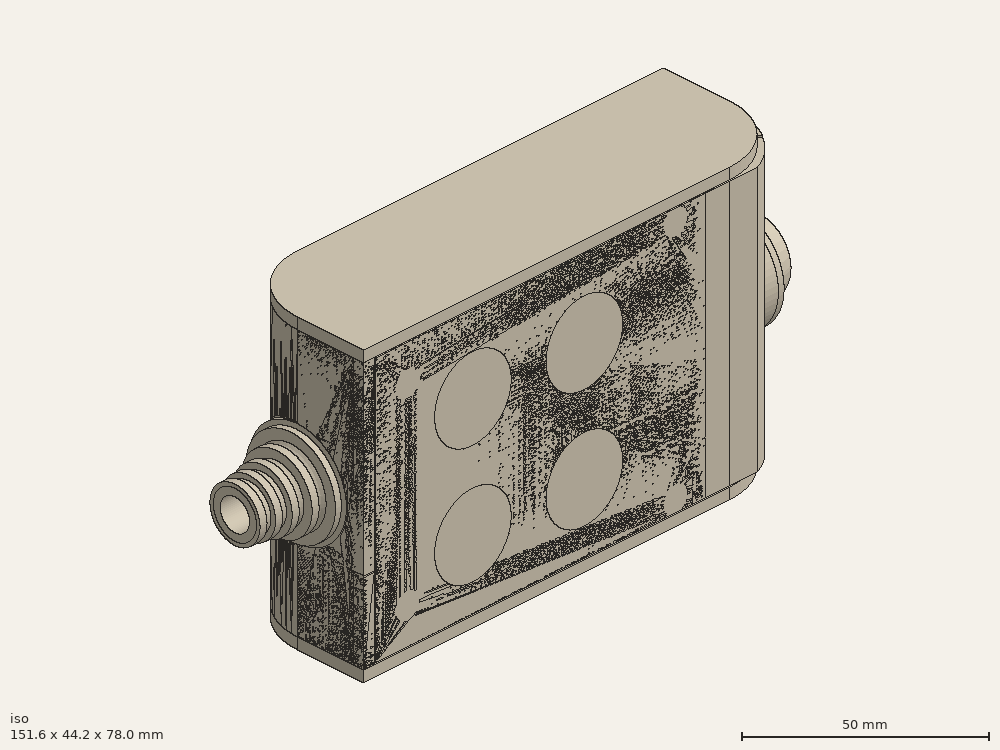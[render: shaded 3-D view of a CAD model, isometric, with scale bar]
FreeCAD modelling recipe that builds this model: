
FCSTD DOCUMENT  (FreeCAD 0.19R0.19.2)
Label: enclosure_158
License: All rights reserved
LicenseURL: http://en.wikipedia.org/wiki/All_rights_reserved
objects: Part::Feature×126, Part::Revolution×126, Part::MultiFuse×109, Sketcher::SketchObject×66, Part::Extrusion×51, Part::Cut×46, Part::Cylinder×44, Part::Fillet×43, Part::Box×28, App::MeasureDistance×4
note: 639 computed .brp shape members not serialized (recipe doc carries the construction recipe); baked Part::Feature solids carry a one-line shape summary decoded from their .brp

FEATURE [Sketcher::SketchObject] Sketch  label="topSketch"
  FullyConstrained = true
  sketch-geometry (20):
    g0: LineSegment StartX=5.21097e-06 StartY=3 StartZ=0 EndX=5.21097e-06 EndY=19 EndZ=0
    g1: ArcOfCircle CenterX=19 CenterY=19 CenterZ=0 NormalX=0 NormalY=0 NormalZ=1 AngleXU=0 Radius=19 StartAngle=1.5708 EndAngle=3.14159
    g2: ArcOfCircle CenterX=19 CenterY=19 CenterZ=0 NormalX=0 NormalY=0 NormalZ=1 AngleXU=0 Radius=16 StartAngle=1.5708 EndAngle=3.14159
    g3: LineSegment StartX=114 StartY=35 StartZ=0 EndX=19 EndY=35 EndZ=0
    g4: LineSegment StartX=5.21097e-06 StartY=3 StartZ=0 EndX=5.21097e-06 EndY=0 EndZ=0
    g5: LineSegment StartX=3 StartY=0 StartZ=0 EndX=5.21097e-06 EndY=0 EndZ=0
    g6: LineSegment StartX=3 StartY=19 StartZ=0 EndX=3 EndY=0 EndZ=0
    g7: LineSegment StartX=19 StartY=38 StartZ=0 EndX=124 EndY=38 EndZ=0
    g8: Circle CenterX=119 CenterY=35 CenterZ=0 NormalX=0 NormalY=0 NormalZ=1 AngleXU=0 Radius=1
    g9: Circle CenterX=121 CenterY=35 CenterZ=0 NormalX=0 NormalY=0 NormalZ=1 AngleXU=0 Radius=1
    g10: Circle CenterX=121 CenterY=33 CenterZ=0 NormalX=0 NormalY=0 NormalZ=1 AngleXU=0 Radius=1
    g11: BSplineCurve PolesCount=3 KnotsCount=2 Degree=2 IsPeriodic=0
    g12: GeomPoint X=119 Y=35 Z=0
    g13: GeomPoint X=121 Y=33 Z=0
    g14: LineSegment StartX=119 StartY=35 StartZ=0 EndX=114 EndY=35 EndZ=0
    g15: ArcOfCircle CenterX=105 CenterY=19 CenterZ=0 NormalX=0 NormalY=0 NormalZ=1 AngleXU=0 Radius=19 StartAngle=5.7297 EndAngle=6.28319
    g16: ArcOfCircle CenterX=105 CenterY=19 CenterZ=0 NormalX=0 NormalY=0 NormalZ=1 AngleXU=0 Radius=16 StartAngle=5.60905 EndAngle=6.28319
    g17: LineSegment StartX=121 StartY=33 StartZ=0 EndX=121 EndY=19 EndZ=0
    g18: LineSegment StartX=124 StartY=38 StartZ=0 EndX=124 EndY=19 EndZ=0
    g19: LineSegment StartX=117.5 StartY=9.01251 StartZ=0 EndX=121.163 EndY=9.0125 EndZ=0
  constraints (46):
    c: Vertical(g0)
    c: Block(g0)
    c: Coincident(g1,g0)
    c: Block(g1)
    c: Coincident(g2,g1)
    c: Block(g2)
    c: Coincident(g3,g2)
    c: Horizontal(g3)
    c: Tangent(g3,g2)
    c: Coincident(g4,g0)
    c: Distance(g4) = 3
    c: Vertical(g4)
    c: Coincident(g5,g4)
    c: Horizontal(g5)
    c: Coincident(g6,g2)
    c: Coincident(g6,g5)
    c: Vertical(g6)
    c: Horizontal(g7)
    c: Distance(g7) = 105
    c: Coincident(g7,g1)
    c: Block(g3)
    c: Weight(g8) = 1
    c: Equal(g8,g9)
    c: Equal(g8,g10)
    c: InternalAlignment(g8,g11)
    c: InternalAlignment(g9,g11)
    c: InternalAlignment(g10,g11)
    c: InternalAlignment(g12,g11)
    c: InternalAlignment(g13,g11)
    c: Block(g11)
    c: Coincident(g14,g11)
    c: Coincident(g14,g3)
    c: Horizontal(g14)
    c: Block(g15)
    c: Coincident(g16,g15)
    c: Block(g16)
    c: Coincident(g17,g11)
    c: Coincident(g17,g16)
    c: Vertical(g17)
    c: Distance(g17) = 14
    c: Coincident(g18,g7)
    c: Coincident(g18,g15)
    c: Vertical(g18)
    c: Distance(g18) = 19
    c: Coincident(g19,g16)
    c: Coincident(g19,g15)
FEATURE [Sketcher::SketchObject] Sketch001  label="bottomSketch"
  FullyConstrained = true
  sketch-geometry (32):
    g0: LineSegment StartX=3.3 StartY=-6.03275e-07 StartZ=0 EndX=98 EndY=-6.03275e-07 EndZ=0
    g1: ArcOfCircle CenterX=98 CenterY=19 CenterZ=0 NormalX=0 NormalY=0 NormalZ=1 AngleXU=0 Radius=19 StartAngle=4.71239 EndAngle=5.71103
    g2: LineSegment StartX=6.3 StartY=8 StartZ=0 EndX=3.3 EndY=8 EndZ=0
    g3: LineSegment StartX=3.3 StartY=8 StartZ=0 EndX=3.3 EndY=-6.03275e-07 EndZ=0
    g4: ArcOfCircle CenterX=8.3 CenterY=5 CenterZ=0 NormalX=0 NormalY=0 NormalZ=1 AngleXU=0 Radius=2 StartAngle=3.14159 EndAngle=4.71239
    g5: LineSegment StartX=6.3 StartY=8 StartZ=0 EndX=6.3 EndY=5 EndZ=0
    g6: ArcOfCircle CenterX=98 CenterY=19 CenterZ=0 NormalX=0 NormalY=0 NormalZ=1 AngleXU=0 Radius=12.7 StartAngle=4.71239 EndAngle=6.28319
    g7: LineSegment StartX=94.7 StartY=3 StartZ=0 EndX=8.3 EndY=3 EndZ=0
    g8-g12: Circle x5 (B-spline internal-alignment scaffolding for g13; pole/knot coordinates omitted)
    g13: BSplineCurve PolesCount=5 KnotsCount=3 Degree=3 IsPeriodic=0
    g14: GeomPoint X=98 Y=6.3 Z=0
    g15: GeomPoint X=96.3938 Y=4.71946 Z=0
    g16: GeomPoint X=94.7 Y=3 Z=0
    g17-g23: Circle x7 (B-spline internal-alignment scaffolding for g24; pole/knot coordinates omitted)
    g24: BSplineCurve PolesCount=7 KnotsCount=5 Degree=3 IsPeriodic=0
    g25-g29: GeomPoint x5 (B-spline internal-alignment scaffolding for g24; pole/knot coordinates omitted)
    g30: ArcOfCircle CenterX=98 CenterY=19 CenterZ=0 NormalX=0 NormalY=0 NormalZ=1 AngleXU=0 Radius=15.7 StartAngle=5.81226 EndAngle=6.28319
    g31: LineSegment StartX=110.7 StartY=19 StartZ=0 EndX=113.7 EndY=19 EndZ=0
  constraints (41):
    c: Horizontal(g0)
    c: Coincident(g1,g0)
    c: Block(g1)
    c: Horizontal(g2)
    c: Distance(g2) = 3
    c: Coincident(g3,g2)
    c: Vertical(g3)
    c: Coincident(g3,g0)
    c: Block(g4)
    c: Block(g2)
    c: Coincident(g5,g2)
    c: Coincident(g5,g4)
    c: Vertical(g5)
    c: Coincident(g6,g1)
    c: Block(g6)
    c: Coincident(g7,g4)
    c: Horizontal(g7)
    c: Block(g0)
    c: Block(g7)
    c: Block(g3)
    c: Coincident(g13,g6)
    c: Weight(g8) = 1
    c: Equal(g8, g9-g12) x4
    c: Coincident(g13,g7)
    c: InternalAlignment(g8-g12 -> g13) x5
    c: InternalAlignment(g14,g13)
    c: InternalAlignment(g15,g13)
    c: InternalAlignment(g16,g13)
    c: Block(g13)
    c: Weight(g17) = 1
    c: Equal(g17, g18-g23) x6
    c: Coincident(g24,g1)
    c: InternalAlignment(g17-g23 -> g24) x7
    c: InternalAlignment(g25-g29 -> g24) x5
    c: Block(g24)
    c: Coincident(g30,g24)
    c: Coincident(g31,g6)
    c: Coincident(g31,g30)
    c: Horizontal(g31)
    c: Block(g31)
    c: Block(g30)
FEATURE [Part::Extrusion] Extrude  label="top"
  Base = -> Sketch
  Dir = (0,0,1)
  DirMode = 2
  FaceMakerClass = Part::FaceMakerBullseye
  LengthFwd = 72
  LengthRev = 0
  Solid = true
  Symmetric = false
FEATURE [Part::Extrusion] Extrude001  label="bottom"
  Base = -> Sketch001
  Dir = (0,0,1)
  DirMode = 2
  FaceMakerClass = Part::FaceMakerBullseye
  LengthFwd = 71.4
  LengthRev = 0
  Placement = pos=(0,0,0.3) rot=(0,0,1;0rad)
  Solid = true
  Symmetric = false
FEATURE [Sketcher::SketchObject] Sketch002  label="topSketch001"
  FullyConstrained = true
  sketch-geometry (6):
    g0: ArcOfCircle CenterX=19 CenterY=19 CenterZ=0 NormalX=0 NormalY=0 NormalZ=1 AngleXU=0 Radius=19 StartAngle=1.5708 EndAngle=3.14159
    g1: LineSegment StartX=5.22862e-06 StartY=19 StartZ=0 EndX=5.22862e-06 EndY=1.19904e-11 EndZ=0
    g2: LineSegment StartX=19 StartY=38 StartZ=0 EndX=124 EndY=38 EndZ=0
    g3: LineSegment StartX=5.22862e-06 StartY=1.19904e-11 StartZ=0 EndX=105 EndY=1.19904e-11 EndZ=0
    g4: ArcOfCircle CenterX=105 CenterY=19 CenterZ=0 NormalX=0 NormalY=0 NormalZ=1 AngleXU=0 Radius=19 StartAngle=4.71239 EndAngle=6.28319
    g5: LineSegment StartX=124 StartY=38 StartZ=0 EndX=124 EndY=19 EndZ=0
  constraints (16):
    c: Block(g0)
    c: Coincident(g1,g0)
    c: Vertical(g1)
    c: Horizontal(g2)
    c: Distance(g2) = 105
    c: Coincident(g2,g0)
    c: Distance(g1) = 19
    c: Coincident(g3,g1)
    c: Horizontal(g3)
    c: Distance(g3) = 105
    c: Block(g4)
    c: Coincident(g4,g3)
    c: Coincident(g5,g2)
    c: Coincident(g5,g4)
    c: Vertical(g5)
    c: Distance(g5) = 19
FEATURE [Part::Extrusion] Extrude002  label="sideA"
  Base = -> Sketch002
  Dir = (0,0,1)
  DirMode = 2
  FaceMakerClass = Part::FaceMakerBullseye
  LengthFwd = 3
  LengthRev = 0
  Placement = pos=(0,0,-3) rot=(0,0,1;0rad)
  Solid = true
  Symmetric = false
FEATURE [Sketcher::SketchObject] Sketch003  label="topSketch002"
  FullyConstrained = true
  sketch-geometry (6):
    g0: LineSegment StartX=19 StartY=38 StartZ=0 EndX=117 EndY=38 EndZ=0
    g1: ArcOfCircle CenterX=19 CenterY=19 CenterZ=0 NormalX=0 NormalY=0 NormalZ=1 AngleXU=0 Radius=19 StartAngle=1.5708 EndAngle=3.14159
    g2: LineSegment StartX=117 StartY=38 StartZ=0 EndX=117 EndY=19 EndZ=0
    g3: LineSegment StartX=98 StartY=1.0161e-12 StartZ=0 EndX=5.22862e-06 EndY=1.0161e-12 EndZ=0
    g4: LineSegment StartX=5.22862e-06 StartY=19 StartZ=0 EndX=5.22862e-06 EndY=1.0161e-12 EndZ=0
    g5: ArcOfCircle CenterX=98 CenterY=19 CenterZ=0 NormalX=0 NormalY=0 NormalZ=1 AngleXU=0 Radius=19 StartAngle=4.71239 EndAngle=6.28319
  constraints (16):
    c: Horizontal(g0)
    c: Distance(g0) = 98
    c: Coincident(g1,g0)
    c: Block(g1)
    c: Coincident(g2,g0)
    c: Vertical(g2)
    c: Distance(g2) = 19
    c: Horizontal(g3)
    c: Coincident(g4,g1)
    c: Vertical(g4)
    c: Coincident(g3,g4)
    c: Block(g3)
    c: Coincident(g5,g2)
    c: Coincident(g5,g3)
    c: Block(g0)
    c: Block(g5)
FEATURE [Sketcher::SketchObject] Sketch004
  FullyConstrained = true
  MapMode = 3
  Placement = pos=(0,0,0) rot=(1,0,0;1.5708rad)
  Support = -> [Extrude]
  sketch-geometry (8):
    g0: Circle CenterX=80.351 CenterY=-67.6202 CenterZ=0 NormalX=0 NormalY=0 NormalZ=1 AngleXU=0 Radius=2
    g1: Circle CenterX=80.351 CenterY=-67.6202 CenterZ=0 NormalX=0 NormalY=0 NormalZ=1 AngleXU=0 Radius=3
    g2: Circle CenterX=80.351 CenterY=-4.92017 CenterZ=0 NormalX=0 NormalY=0 NormalZ=1 AngleXU=0 Radius=2
    g3: Circle CenterX=80.351 CenterY=-4.92017 CenterZ=0 NormalX=0 NormalY=0 NormalZ=1 AngleXU=0 Radius=3
    g4: Circle CenterX=23.851 CenterY=-4.92017 CenterZ=0 NormalX=0 NormalY=0 NormalZ=1 AngleXU=0 Radius=2
    g5: Circle CenterX=23.851 CenterY=-4.92017 CenterZ=0 NormalX=0 NormalY=0 NormalZ=1 AngleXU=0 Radius=3
    g6: Circle CenterX=23.851 CenterY=-67.6202 CenterZ=0 NormalX=0 NormalY=0 NormalZ=1 AngleXU=0 Radius=2
    g7: Circle CenterX=23.851 CenterY=-67.6202 CenterZ=0 NormalX=0 NormalY=0 NormalZ=1 AngleXU=0 Radius=3
  constraints (8):
    c: Block(g3)
    c: Block(g2)
    c: Block(g1)
    c: Block(g0)
    c: Block(g6)
    c: Block(g7)
    c: Block(g4)
    c: Block(g5)
FEATURE [Part::Extrusion] Extrude004
  Base = -> Sketch004
  Dir = (0,-1,2e-16)
  DirMode = 2
  FaceMakerClass = Part::FaceMakerBullseye
  LengthFwd = 6
  LengthRev = 0
  Placement = pos=(0,9,0) rot=(0,0,1;0rad)
  Solid = true
  Symmetric = false
FEATURE [Sketcher::SketchObject] Sketch005
  FullyConstrained = true
  MapMode = 3
  Placement = pos=(0,0,0) rot=(1,0,0;1.5708rad)
  Support = -> [Extrude]
  sketch-geometry (8):
    g0: Circle CenterX=80.351 CenterY=-67.6202 CenterZ=0 NormalX=0 NormalY=0 NormalZ=1 AngleXU=0 Radius=3
    g1: Circle CenterX=80.351 CenterY=-4.92017 CenterZ=0 NormalX=0 NormalY=0 NormalZ=1 AngleXU=0 Radius=3
    g2: Circle CenterX=23.851 CenterY=-4.92017 CenterZ=0 NormalX=0 NormalY=0 NormalZ=1 AngleXU=0 Radius=3
    g3: Circle CenterX=23.851 CenterY=-67.6202 CenterZ=0 NormalX=0 NormalY=0 NormalZ=1 AngleXU=0 Radius=3
    g4: Circle CenterX=23.851 CenterY=-67.6202 CenterZ=0 NormalX=0 NormalY=0 NormalZ=1 AngleXU=0 Radius=5
    g5: Circle CenterX=80.351 CenterY=-67.6202 CenterZ=0 NormalX=0 NormalY=0 NormalZ=1 AngleXU=0 Radius=5
    g6: Circle CenterX=23.851 CenterY=-4.92017 CenterZ=0 NormalX=0 NormalY=0 NormalZ=1 AngleXU=0 Radius=5
    g7: Circle CenterX=80.351 CenterY=-4.92017 CenterZ=0 NormalX=0 NormalY=0 NormalZ=1 AngleXU=0 Radius=5
  constraints (8):
    c: Block(g1)
    c: Block(g0)
    c: Block(g3)
    c: Block(g2)
    c: Block(g5)
    c: Block(g4)
    c: Block(g6)
    c: Block(g7)
FEATURE [Part::Extrusion] Extrude005
  Base = -> Sketch005
  Dir = (0,-1,2e-16)
  DirMode = 2
  FaceMakerClass = Part::FaceMakerBullseye
  LengthFwd = 2
  LengthRev = 0
  Solid = true
  Symmetric = false
FEATURE [Sketcher::SketchObject] Sketch006
  FullyConstrained = true
  MapMode = 3
  Placement = pos=(0,0,0) rot=(1,0,0;1.5708rad)
  sketch-geometry (8):
    g0: Circle CenterX=80.351 CenterY=-67.6202 CenterZ=0 NormalX=0 NormalY=0 NormalZ=1 AngleXU=0 Radius=3
    g1: Circle CenterX=80.351 CenterY=-4.92017 CenterZ=0 NormalX=0 NormalY=0 NormalZ=1 AngleXU=0 Radius=3
    g2: Circle CenterX=23.851 CenterY=-4.92017 CenterZ=0 NormalX=0 NormalY=0 NormalZ=1 AngleXU=0 Radius=3
    g3: Circle CenterX=23.851 CenterY=-67.6202 CenterZ=0 NormalX=0 NormalY=0 NormalZ=1 AngleXU=0 Radius=3
    g4: Circle CenterX=23.851 CenterY=-67.6202 CenterZ=0 NormalX=0 NormalY=0 NormalZ=1 AngleXU=0 Radius=5
    g5: Circle CenterX=80.351 CenterY=-67.6202 CenterZ=0 NormalX=0 NormalY=0 NormalZ=1 AngleXU=0 Radius=5
    g6: Circle CenterX=23.851 CenterY=-4.92017 CenterZ=0 NormalX=0 NormalY=0 NormalZ=1 AngleXU=0 Radius=5
    g7: Circle CenterX=80.351 CenterY=-4.92017 CenterZ=0 NormalX=0 NormalY=0 NormalZ=1 AngleXU=0 Radius=5
  constraints (8):
    c: Block(g1)
    c: Block(g0)
    c: Block(g3)
    c: Block(g2)
    c: Block(g5)
    c: Block(g4)
    c: Block(g6)
    c: Block(g7)
FEATURE [Part::Extrusion] Extrude007
  Base = -> Sketch006
  Dir = (0,-1,2e-16)
  DirMode = 2
  FaceMakerClass = Part::FaceMakerBullseye
  LengthFwd = 2
  LengthRev = 0
  Solid = true
  Symmetric = false
FEATURE [Part::Fillet] Fillet
  Base = -> Extrude007
  Edges = 4 edges r=1.99: [Edge6,Edge12,Edge18,Edge24]
FEATURE [Part::Cut] Cut
  Base = -> Extrude005
  Placement = pos=(0,5,0) rot=(0,0,1;0rad)
  Tool = -> Fillet
FEATURE [Part::MultiFuse] Fusion  label="pCBScrews"
  Placement = pos=(-2.5,0,72.3) rot=(0,0,1;0rad)
  Shapes = -> [Extrude004,Cut]
FEATURE [App::MeasureDistance] Distance  label="Distance: 0.69 mm"
  Distance = 0.685967
  P1 = (24.0138,2.9647,0.3)
  P2 = (23.8901,3,-0.373787)
FEATURE [App::MeasureDistance] Distance001  label="Distance: 0.53 mm"
  Distance = 0.533607
  P1 = (80.2939,3,72.2334)
  P2 = (80.281,2.99661,71.7)
FEATURE [Part::Fillet] Fillet001
  Base = -> Extrude001
  Edges = 1 edges r=2.4: [Edge17]
FEATURE [Part::Fillet] Fillet002  label="bottom001"
  Base = -> Fillet001
  Edges = 1 edges r=2.4: [Edge36]
FEATURE [Part::Fillet] Fillet003  label="top001"
  Base = -> Extrude
  Edges = 1 edges r=2: [Edge1]
FEATURE [Sketcher::SketchObject] Sketch007
  FullyConstrained = true
  sketch-geometry (16):
    g0: LineSegment StartX=4 StartY=0 StartZ=0 EndX=4 EndY=2.4 EndZ=0
    g1: LineSegment StartX=4 StartY=2.4 StartZ=0 EndX=7 EndY=2.4 EndZ=0
    g2: LineSegment StartX=4 StartY=0 StartZ=0 EndX=5.7 EndY=0 EndZ=0
    g3: LineSegment StartX=5.7 StartY=0 StartZ=0 EndX=5.7 EndY=-5.6 EndZ=0
    g4-g8: Circle x5 (B-spline internal-alignment scaffolding for g9; pole/knot coordinates omitted)
    g9: BSplineCurve PolesCount=5 KnotsCount=3 Degree=3 IsPeriodic=0
    g10: GeomPoint X=7 Y=2.4 Z=0
    g11: GeomPoint X=10.4582 Y=-1.55472 Z=0
    g12: GeomPoint X=14 Y=-5.6 Z=0
    g13: LineSegment StartX=14 StartY=-5.6 StartZ=0 EndX=14 EndY=-14.1 EndZ=0
    g14: LineSegment StartX=14 StartY=-14.1 StartZ=0 EndX=6.5 EndY=-14.1 EndZ=0
    g15: LineSegment StartX=5.7 StartY=-5.6 StartZ=0 EndX=6.5 EndY=-14.1 EndZ=0
  constraints (28):
    c: Distance(g0) = 2.4
    c: Vertical(g0)
    c: Block(g0)
    c: Coincident(g1,g0)
    c: Horizontal(g1)
    c: Distance(g1) = 3
    c: Coincident(g2,g0)
    c: Horizontal(g2)
    c: Distance(g2) = 1.7
    c: Coincident(g3,g2)
    c: Vertical(g3)
    c: Distance(g3) = 5.6
    c: Coincident(g9,g1)
    c: Weight(g4) = 1
    c: Equal(g4, g5-g8) x4
    c: InternalAlignment(g4-g8 -> g9) x5
    c: InternalAlignment(g10,g9)
    c: InternalAlignment(g11,g9)
    c: InternalAlignment(g12,g9)
    c: Block(g9)
    c: Coincident(g13,g9)
    c: Vertical(g13)
    c: Distance(g13) = 8.5
    c: Coincident(g14,g13)
    c: Horizontal(g14)
    c: Distance(g14) = 7.5
    c: Coincident(g15,g3)
    c: Coincident(g15,g14)
FEATURE [Part::Feature] Face
  shape: bbox 10 x 16.5 x 2e-07 mm, 1 faces, 0 solids (baked)
FEATURE [Part::Revolution] Revolve  label="plugHousing"
  Angle = 360
  Axis = (0,1,0)
  Base = (0,0,0)
  FaceMakerClass = Part::FaceMakerBullseye
  Placement = pos=(0,0,36.15) rot=(0,0,1;0rad)
  Solid = false
  Source = -> Face
  Symmetric = false
FEATURE [Part::Feature] Face001
  shape: bbox 10 x 16.5 x 2e-07 mm, 1 faces, 0 solids (baked)
FEATURE [Part::Revolution] Revolve001  label="plugHousing001"
  Angle = 360
  Axis = (0,1,0)
  Base = (0,0,0)
  FaceMakerClass = Part::FaceMakerBullseye
  Placement = pos=(0,0,36.15) rot=(0,0,1;0rad)
  Solid = false
  Source = -> Face001
  Symmetric = false
FEATURE [Part::MultiFuse] Fusion001  label="plugHousing002"
  Placement = pos=(0,0,0) rot=(0,0,1;1.5708rad)
  Shapes = -> [Revolve001,Revolve]
FEATURE [Part::Feature] Face002
  shape: bbox 10 x 16.5 x 2e-07 mm, 1 faces, 0 solids (baked)
FEATURE [Part::Revolution] Revolve003  label="plugHousing005"
  Angle = 360
  Axis = (0,1,0)
  Base = (0,0,0)
  FaceMakerClass = Part::FaceMakerBullseye
  Placement = pos=(0,0,36.15) rot=(0,0,1;0rad)
  Solid = false
  Source = -> Face002
  Symmetric = false
FEATURE [Part::Feature] Face003
  shape: bbox 10 x 16.5 x 2e-07 mm, 1 faces, 0 solids (baked)
FEATURE [Part::Revolution] Revolve002  label="plugHousing003"
  Angle = 360
  Axis = (0,1,0)
  Base = (0,0,0)
  FaceMakerClass = Part::FaceMakerBullseye
  Placement = pos=(0,0,36.15) rot=(0,0,1;0rad)
  Solid = false
  Source = -> Face003
  Symmetric = false
FEATURE [Part::MultiFuse] Fusion002  label="plugHousing004"
  Placement = pos=(0,0,0) rot=(0,0,1;1.5708rad)
  Shapes = -> [Revolve002,Revolve003]
FEATURE [Part::MultiFuse] Fusion003  label="plugHousing006"
  Placement = pos=(0,19,0) rot=(0,0,1;3.14159rad)
  Shapes = -> [Fusion002,Fusion001]
FEATURE [Part::Feature] Face004
  shape: bbox 10 x 16.5 x 2e-07 mm, 1 faces, 0 solids (baked)
FEATURE [Part::Revolution] Revolve006  label="plugHousing010"
  Angle = 360
  Axis = (0,1,0)
  Base = (0,0,0)
  FaceMakerClass = Part::FaceMakerBullseye
  Placement = pos=(0,0,36.15) rot=(0,0,1;0rad)
  Solid = false
  Source = -> Face004
  Symmetric = false
FEATURE [Part::Feature] Face005
  shape: bbox 10 x 16.5 x 2e-07 mm, 1 faces, 0 solids (baked)
FEATURE [Part::Revolution] Revolve007  label="plugHousing011"
  Angle = 360
  Axis = (0,1,0)
  Base = (0,0,0)
  FaceMakerClass = Part::FaceMakerBullseye
  Placement = pos=(0,0,36.15) rot=(0,0,1;0rad)
  Solid = false
  Source = -> Face005
  Symmetric = false
FEATURE [Part::Feature] Face006
  shape: bbox 10 x 16.5 x 2e-07 mm, 1 faces, 0 solids (baked)
FEATURE [Part::Revolution] Revolve004  label="plugHousing007"
  Angle = 360
  Axis = (0,1,0)
  Base = (0,0,0)
  FaceMakerClass = Part::FaceMakerBullseye
  Placement = pos=(0,0,36.15) rot=(0,0,1;0rad)
  Solid = false
  Source = -> Face006
  Symmetric = false
FEATURE [Part::MultiFuse] Fusion004  label="plugHousing009"
  Placement = pos=(0,0,0) rot=(0,0,1;1.5708rad)
  Shapes = -> [Revolve004,Revolve007]
FEATURE [Part::Feature] Face007
  shape: bbox 10 x 16.5 x 2e-07 mm, 1 faces, 0 solids (baked)
FEATURE [Part::Revolution] Revolve005  label="plugHousing008"
  Angle = 360
  Axis = (0,1,0)
  Base = (0,0,0)
  FaceMakerClass = Part::FaceMakerBullseye
  Placement = pos=(0,0,36.15) rot=(0,0,1;0rad)
  Solid = false
  Source = -> Face007
  Symmetric = false
FEATURE [Part::MultiFuse] Fusion005  label="plugHousing012"
  Placement = pos=(0,0,0) rot=(0,0,1;1.5708rad)
  Shapes = -> [Revolve006,Revolve005]
FEATURE [Part::MultiFuse] Fusion006  label="plugHousing013"
  Placement = pos=(0,19,0) rot=(0,0,1;3.14159rad)
  Shapes = -> [Fusion005,Fusion004]
FEATURE [Part::MultiFuse] Fusion007  label="plugHousing014"
  Placement = pos=(122.621,0,-0.15) rot=(0,0,1;0rad)
  Shapes = -> [Fusion003,Fusion006]
FEATURE [Part::Cylinder] Cylinder002
  Angle = 360
  AttacherType = Attacher::AttachEngine3D
  Height = 20
  Placement = pos=(0,0,36.15) rot=(0,0,1;0rad)
  Radius = 4
FEATURE [Part::Cylinder] Cylinder003
  Angle = 360
  AttacherType = Attacher::AttachEngine3D
  Height = 10
  Placement = pos=(0,0,36.15) rot=(0,0,1;0rad)
  Radius = 4
FEATURE [Part::MultiFuse] Fusion009  label="removeToCreateHoleForPlugHousing"
  Placement = pos=(70,19,36.15) rot=(0,1,0;1.5708rad)
  Shapes = -> [Cylinder002,Cylinder003]
FEATURE [Part::Cylinder] Cylinder004
  Angle = 360
  AttacherType = Attacher::AttachEngine3D
  Height = 20
  Placement = pos=(0,0,36.15) rot=(0,0,1;0rad)
  Radius = 4
FEATURE [Part::Cylinder] Cylinder005
  Angle = 360
  AttacherType = Attacher::AttachEngine3D
  Height = 10
  Placement = pos=(0,0,36.15) rot=(0,0,1;0rad)
  Radius = 4
FEATURE [Part::MultiFuse] Fusion010  label="removeToCreateHoleForPlugHousing001"
  Placement = pos=(70,19,36.15) rot=(0,1,0;1.5708rad)
  Shapes = -> [Cylinder004,Cylinder005]
FEATURE [Part::Cut] Cut001
  Base = -> Fillet003
  Tool = -> Fusion010
FEATURE [Part::Cut] Cut002  label="Bottom"
  Base = -> Fillet002
  Tool = -> Fusion009
FEATURE [Part::Feature] Face008
  shape: bbox 10 x 16.5 x 2e-07 mm, 1 faces, 0 solids (baked)
FEATURE [Part::Revolution] Revolve011  label="plugHousing021"
  Angle = 360
  Axis = (0,1,0)
  Base = (0,0,0)
  FaceMakerClass = Part::FaceMakerBullseye
  Placement = pos=(0,0,36.15) rot=(0,0,1;0rad)
  Solid = false
  Source = -> Face008
  Symmetric = false
FEATURE [Part::Feature] Face009
  shape: bbox 10 x 16.5 x 2e-07 mm, 1 faces, 0 solids (baked)
FEATURE [Part::Revolution] Revolve012  label="plugHousing022"
  Angle = 360
  Axis = (0,1,0)
  Base = (0,0,0)
  FaceMakerClass = Part::FaceMakerBullseye
  Placement = pos=(0,0,36.15) rot=(0,0,1;0rad)
  Solid = false
  Source = -> Face009
  Symmetric = false
FEATURE [Part::Feature] Face010 .. Face013  x4 (patterned run collapsed; names and placements below)
  shape: bbox 10 x 16.5 x 2e-07 mm, 1 faces, 0 solids (baked)
FEATURE [Part::Revolution] Revolve015  label="plugHousing027"
  Angle = 360
  Axis = (0,1,0)
  Base = (0,0,0)
  FaceMakerClass = Part::FaceMakerBullseye
  Placement = pos=(0,0,36.15) rot=(0,0,1;0rad)
  Solid = false
  Source = -> Face013
  Symmetric = false
FEATURE [Part::Feature] Face014
  shape: bbox 10 x 16.5 x 2e-07 mm, 1 faces, 0 solids (baked)
FEATURE [Part::Feature] Face015
  shape: bbox 10 x 16.5 x 2e-07 mm, 1 faces, 0 solids (baked)
FEATURE [Part::Feature] Face016
  shape: bbox 10 x 16.5 x 2e-07 mm, 1 faces, 0 solids (baked)
FEATURE [Part::Revolution] Revolve019  label="plugHousing033"
  Angle = 360
  Axis = (0,1,0)
  Base = (0,0,0)
  FaceMakerClass = Part::FaceMakerBullseye
  Placement = pos=(0,0,36.15) rot=(0,0,1;0rad)
  Solid = false
  Source = -> Face016
  Symmetric = false
FEATURE [Part::Feature] Face017
  shape: bbox 10 x 16.5 x 2e-07 mm, 1 faces, 0 solids (baked)
FEATURE [Part::Revolution] Revolve020  label="plugHousing034"
  Angle = 360
  Axis = (0,1,0)
  Base = (0,0,0)
  FaceMakerClass = Part::FaceMakerBullseye
  Placement = pos=(0,0,36.15) rot=(0,0,1;0rad)
  Solid = false
  Source = -> Face017
  Symmetric = false
FEATURE [Part::Feature] Face018
  shape: bbox 10 x 16.5 x 2e-07 mm, 1 faces, 0 solids (baked)
FEATURE [Part::Revolution] Revolve016  label="plugHousing030"
  Angle = 360
  Axis = (0,1,0)
  Base = (0,0,0)
  FaceMakerClass = Part::FaceMakerBullseye
  Placement = pos=(0,0,36.15) rot=(0,0,1;0rad)
  Solid = false
  Source = -> Face018
  Symmetric = false
FEATURE [Part::MultiFuse] Fusion020  label="plugHousing038"
  Placement = pos=(0,0,0) rot=(0,0,1;1.5708rad)
  Shapes = -> [Revolve016,Revolve020]
FEATURE [Part::Feature] Face019
  shape: bbox 10 x 16.5 x 2e-07 mm, 1 faces, 0 solids (baked)
FEATURE [Part::Feature] Face020
  shape: bbox 10 x 16.5 x 2e-07 mm, 1 faces, 0 solids (baked)
FEATURE [Part::Revolution] Revolve017  label="plugHousing031"
  Angle = 360
  Axis = (0,1,0)
  Base = (0,0,0)
  FaceMakerClass = Part::FaceMakerBullseye
  Placement = pos=(0,0,36.15) rot=(0,0,1;0rad)
  Solid = false
  Source = -> Face020
  Symmetric = false
FEATURE [Part::MultiFuse] Fusion021  label="plugHousing039"
  Placement = pos=(0,0,0) rot=(0,0,1;1.5708rad)
  Shapes = -> [Revolve019,Revolve017]
FEATURE [Part::MultiFuse] Fusion023  label="plugHousing041"
  Placement = pos=(0,19,0) rot=(0,0,1;3.14159rad)
  Shapes = -> [Fusion021,Fusion020]
FEATURE [Part::Revolution] Revolve022  label="plugHousing043"
  Angle = 360
  Axis = (0,1,0)
  Base = (0,0,0)
  FaceMakerClass = Part::FaceMakerBullseye
  Placement = pos=(0,0,36.15) rot=(0,0,1;0rad)
  Solid = false
  Source = -> Face019
  Symmetric = false
FEATURE [Part::Feature] Face021
  shape: bbox 10 x 16.5 x 2e-07 mm, 1 faces, 0 solids (baked)
FEATURE [Part::Revolution] Revolve023  label="plugHousing044"
  Angle = 360
  Axis = (0,1,0)
  Base = (0,0,0)
  FaceMakerClass = Part::FaceMakerBullseye
  Placement = pos=(0,0,36.15) rot=(0,0,1;0rad)
  Solid = false
  Source = -> Face021
  Symmetric = false
FEATURE [Part::Feature] Face022
  shape: bbox 10 x 16.5 x 2e-07 mm, 1 faces, 0 solids (baked)
FEATURE [Part::Revolution] Revolve018  label="plugHousing032"
  Angle = 360
  Axis = (0,1,0)
  Base = (0,0,0)
  FaceMakerClass = Part::FaceMakerBullseye
  Placement = pos=(0,0,36.15) rot=(0,0,1;0rad)
  Solid = false
  Source = -> Face022
  Symmetric = false
FEATURE [Part::MultiFuse] Fusion022  label="plugHousing040"
  Placement = pos=(0,0,0) rot=(0,0,1;1.5708rad)
  Shapes = -> [Revolve018,Revolve023]
FEATURE [Part::Feature] Face023
  shape: bbox 10 x 16.5 x 2e-07 mm, 1 faces, 0 solids (baked)
FEATURE [Part::Revolution] Revolve021  label="plugHousing035"
  Angle = 360
  Axis = (0,1,0)
  Base = (0,0,0)
  FaceMakerClass = Part::FaceMakerBullseye
  Placement = pos=(0,0,36.15) rot=(0,0,1;0rad)
  Solid = false
  Source = -> Face023
  Symmetric = false
FEATURE [Part::MultiFuse] Fusion018  label="plugHousing036"
  Placement = pos=(0,0,0) rot=(0,0,1;1.5708rad)
  Shapes = -> [Revolve022,Revolve021]
FEATURE [Part::MultiFuse] Fusion019  label="plugHousing037"
  Placement = pos=(0,19,0) rot=(0,0,1;3.14159rad)
  Shapes = -> [Fusion018,Fusion022]
FEATURE [Part::MultiFuse] Fusion024  label="plugHousing042"
  Placement = pos=(122.621,0,-0.15) rot=(0,0,1;0rad)
  Shapes = -> [Fusion023,Fusion019]
FEATURE [Part::Cylinder] Cylinder006
  Angle = 360
  AttacherType = Attacher::AttachEngine3D
  Height = 20
  Placement = pos=(0,0,36.15) rot=(0,0,1;0rad)
  Radius = 14.3
FEATURE [Part::Cylinder] Cylinder007
  Angle = 360
  AttacherType = Attacher::AttachEngine3D
  Height = 10
  Placement = pos=(0,0,36.15) rot=(0,0,1;0rad)
  Radius = 4
FEATURE [Part::MultiFuse] Fusion026  label="removeToCreteHoleForPlugHousing"
  Placement = pos=(70,19,36) rot=(0,1,0;1.5708rad)
  Shapes = -> [Cylinder006,Cylinder007]
FEATURE [Part::Box] Box001  label="Cube001"
  AttacherType = Attacher::AttachEngine3D
  Height = 28
  Length = 3
  Placement = pos=(110.7,19,22) rot=(0,0,1;0rad)
  Width = 15.7
FEATURE [Part::Cut] Cut003  label="top002"
  Base = -> Cut001
  Tool = -> Fusion007
FEATURE [Part::Revolution] Revolve008  label="plugHousing015"
  Angle = 360
  Axis = (0,1,0)
  Base = (0,0,0)
  FaceMakerClass = Part::FaceMakerBullseye
  Placement = pos=(0,0,36.15) rot=(0,0,1;0rad)
  Solid = false
  Source = -> Face010
  Symmetric = false
FEATURE [Part::MultiFuse] Fusion013  label="plugHousing020"
  Placement = pos=(0,0,0) rot=(0,0,1;1.5708rad)
  Shapes = -> [Revolve008,Revolve012]
FEATURE [Part::Cut] Cut004  label="top003"
  Base = -> Cut003
  Placement = pos=(1,0,0) rot=(0,0,1;0rad)
  Tool = -> Fusion026
FEATURE [Part::Cylinder] Cylinder008
  Angle = 360
  AttacherType = Attacher::AttachEngine3D
  Height = 20
  Placement = pos=(0,0,36.15) rot=(0,0,1;0rad)
  Radius = 10.3
FEATURE [Part::Cylinder] Cylinder009
  Angle = 360
  AttacherType = Attacher::AttachEngine3D
  Height = 10
  Placement = pos=(0,0,36.15) rot=(0,0,1;0rad)
  Radius = 4
FEATURE [Part::MultiFuse] Fusion027  label="removeToCreteHoleForPlugHousing001"
  Placement = pos=(70,19,36) rot=(0,1,0;1.5708rad)
  Shapes = -> [Cylinder008,Cylinder009]
FEATURE [Part::Cut] Cut005  label="plugHousingTab"
  Base = -> Box001
  Tool = -> Fusion027
FEATURE [Part::MultiFuse] Fusion028  label="plugHousing045"
  Shapes = -> [Fusion024,Cut005]
FEATURE [Part::Box] Box002  label="Cube002"
  AttacherType = Attacher::AttachEngine3D
  Height = 28.8
  Length = 3
  Placement = pos=(107.3,28,21.6) rot=(0,0,1;0rad)
  Width = 7
FEATURE [Part::Box] Box003  label="Cube003"
  AttacherType = Attacher::AttachEngine3D
  Height = 3
  Length = 6.4
  Placement = pos=(107.3,28,18.6) rot=(0,0,1;0rad)
  Width = 7
FEATURE [Part::Box] Box004  label="Cube004"
  AttacherType = Attacher::AttachEngine3D
  Height = 3
  Length = 6.4
  Placement = pos=(107.3,28,50.4) rot=(0,0,1;0rad)
  Width = 7
FEATURE [Part::MultiFuse] Fusion029  label="plugHousingBracketHolder"
  Shapes = -> [Box004,Box002,Box003]
FEATURE [Part::Cylinder] Cylinder010
  Angle = 360
  AttacherType = Attacher::AttachEngine3D
  Height = 20
  Placement = pos=(0,0,36.15) rot=(0,0,1;0rad)
  Radius = 14.3
FEATURE [Part::Cylinder] Cylinder011
  Angle = 360
  AttacherType = Attacher::AttachEngine3D
  Height = 10
  Placement = pos=(0,0,36.15) rot=(0,0,1;0rad)
  Radius = 4
FEATURE [Part::MultiFuse] Fusion030  label="removeToCreteHoleForPlugHousing002"
  Placement = pos=(70,19,36) rot=(0,1,0;1.5708rad)
  Shapes = -> [Cylinder010,Cylinder011]
FEATURE [Part::Cut] Cut006  label="plugHousingBracketHolder001"
  Base = -> Fusion029
  Tool = -> Fusion030
FEATURE [Part::Cylinder] Cylinder012
  Angle = 360
  AttacherType = Attacher::AttachEngine3D
  Height = 20
  Placement = pos=(0,0,36.15) rot=(0,0,1;0rad)
  Radius = 7
FEATURE [Part::Cylinder] Cylinder013
  Angle = 360
  AttacherType = Attacher::AttachEngine3D
  Height = 10
  Placement = pos=(0,0,36.15) rot=(0,0,1;0rad)
  Radius = 4
FEATURE [Part::MultiFuse] Fusion032  label="removeToCreteHoleForPlugHousing003"
  Placement = pos=(70,19,36) rot=(0,1,0;1.5708rad)
  Shapes = -> [Cylinder012,Cylinder013]
FEATURE [Part::Cut] Cut007  label="bottom002"
  Base = -> Cut002
  Tool = -> Fusion032
FEATURE [Sketcher::SketchObject] Sketch008
  FullyConstrained = true
  sketch-geometry (54):
    g0: LineSegment StartX=-4.2 StartY=0 StartZ=0 EndX=-6.2 EndY=0 EndZ=0
    g1: LineSegment StartX=-14 StartY=-18 StartZ=0 EndX=-14 EndY=-26.5 EndZ=0
    g2: LineSegment StartX=-4.2 StartY=0 StartZ=0 EndX=-4.2 EndY=-13.4877 EndZ=0
    g3: Circle CenterX=-4.2 CenterY=-13.4877 CenterZ=0 NormalX=0 NormalY=0 NormalZ=1 AngleXU=0 Radius=1
    g4: Circle CenterX=-4.2 CenterY=-26.5 CenterZ=0 NormalX=0 NormalY=0 NormalZ=1 AngleXU=0 Radius=1
    g5: Circle CenterX=-8.2 CenterY=-26.5 CenterZ=0 NormalX=0 NormalY=0 NormalZ=1 AngleXU=0 Radius=1
    g6: BSplineCurve PolesCount=3 KnotsCount=2 Degree=2 IsPeriodic=0
    g7: GeomPoint X=-4.2 Y=-13.4877 Z=0
    g8: GeomPoint X=-8.2 Y=-26.5 Z=0
    g9: LineSegment StartX=-14 StartY=-26.5 StartZ=0 EndX=-8.2 EndY=-26.5 EndZ=0
    g10: LineSegment StartX=-10.15 StartY=-12 StartZ=0 EndX=-10.15 EndY=-14 EndZ=0
    g11: LineSegment StartX=-12.8401 StartY=-16 StartZ=0 EndX=-10.1571 EndY=-16 EndZ=0
    g12: LineSegment StartX=-10.15 StartY=-14 StartZ=0 EndX=-8.70761 EndY=-14 EndZ=0
    g13: LineSegment StartX=-12.8401 StartY=-16 StartZ=0 EndX=-12.8401 EndY=-17.6958 EndZ=0
    g14: LineSegment StartX=-10.15 StartY=-12 StartZ=0 EndX=-7.79258 EndY=-12 EndZ=0
    g15: Circle CenterX=-6.2215 CenterY=-2 CenterZ=0 NormalX=0 NormalY=0 NormalZ=1 AngleXU=0 Radius=1
    g16: Circle CenterX=-6.22762 CenterY=-2.58724 CenterZ=0 NormalX=0 NormalY=0 NormalZ=1 AngleXU=0 Radius=1
    g17: Circle CenterX=-6.32538 CenterY=-4 CenterZ=0 NormalX=0 NormalY=0 NormalZ=1 AngleXU=0 Radius=1
    g18: BSplineCurve PolesCount=3 KnotsCount=2 Degree=2 IsPeriodic=0
    g19: GeomPoint X=-6.2215 Y=-2 Z=0
    g20: GeomPoint X=-6.32538 Y=-4 Z=0
    g21: Circle CenterX=-6.48644 CenterY=-5.99526 CenterZ=0 NormalX=0 NormalY=0 NormalZ=1 AngleXU=0 Radius=1
    g22: Circle CenterX=-6.58486 CenterY=-6.99526 CenterZ=0 NormalX=0 NormalY=0 NormalZ=1 AngleXU=0 Radius=1
    g23: Circle CenterX=-6.77343 CenterY=-8 CenterZ=0 NormalX=0 NormalY=0 NormalZ=1 AngleXU=0 Radius=1
    g24: BSplineCurve PolesCount=3 KnotsCount=2 Degree=2 IsPeriodic=0
    g25: GeomPoint X=-6.48644 Y=-5.99526 Z=0
    g26: GeomPoint X=-6.77343 Y=-8 Z=0
    g27: Circle CenterX=-7.19003 CenterY=-10 CenterZ=0 NormalX=0 NormalY=0 NormalZ=1 AngleXU=0 Radius=1
    g28: Circle CenterX=-7.44407 CenterY=-11.0915 CenterZ=0 NormalX=0 NormalY=0 NormalZ=1 AngleXU=0 Radius=1
    g29: Circle CenterX=-7.79258 CenterY=-12 CenterZ=0 NormalX=0 NormalY=0 NormalZ=1 AngleXU=0 Radius=1
    g30: BSplineCurve PolesCount=3 KnotsCount=2 Degree=2 IsPeriodic=0
    g31: GeomPoint X=-7.19003 Y=-10 Z=0
    g32: GeomPoint X=-7.79258 Y=-12 Z=0
    g33: Circle CenterX=-8.70761 CenterY=-14 CenterZ=0 NormalX=0 NormalY=0 NormalZ=1 AngleXU=0 Radius=1
    g34: Circle CenterX=-9.33087 CenterY=-15.1837 CenterZ=0 NormalX=0 NormalY=0 NormalZ=1 AngleXU=0 Radius=1
    g35: Circle CenterX=-10.1571 CenterY=-16 CenterZ=0 NormalX=0 NormalY=0 NormalZ=1 AngleXU=0 Radius=1
    g36: BSplineCurve PolesCount=3 KnotsCount=2 Degree=2 IsPeriodic=0
    g37: GeomPoint X=-8.70761 Y=-14 Z=0
    g38: GeomPoint X=-10.1571 Y=-16 Z=0
    g39: Circle CenterX=-12.8401 CenterY=-17.6958 CenterZ=0 NormalX=0 NormalY=0 NormalZ=1 AngleXU=0 Radius=1
    g40: Circle CenterX=-13.3521 CenterY=-17.9027 CenterZ=0 NormalX=0 NormalY=0 NormalZ=1 AngleXU=0 Radius=1
    g41: Circle CenterX=-14 CenterY=-18 CenterZ=0 NormalX=0 NormalY=0 NormalZ=1 AngleXU=0 Radius=1
    g42: BSplineCurve PolesCount=3 KnotsCount=2 Degree=2 IsPeriodic=0
    g43: GeomPoint X=-12.8401 Y=-17.6958 Z=0
    g44: GeomPoint X=-14 Y=-18 Z=0
    g45: LineSegment StartX=-6.2 StartY=0 StartZ=0 EndX=-7.2 EndY=0 EndZ=0
    g46: LineSegment StartX=-7.2 StartY=0 StartZ=0 EndX=-7.2 EndY=-2 EndZ=0
    g47: LineSegment StartX=-7.2 StartY=-2 StartZ=0 EndX=-6.2215 EndY=-2 EndZ=0
    g48: LineSegment StartX=-6.32538 StartY=-4 StartZ=0 EndX=-7.65538 EndY=-4 EndZ=0
    g49: LineSegment StartX=-7.65538 StartY=-4 StartZ=0 EndX=-7.65538 EndY=-5.99526 EndZ=0
    g50: LineSegment StartX=-7.65538 StartY=-5.99526 StartZ=0 EndX=-6.48644 EndY=-5.99526 EndZ=0
    g51: LineSegment StartX=-6.77343 StartY=-8 StartZ=0 EndX=-8.43343 EndY=-8 EndZ=0
    g52: LineSegment StartX=-8.43343 StartY=-8 StartZ=0 EndX=-8.43343 EndY=-10 EndZ=0
    g53: LineSegment StartX=-8.43343 StartY=-10 StartZ=0 EndX=-7.19003 EndY=-10 EndZ=0
  constraints (112):
    c: Horizontal(g0)
    c: Distance(g0) = 2
    c: Block(g0)
    c: Vertical(g1)
    c: Coincident(g2,g0)
    c: Vertical(g2)
    c: Block(g2)
    c: Coincident(g6,g2)
    c: Weight(g3) = 1
    c: Equal(g3,g4)
    c: Equal(g3,g5)
    c: InternalAlignment(g3,g6)
    c: InternalAlignment(g4,g6)
    c: InternalAlignment(g5,g6)
    c: InternalAlignment(g7,g6)
    c: InternalAlignment(g8,g6)
    c: Block(g6)
    c: Coincident(g9,g1)
    c: Coincident(g9,g6)
    c: Horizontal(g9)
    c: Vertical(g10)
    c: Block(g10)
    c: Horizontal(g11)
    c: Block(g11)
    c: Coincident(g12,g10)
    c: Horizontal(g12)
    c: Block(g12)
    c: Coincident(g13,g11)
    c: Vertical(g13)
    c: Block(g13)
    c: Coincident(g14,g10)
    c: Horizontal(g14)
    c: Block(g14)
    c: Block(g9)
    c: Block(g1)
    c: Weight(g15) = 1
    c: Equal(g15,g16)
    c: Equal(g15,g17)
    c: InternalAlignment(g15,g18)
    c: InternalAlignment(g16,g18)
    c: InternalAlignment(g17,g18)
    c: InternalAlignment(g19,g18)
    c: InternalAlignment(g20,g18)
    c: Weight(g21) = 1
    c: Equal(g21,g22)
    c: Equal(g21,g23)
    c: InternalAlignment(g21,g24)
    c: InternalAlignment(g22,g24)
    c: InternalAlignment(g23,g24)
    c: InternalAlignment(g25,g24)
    c: InternalAlignment(g26,g24)
    c: Weight(g27) = 1
    c: Equal(g27,g28)
    c: Equal(g27,g29)
    c: Coincident(g30,g14)
    c: InternalAlignment(g27,g30)
    c: InternalAlignment(g28,g30)
    c: InternalAlignment(g29,g30)
    c: InternalAlignment(g31,g30)
    c: InternalAlignment(g32,g30)
    c: Coincident(g36,g12)
    c: Weight(g33) = 1
    c: Equal(g33,g34)
    c: Equal(g33,g35)
    c: Coincident(g36,g11)
    c: InternalAlignment(g33,g36)
    c: InternalAlignment(g34,g36)
    c: InternalAlignment(g35,g36)
    c: InternalAlignment(g37,g36)
    c: InternalAlignment(g38,g36)
    c: Coincident(g42,g13)
    c: Weight(g39) = 1
    c: Equal(g39,g40)
    c: Equal(g39,g41)
    c: Coincident(g42,g1)
    c: InternalAlignment(g39,g42)
    c: InternalAlignment(g40,g42)
    c: InternalAlignment(g41,g42)
    c: InternalAlignment(g43,g42)
    c: InternalAlignment(g44,g42)
    c: Block(g18)
    c: Block(g24)
    c: Block(g30)
    c: Block(g36)
    c: Block(g42)
    c: Horizontal(g45)
    c: Coincident(g45,g0)
    c: Vertical(g46)
    c: Coincident(g46,g45)
    c: Coincident(g47,g46)
    c: Coincident(g47,g18)
    c: Horizontal(g47)
    c: Block(g46)
    c: Coincident(g48,g18)
    c: Horizontal(g48)
    c: Distance(g48) = 1.33
    c: Vertical(g49)
    c: Coincident(g49,g48)
    c: Coincident(g50,g49)
    c: Coincident(g50,g24)
    c: Horizontal(g50)
    c: Tangent(g50,g22)
    c: Horizontal(g51)
    c: Coincident(g51,g24)
    c: Block(g51)
    c: Vertical(g52)
    c: Block(g52)
    c: Coincident(g52,g51)
    c: Coincident(g53,g52)
    c: Coincident(g53,g30)
    c: Horizontal(g53)
    c: Distance(g1) = 8.5
FEATURE [Part::Feature] Face024
  shape: bbox 9.8 x 26.5 x 2e-07 mm, 1 faces, 0 solids (baked)
FEATURE [Part::Revolution] Revolve024
  Angle = 360
  Axis = (0,1,0)
  Base = (0,0,0)
  FaceMakerClass = Part::FaceMakerBullseye
  Placement = pos=(0,0,0) rot=(0,0,1;1.5708rad)
  Solid = false
  Source = -> Face024
  Symmetric = false
FEATURE [Part::Feature] Face025
  shape: bbox 9.8 x 26.5 x 2e-07 mm, 1 faces, 0 solids (baked)
FEATURE [Part::Revolution] Revolve025
  Angle = 360
  Axis = (0,1,0)
  Base = (0,0,0)
  FaceMakerClass = Part::FaceMakerBullseye
  Placement = pos=(0,0,0) rot=(0,0,1;1.5708rad)
  Solid = false
  Source = -> Face025
  Symmetric = false
FEATURE [Part::MultiFuse] Fusion033
  Placement = pos=(-18,19,36) rot=(0,0,1;0rad)
  Shapes = -> [Revolve025,Revolve024]
FEATURE [Part::Cylinder] Cylinder014
  Angle = 360
  AttacherType = Attacher::AttachEngine3D
  Height = 20
  Placement = pos=(0,0,36.15) rot=(0,0,1;0rad)
  Radius = 14.3
FEATURE [Part::Cylinder] Cylinder015
  Angle = 360
  AttacherType = Attacher::AttachEngine3D
  Height = 10
  Placement = pos=(0,0,36.15) rot=(0,0,1;0rad)
  Radius = 4
FEATURE [Part::MultiFuse] Fusion034  label="removeToCreteHoleForPlugHousing004"
  Placement = pos=(-42,19,36) rot=(0,1,0;1.5708rad)
  Shapes = -> [Cylinder014,Cylinder015]
FEATURE [Part::Cut] Cut008  label="top004"
  Base = -> Cut004
  Placement = pos=(-1,0,0) rot=(0,0,1;0rad)
  Tool = -> Fusion034
FEATURE [Part::Box] Box005  label="Cube005"
  AttacherType = Attacher::AttachEngine3D
  Height = 28
  Length = 3
  Placement = pos=(110.7,19,22) rot=(0,0,1;0rad)
  Width = 15.7
FEATURE [Part::Cylinder] Cylinder016
  Angle = 360
  AttacherType = Attacher::AttachEngine3D
  Height = 10
  Placement = pos=(0,0,36.15) rot=(0,0,1;0rad)
  Radius = 4
FEATURE [Part::Cylinder] Cylinder017
  Angle = 360
  AttacherType = Attacher::AttachEngine3D
  Height = 20
  Placement = pos=(0,0,36.15) rot=(0,0,1;0rad)
  Radius = 10.3
FEATURE [Part::MultiFuse] Fusion035  label="removeToCreteHoleForPlugHousing005"
  Placement = pos=(70,19,36) rot=(0,1,0;1.5708rad)
  Shapes = -> [Cylinder017,Cylinder016]
FEATURE [Part::Cut] Cut009  label="plugHousingTab001"
  Base = -> Box005
  Placement = pos=(-107.4,-14,0) rot=(0,0,1;0rad)
  Tool = -> Fusion035
FEATURE [Part::Box] Box006  label="Cube006"
  AttacherType = Attacher::AttachEngine3D
  Height = 28
  Length = 3
  Placement = pos=(110.7,19,22) rot=(0,0,1;0rad)
  Width = 15.7
FEATURE [Part::Cylinder] Cylinder018
  Angle = 360
  AttacherType = Attacher::AttachEngine3D
  Height = 10
  Placement = pos=(0,0,36.15) rot=(0,0,1;0rad)
  Radius = 4
FEATURE [Part::Cylinder] Cylinder019
  Angle = 360
  AttacherType = Attacher::AttachEngine3D
  Height = 20
  Placement = pos=(0,0,36.15) rot=(0,0,1;0rad)
  Radius = 10.3
FEATURE [Part::MultiFuse] Fusion036  label="removeToCreteHoleForPlugHousing006"
  Placement = pos=(70,19,36) rot=(0,1,0;1.5708rad)
  Shapes = -> [Cylinder019,Cylinder018]
FEATURE [Part::Cut] Cut010  label="plugHousingTab002"
  Base = -> Box006
  Placement = pos=(-107.4,-14,0) rot=(0,0,1;0rad)
  Tool = -> Fusion036
FEATURE [Part::MultiFuse] Fusion037
  Placement = pos=(9.6,23,0) rot=(0,0,1;3.14159rad)
  Shapes = -> [Cut009,Cut010]
FEATURE [Part::Box] Box  label="Cube"
  AttacherType = Attacher::AttachEngine3D
  Height = 10
  Length = 3
  Placement = pos=(3.3,4,12) rot=(0,0,1;0rad)
  Width = 10
FEATURE [Part::Fillet] Fillet004
  Base = -> Fusion028
  Edges = 1 edges r=2: [Edge25]
FEATURE [Part::Fillet] Fillet005  label="plugHousing046"
  Base = -> Fillet004
  Edges = 1 edges r=2: [Edge8]
FEATURE [Part::Fillet] Fillet006
  Base = -> Box
  Edges = 1 edges r=2: [Edge11]
FEATURE [Part::Box] Box007  label="Cube007"
  AttacherType = Attacher::AttachEngine3D
  Height = 10
  Length = 3
  Placement = pos=(3.3,4,50) rot=(0,0,1;0rad)
  Width = 10
FEATURE [Part::Fillet] Fillet007
  Base = -> Box007
  Edges = 1 edges r=2: [Edge12]
FEATURE [Part::Box] Box008  label="Cube008"
  AttacherType = Attacher::AttachEngine3D
  Height = 28
  Length = 4
  Placement = pos=(5,0,22) rot=(0,0,1;0rad)
  Width = 10
FEATURE [Part::Fillet] Fillet008
  Base = -> Box008
  Edges = 1 edges r=1: [Edge7]
FEATURE [Part::Fillet] Fillet009
  Base = -> Fillet008
  Edges = 1 edges r=2: [Edge5]
FEATURE [Part::Fillet] Fillet010
  Base = -> Fillet009
  Edges = 1 edges r=2: [Edge2]
FEATURE [Sketcher::SketchObject] Sketch009  label="topSketch003"
  FullyConstrained = true
  sketch-geometry (4):
    g0: LineSegment StartX=16.8446 StartY=31.512 StartZ=0 EndX=16.3251 EndY=34.4666 EndZ=0
    g1: ArcOfCircle CenterX=19 CenterY=19.2524 CenterZ=0 NormalX=0 NormalY=0 NormalZ=1 AngleXU=0 Radius=15.4476 StartAngle=1.74483 EndAngle=2.72717
    g2: ArcOfCircle CenterX=19 CenterY=19.2524 CenterZ=0 NormalX=0 NormalY=0 NormalZ=1 AngleXU=0 Radius=12.4476 StartAngle=1.74483 EndAngle=2.73189
    g3: LineSegment StartX=4.86004 StartY=25.4725 StartZ=0 EndX=7.58253 EndY=24.2107 EndZ=0
  constraints (7):
    c: Block(g0)
    c: Coincident(g1,g0)
    c: Coincident(g2,g0)
    c: Coincident(g3,g1)
    c: Coincident(g3,g2)
    c: Block(g1)
    c: Block(g2)
FEATURE [Part::Extrusion] Extrude008
  Base = -> Sketch009
  Dir = (0,0,1)
  DirMode = 2
  FaceMakerClass = Part::FaceMakerBullseye
  LengthFwd = 10
  LengthRev = 0
  Placement = pos=(0,0,31) rot=(0,0,1;0rad)
  Solid = true
  Symmetric = false
FEATURE [Part::Cylinder] Cylinder020
  Angle = 360
  AttacherType = Attacher::AttachEngine3D
  Height = 20
  Placement = pos=(0,0,36.15) rot=(0,0,1;0rad)
  Radius = 8.2
FEATURE [Part::Cylinder] Cylinder021
  Angle = 360
  AttacherType = Attacher::AttachEngine3D
  Height = 10
  Placement = pos=(0,0,36.15) rot=(0,0,1;0rad)
  Radius = 4
FEATURE [Part::MultiFuse] Fusion038  label="removeToCreteHoleForPlugHousing007"
  Placement = pos=(-42,19,36) rot=(0,1,0;1.5708rad)
  Shapes = -> [Cylinder020,Cylinder021]
FEATURE [Part::Cut] Cut011
  Base = -> Extrude008
  Tool = -> Fusion038
FEATURE [Part::Fillet] Fillet011
  Base = -> Cut011
  Edges = 1 edges r=2: [Edge1]
FEATURE [Part::Fillet] Fillet012
  Base = -> Fillet011
  Edges = 1 edges r=2.5: [Edge1]
FEATURE [Part::Fillet] Fillet013
  Base = -> Fillet012
  Edges = 1 edges r=2.5: [Edge2]
FEATURE [Part::Box] Box010  label="Cube010"
  AttacherType = Attacher::AttachEngine3D
  Height = 16
  Length = 8
  Placement = pos=(12.7,31.52,28) rot=(0,0,1;0rad)
  Width = 4
FEATURE [Sketcher::SketchObject] Sketch010  label="topSketch004"
  FullyConstrained = true
  sketch-geometry (4):
    g0: LineSegment StartX=16.8446 StartY=31.512 StartZ=0 EndX=16.3251 EndY=34.4666 EndZ=0
    g1: ArcOfCircle CenterX=19 CenterY=19.2524 CenterZ=0 NormalX=0 NormalY=0 NormalZ=1 AngleXU=0 Radius=15.4476 StartAngle=1.74483 EndAngle=2.72717
    g2: ArcOfCircle CenterX=19 CenterY=19.2524 CenterZ=0 NormalX=0 NormalY=0 NormalZ=1 AngleXU=0 Radius=12.4476 StartAngle=1.74483 EndAngle=2.73189
    g3: LineSegment StartX=4.86004 StartY=25.4725 StartZ=0 EndX=7.58253 EndY=24.2107 EndZ=0
  constraints (7):
    c: Block(g0)
    c: Coincident(g1,g0)
    c: Coincident(g2,g0)
    c: Coincident(g3,g1)
    c: Coincident(g3,g2)
    c: Block(g1)
    c: Block(g2)
FEATURE [Part::Cylinder] Cylinder022
  Angle = 360
  AttacherType = Attacher::AttachEngine3D
  Height = 10
  Placement = pos=(0,0,36.15) rot=(0,0,1;0rad)
  Radius = 4
FEATURE [Sketcher::SketchObject] Sketch011  label="topSketch005"
  FullyConstrained = true
  sketch-geometry (4):
    g0: LineSegment StartX=16.8446 StartY=31.512 StartZ=0 EndX=16.3251 EndY=34.4666 EndZ=0
    g1: ArcOfCircle CenterX=19 CenterY=19.2524 CenterZ=0 NormalX=0 NormalY=0 NormalZ=1 AngleXU=0 Radius=15.4476 StartAngle=1.74483 EndAngle=2.72717
    g2: ArcOfCircle CenterX=19 CenterY=19.2524 CenterZ=0 NormalX=0 NormalY=0 NormalZ=1 AngleXU=0 Radius=12.4476 StartAngle=1.74483 EndAngle=2.73189
    g3: LineSegment StartX=4.86004 StartY=25.4725 StartZ=0 EndX=7.58253 EndY=24.2107 EndZ=0
  constraints (7):
    c: Block(g0)
    c: Coincident(g1,g0)
    c: Coincident(g2,g0)
    c: Coincident(g3,g1)
    c: Coincident(g3,g2)
    c: Block(g1)
    c: Block(g2)
FEATURE [Part::Extrusion] Extrude010
  Base = -> Sketch011
  Dir = (0,0,1)
  DirMode = 2
  FaceMakerClass = Part::FaceMakerBullseye
  LengthFwd = 10.6
  LengthRev = 0
  Placement = pos=(0,0,31) rot=(0,0,1;0rad)
  Solid = true
  Symmetric = false
FEATURE [Part::Cylinder] Cylinder023
  Angle = 360
  AttacherType = Attacher::AttachEngine3D
  Height = 20
  Placement = pos=(0,0,36.15) rot=(0,0,1;0rad)
  Radius = 8.2
FEATURE [Part::MultiFuse] Fusion039  label="removeToCreteHoleForPlugHousing008"
  Placement = pos=(-42,19,36) rot=(0,1,0;1.5708rad)
  Shapes = -> [Cylinder023,Cylinder022]
FEATURE [Part::Cut] Cut012
  Base = -> Extrude010
  Placement = pos=(0,0,-0.3) rot=(0,0,1;0rad)
  Tool = -> Fusion039
FEATURE [Part::Cut] Cut013
  Base = -> Box010
  Tool = -> Cut012
FEATURE [Part::Fillet] Fillet014
  Base = -> Cut013
  Edges = 1 edges r=0.7: [Edge13]
FEATURE [Part::Fillet] Fillet015
  Base = -> Fillet014
  Edges = 1 edges r=0.7: [Edge13]
FEATURE [Part::Fillet] Fillet016
  Base = -> Fillet015
  Edges = 1 edges r=0.7: [Edge16]
FEATURE [Part::Fillet] Fillet017
  Base = -> Fillet016
  Edges = 1 edges r=0.7: [Edge11]
FEATURE [Part::Fillet] Fillet018
  Base = -> Fillet017
  Edges = 1 edges r=0.7: [Edge10]
FEATURE [Part::Fillet] Fillet019
  Base = -> Fillet018
  Edges = 1 edges r=1.2: [Edge5]
FEATURE [Part::Fillet] Fillet020
  Base = -> Fillet019
  Edges = 1 edges r=1.2: [Edge12]
FEATURE [Part::Fillet] Fillet021
  Base = -> Fillet020
  Edges = 1 edges r=2: [Edge1]
  Placement = pos=(0.3,0,0) rot=(0,0,1;0rad)
FEATURE [Part::MultiFuse] Fusion040  label="top005"
  Shapes = -> [Cut008,Fillet021]
FEATURE [Part::MultiFuse] Fusion041  label="wireHolder"
  Shapes = -> [Fusion033,Fillet013]
FEATURE [Part::MultiFuse] Fusion042
  Shapes = -> [Fillet007,Fusion041]
FEATURE [Part::MultiFuse] Fusion043  label="wireHolder001"
  Shapes = -> [Fusion042,Fillet010]
FEATURE [Part::MultiFuse] Fusion044  label="wireHolder002"
  Shapes = -> [Fillet006,Fusion037,Fusion043]
FEATURE [Part::Feature] Face026
  shape: bbox 11 x 6 x 2e-07 mm, 1 faces, 0 solids (baked)
FEATURE [Part::Revolution] Revolve026
  Angle = 360
  Axis = (0,1,0)
  Base = (0,0,0)
  FaceMakerClass = Part::FaceMakerBullseye
  Placement = pos=(30.3,-1,19.7) rot=(0,0,1;0rad)
  Solid = false
  Source = -> Face026
  Symmetric = false
FEATURE [Sketcher::SketchObject] Sketch013  label="topSketch006"
  FullyConstrained = true
  sketch-geometry (13):
    g0: LineSegment StartX=117 StartY=19 StartZ=0 EndX=117 EndY=38 EndZ=0
    g1: ArcOfCircle CenterX=98 CenterY=19 CenterZ=0 NormalX=0 NormalY=0 NormalZ=1 AngleXU=0 Radius=19 StartAngle=5.7297 EndAngle=6.28319
    g2: LineSegment StartX=0 StartY=3 StartZ=0 EndX=0 EndY=19 EndZ=0
    g3: LineSegment StartX=19 StartY=38 StartZ=0 EndX=117 EndY=38 EndZ=0
    g4: ArcOfCircle CenterX=19 CenterY=19 CenterZ=0 NormalX=0 NormalY=0 NormalZ=1 AngleXU=0 Radius=19 StartAngle=1.5708 EndAngle=3.14159
    g5: ArcOfCircle CenterX=19 CenterY=19 CenterZ=0 NormalX=0 NormalY=0 NormalZ=1 AngleXU=0 Radius=16 StartAngle=1.5708 EndAngle=3.14159
    g6: ArcOfCircle CenterX=98 CenterY=19 CenterZ=0 NormalX=0 NormalY=0 NormalZ=1 AngleXU=0 Radius=16 StartAngle=5.60905 EndAngle=6.28319
    g7: LineSegment StartX=114 StartY=19 StartZ=0 EndX=114 EndY=35 EndZ=0
    g8: LineSegment StartX=110.5 StartY=9.01251 StartZ=0 EndX=114.163 EndY=9.01251 EndZ=0
    g9: LineSegment StartX=114 StartY=35 StartZ=0 EndX=19 EndY=35 EndZ=0
    g10: LineSegment StartX=0 StartY=3 StartZ=0 EndX=0 EndY=0 EndZ=0
    g11: LineSegment StartX=3 StartY=0 StartZ=0 EndX=0 EndY=0 EndZ=0
    g12: LineSegment StartX=3 StartY=19 StartZ=0 EndX=3 EndY=0 EndZ=0
  constraints (33):
    c: Vertical(g0)
    c: Distance(g0) = 19
    c: Block(g0)
    c: Coincident(g1,g0)
    c: Block(g1)
    c: Vertical(g2)
    c: Block(g2)
    c: Coincident(g3,g0)
    c: Horizontal(g3)
    c: Distance(g3) = 98
    c: Coincident(g4,g3)
    c: Coincident(g4,g2)
    c: Block(g4)
    c: Coincident(g5,g4)
    c: Coincident(g6,g1)
    c: Block(g6)
    c: Block(g5)
    c: Coincident(g7,g6)
    c: Vertical(g7)
    c: Coincident(g8,g6)
    c: Coincident(g8,g1)
    c: Coincident(g9,g7)
    c: Coincident(g9,g5)
    c: Horizontal(g9)
    c: Tangent(g9,g5)
    c: Coincident(g10,g2)
    c: Distance(g10) = 3
    c: Vertical(g10)
    c: Coincident(g11,g10)
    c: Horizontal(g11)
    c: Coincident(g12,g5)
    c: Coincident(g12,g11)
    c: Vertical(g12)
FEATURE [Part::Extrusion] Extrude011  label="top006"
  Base = -> Sketch013
  Dir = (0,0,1)
  DirMode = 2
  FaceMakerClass = Part::FaceMakerBullseye
  LengthFwd = 72
  LengthRev = 0
  Solid = true
  Symmetric = false
FEATURE [Sketcher::SketchObject] Sketch014
  FullyConstrained = true
  MapMode = 3
  Placement = pos=(0,0,0) rot=(1,0,0;1.5708rad)
  Support = -> [Extrude011]
  sketch-geometry (8):
    g0: Circle CenterX=80.351 CenterY=-67.6202 CenterZ=0 NormalX=0 NormalY=0 NormalZ=1 AngleXU=0 Radius=2
    g1: Circle CenterX=80.351 CenterY=-67.6202 CenterZ=0 NormalX=0 NormalY=0 NormalZ=1 AngleXU=0 Radius=3
    g2: Circle CenterX=80.351 CenterY=-4.92017 CenterZ=0 NormalX=0 NormalY=0 NormalZ=1 AngleXU=0 Radius=2
    g3: Circle CenterX=80.351 CenterY=-4.92017 CenterZ=0 NormalX=0 NormalY=0 NormalZ=1 AngleXU=0 Radius=3
    g4: Circle CenterX=23.851 CenterY=-4.92017 CenterZ=0 NormalX=0 NormalY=0 NormalZ=1 AngleXU=0 Radius=2
    g5: Circle CenterX=23.851 CenterY=-4.92017 CenterZ=0 NormalX=0 NormalY=0 NormalZ=1 AngleXU=0 Radius=3
    g6: Circle CenterX=23.851 CenterY=-67.6202 CenterZ=0 NormalX=0 NormalY=0 NormalZ=1 AngleXU=0 Radius=2
    g7: Circle CenterX=23.851 CenterY=-67.6202 CenterZ=0 NormalX=0 NormalY=0 NormalZ=1 AngleXU=0 Radius=3
  constraints (8):
    c: Block(g3)
    c: Block(g2)
    c: Block(g1)
    c: Block(g0)
    c: Block(g6)
    c: Block(g7)
    c: Block(g4)
    c: Block(g5)
FEATURE [Part::Feature] Face027
  shape: bbox 11 x 6 x 2e-07 mm, 1 faces, 0 solids (baked)
FEATURE [Part::Revolution] Revolve027
  Angle = 360
  Axis = (0,1,0)
  Base = (0,0,0)
  FaceMakerClass = Part::FaceMakerBullseye
  Placement = pos=(30.3,-1,51.7) rot=(0,0,1;0rad)
  Solid = false
  Source = -> Face027
  Symmetric = false
FEATURE [Part::Feature] Face028
  shape: bbox 11 x 6 x 2e-07 mm, 1 faces, 0 solids (baked)
FEATURE [Part::Revolution] Revolve028
  Angle = 360
  Axis = (0,1,0)
  Base = (0,0,0)
  FaceMakerClass = Part::FaceMakerBullseye
  Placement = pos=(62.3,-1,19.7) rot=(0,0,1;0rad)
  Solid = false
  Source = -> Face028
  Symmetric = false
FEATURE [Part::Feature] Face029
  shape: bbox 11 x 6 x 2e-07 mm, 1 faces, 0 solids (baked)
FEATURE [Part::Revolution] Revolve029
  Angle = 360
  Axis = (0,1,0)
  Base = (0,0,0)
  FaceMakerClass = Part::FaceMakerBullseye
  Placement = pos=(62.3,-1,51.7) rot=(0,0,1;0rad)
  Solid = false
  Source = -> Face029
  Symmetric = false
FEATURE [Part::Feature] Wire
  shape: bbox 11 x 5.2 x 2e-07 mm, 0 faces, 0 solids (baked)
FEATURE [Part::Revolution] Revolve030
  Angle = 360
  Axis = (0,1,0)
  Base = (0,0,0)
  FaceMakerClass = Part::FaceMakerBullseye
  Placement = pos=(30.3,38,19.7) rot=(0,0,1;0rad)
  Solid = true
  Source = -> Wire
  Symmetric = false
FEATURE [Part::Feature] Wire001
  shape: bbox 11 x 5.2 x 2e-07 mm, 0 faces, 0 solids (baked)
FEATURE [Part::Revolution] Revolve031
  Angle = 360
  Axis = (0,1,0)
  Base = (0,0,0)
  FaceMakerClass = Part::FaceMakerBullseye
  Placement = pos=(30.3,38,51.7) rot=(0,0,1;0rad)
  Solid = true
  Source = -> Wire001
  Symmetric = false
FEATURE [Part::Feature] Wire002
  shape: bbox 11 x 5.2 x 2e-07 mm, 0 faces, 0 solids (baked)
FEATURE [Part::Revolution] Revolve032
  Angle = 360
  Axis = (0,1,0)
  Base = (0,0,0)
  FaceMakerClass = Part::FaceMakerBullseye
  Placement = pos=(62.3,38,51.7) rot=(0,0,1;0rad)
  Solid = true
  Source = -> Wire002
  Symmetric = false
FEATURE [Part::Feature] Wire003
  shape: bbox 11 x 5.2 x 2e-07 mm, 0 faces, 0 solids (baked)
FEATURE [Part::Revolution] Revolve033
  Angle = 360
  Axis = (0,1,0)
  Base = (0,0,0)
  FaceMakerClass = Part::FaceMakerBullseye
  Placement = pos=(62.3,38,19.7) rot=(0,0,1;0rad)
  Solid = true
  Source = -> Wire003
  Symmetric = false
FEATURE [Part::MultiFuse] Fusion045  label="altRandScrewHousing"
  Shapes = -> [Revolve029,Revolve027,Revolve028,Revolve026]
FEATURE [Part::MultiFuse] Fusion046  label="fanScrewHousing"
  Shapes = -> [Revolve033,Revolve032,Revolve031,Revolve030]
FEATURE [Sketcher::SketchObject] Sketch015
  FullyConstrained = true
  sketch-geometry (17):
    g0: Circle CenterX=-3.5 CenterY=23.5 CenterZ=0 NormalX=0 NormalY=0 NormalZ=1 AngleXU=0 Radius=1
    g1: Circle CenterX=-1 CenterY=15.25 CenterZ=0 NormalX=0 NormalY=0 NormalZ=1 AngleXU=0 Radius=1
    g2: Circle CenterX=-3.5 CenterY=7 CenterZ=0 NormalX=0 NormalY=0 NormalZ=1 AngleXU=0 Radius=1
    g3: BSplineCurve PolesCount=3 KnotsCount=2 Degree=2 IsPeriodic=0
    g4: GeomPoint X=-3.5 Y=23.5 Z=0
    g5: GeomPoint X=-3.5 Y=7 Z=0
    g6: Circle CenterX=-4.8 CenterY=30.5 CenterZ=0 NormalX=0 NormalY=0 NormalZ=1 AngleXU=0 Radius=1
    g7: Circle CenterX=-3.5 CenterY=30.5 CenterZ=0 NormalX=0 NormalY=0 NormalZ=1 AngleXU=0 Radius=1
    g8: Circle CenterX=-3.5 CenterY=29.2 CenterZ=0 NormalX=0 NormalY=0 NormalZ=1 AngleXU=0 Radius=1
    g9: BSplineCurve PolesCount=3 KnotsCount=2 Degree=2 IsPeriodic=0
    g10: GeomPoint X=-4.8 Y=30.5 Z=0
    g11: GeomPoint X=-3.5 Y=29.2 Z=0
    g12: LineSegment StartX=-3.5 StartY=29.2 StartZ=0 EndX=-3.5 EndY=23.5 EndZ=0
    g13: LineSegment StartX=-4.8 StartY=30.5 StartZ=0 EndX=0 EndY=30.5 EndZ=0
    g14: LineSegment StartX=-3.5 StartY=0.3 StartZ=0 EndX=0 EndY=0.3 EndZ=0
    g15: LineSegment StartX=-3.5 StartY=0.3 StartZ=0 EndX=-3.5 EndY=7 EndZ=0
    g16: LineSegment StartX=0 StartY=0.3 StartZ=0 EndX=0 EndY=30.5 EndZ=0
  constraints (33):
    c: Weight(g0) = 1
    c: Equal(g0,g1)
    c: Equal(g0,g2)
    c: InternalAlignment(g0,g3)
    c: InternalAlignment(g1,g3)
    c: InternalAlignment(g2,g3)
    c: InternalAlignment(g4,g3)
    c: InternalAlignment(g5,g3)
    c: Block(g3)
    c: Weight(g6) = 1
    c: Equal(g6,g7)
    c: Equal(g6,g8)
    c: InternalAlignment(g6,g9)
    c: InternalAlignment(g7,g9)
    c: InternalAlignment(g8,g9)
    c: InternalAlignment(g10,g9)
    c: InternalAlignment(g11,g9)
    c: Block(g9)
    c: Coincident(g12,g9)
    c: Coincident(g12,g3)
    c: Vertical(g12)
    c: Coincident(g13,g9)
    c: Horizontal(g13)
    c: Distance(g13) = 4.8
    c: Horizontal(g14)
    c: Block(g14)
    c: Coincident(g15,g14)
    c: Coincident(g15,g3)
    c: Vertical(g15)
    c: Coincident(g16,g14)
    c: Coincident(g16,g13)
    c: Vertical(g16)
    c: Tangent(g16,g1)
FEATURE [Sketcher::SketchObject] Sketch016
  FullyConstrained = true
  sketch-geometry (16):
    g0: Circle CenterX=-3.5 CenterY=23.5 CenterZ=0 NormalX=0 NormalY=0 NormalZ=1 AngleXU=0 Radius=1
    g1: Circle CenterX=-1 CenterY=15.25 CenterZ=0 NormalX=0 NormalY=0 NormalZ=1 AngleXU=0 Radius=1
    g2: Circle CenterX=-3.5 CenterY=7 CenterZ=0 NormalX=0 NormalY=0 NormalZ=1 AngleXU=0 Radius=1
    g3: BSplineCurve PolesCount=3 KnotsCount=2 Degree=2 IsPeriodic=0
    g4: GeomPoint X=-3.5 Y=23.5 Z=0
    g5: GeomPoint X=-3.5 Y=7 Z=0
    g6: LineSegment StartX=-3.5 StartY=28.2 StartZ=0 EndX=-3.5 EndY=23.5 EndZ=0
    g7: LineSegment StartX=0 StartY=29.5 StartZ=0 EndX=0 EndY=30 EndZ=0
    g8: LineSegment StartX=-3.5 StartY=28.2 StartZ=0 EndX=-3.5 EndY=30 EndZ=0
    g9: LineSegment StartX=0 StartY=30 StartZ=0 EndX=0 EndY=30.5 EndZ=0
    g10: LineSegment StartX=0 StartY=30.5 StartZ=0 EndX=-3.5 EndY=30.5 EndZ=0
    g11: LineSegment StartX=-3.5 StartY=30.5 StartZ=0 EndX=-3.5 EndY=30 EndZ=0
    g12: LineSegment StartX=0 StartY=29.5 StartZ=0 EndX=0 EndY=5 EndZ=0
    g13: LineSegment StartX=-3.5 StartY=0.3 StartZ=0 EndX=-3.5 EndY=7 EndZ=0
    g14: LineSegment StartX=-3.5 StartY=0.3 StartZ=0 EndX=0 EndY=0.3 EndZ=0
    g15: LineSegment StartX=0 StartY=5 StartZ=0 EndX=0 EndY=0.3 EndZ=0
  constraints (39):
    c: Weight(g0) = 1
    c: Equal(g0,g1)
    c: Equal(g0,g2)
    c: InternalAlignment(g0,g3)
    c: InternalAlignment(g1,g3)
    c: InternalAlignment(g2,g3)
    c: InternalAlignment(g4,g3)
    c: InternalAlignment(g5,g3)
    c: Block(g3)
    c: Coincident(g6,g3)
    c: Vertical(g6)
    c: Vertical(g7)
    c: Distance(g7) = 0.5
    c: Coincident(g8,g6)
    c: Vertical(g8)
    c: Block(g6)
    c: Block(g7)
    c: Vertical(g9)
    c: Equal(g7,g9) = 0.5
    c: Block(g9)
    c: Coincident(g9,g7)
    c: Horizontal(g10)
    c: Coincident(g10,g9)
    c: Coincident(g11,g10)
    c: Coincident(g11,g8)
    c: Vertical(g11)
    c: Block(g11)
    c: Coincident(g12,g7)
    c: Vertical(g12)
    c: Coincident(g13,g3)
    c: Vertical(g13)
    c: Distance(g13) = 6.7
    c: Coincident(g14,g13)
    c: Horizontal(g14)
    c: Block(g14)
    c: Coincident(g15,g12)
    c: Coincident(g15,g14)
    c: Vertical(g15)
    c: Block(g15)
FEATURE [Sketcher::SketchObject] Sketch017
  FullyConstrained = true
  sketch-geometry (11):
    g0: LineSegment StartX=-3.5 StartY=1e-16 StartZ=0 EndX=-1.6 EndY=1e-16 EndZ=0
    g1: LineSegment StartX=-1.6 StartY=1e-16 StartZ=0 EndX=-1.6 EndY=1.5 EndZ=0
    g2: LineSegment StartX=-3.5 StartY=1.5 StartZ=0 EndX=-1.6 EndY=1.5 EndZ=0
    g3: LineSegment StartX=-3.5 StartY=1e-16 StartZ=0 EndX=-4.8 EndY=1e-16 EndZ=0
    g4: Circle CenterX=-3.5 CenterY=1.3 CenterZ=0 NormalX=0 NormalY=0 NormalZ=1 AngleXU=0 Radius=1
    g5: Circle CenterX=-3.5 CenterY=1e-16 CenterZ=0 NormalX=0 NormalY=0 NormalZ=1 AngleXU=0 Radius=1
    g6: Circle CenterX=-4.8 CenterY=1e-16 CenterZ=0 NormalX=0 NormalY=0 NormalZ=1 AngleXU=0 Radius=1
    g7: BSplineCurve PolesCount=3 KnotsCount=2 Degree=2 IsPeriodic=0
    g8: GeomPoint X=-3.5 Y=1.3 Z=0
    g9: GeomPoint X=-4.8 Y=1e-16 Z=0
    g10: LineSegment StartX=-3.5 StartY=1.3 StartZ=0 EndX=-3.5 EndY=1.5 EndZ=0
  constraints (24):
    c: Horizontal(g0)
    c: Distance(g0) = 1.9
    c: Block(g0)
    c: Coincident(g1,g0)
    c: Vertical(g1)
    c: Coincident(g2,g1)
    c: Horizontal(g2)
    c: Coincident(g3,g0)
    c: Horizontal(g3)
    c: Distance(g3) = 1.3
    c: Weight(g4) = 1
    c: Equal(g4,g5)
    c: Coincident(g5,g0)
    c: Equal(g4,g6)
    c: Coincident(g7,g3)
    c: InternalAlignment(g4,g7)
    c: InternalAlignment(g5,g7)
    c: InternalAlignment(g6,g7)
    c: InternalAlignment(g8,g7)
    c: InternalAlignment(g9,g7)
    c: Coincident(g10,g7)
    c: Coincident(g10,g2)
    c: Vertical(g10)
    c: Block(g10)
FEATURE [Part::Feature] Face035
  shape: bbox 3.2 x 1.5 x 2e-07 mm, 1 faces, 0 solids (baked)
FEATURE [Part::Revolution] Revolve039  label="backCaseScrewRetainer"
  Angle = 360
  Axis = (0,1,0)
  Base = (0,0,0)
  FaceMakerClass = Part::FaceMakerBullseye
  Placement = pos=(12.5,3,62) rot=(0,0,1;0rad)
  Solid = false
  Source = -> Face035
  Symmetric = false
FEATURE [Part::Feature] Face036
  shape: bbox 3.2 x 1.5 x 2e-07 mm, 1 faces, 0 solids (baked)
FEATURE [Part::Feature] Face039
  shape: bbox 4.8 x 30.2 x 2e-07 mm, 1 faces, 0 solids (baked)
FEATURE [Part::Revolution] Revolve043  label="frontCaseScrewPost002"
  Angle = 360
  Axis = (0,1,0)
  Base = (0,0,0)
  FaceMakerClass = Part::FaceMakerBullseye
  Placement = pos=(89.5,4.5,3.5) rot=(0,0,1;0rad)
  Solid = false
  Source = -> Face039
  Symmetric = false
FEATURE [Part::Feature] Face042
  shape: bbox 4.8 x 30.2 x 2e-07 mm, 1 faces, 0 solids (baked)
FEATURE [Part::Revolution] Revolve046  label="frontCaseScrewPost003"
  Angle = 360
  Axis = (0,1,0)
  Base = (0,0,0)
  FaceMakerClass = Part::FaceMakerBullseye
  Placement = pos=(89.5,4.5,68.5) rot=(0,0,1;0rad)
  Solid = false
  Source = -> Face042
  Symmetric = false
FEATURE [Part::Feature] Face043
  shape: bbox 3.2 x 1.5 x 2e-07 mm, 1 faces, 0 solids (baked)
FEATURE [Part::Revolution] Revolve047  label="frontCaseScrewRetainer002"
  Angle = 360
  Axis = (0,1,0)
  Base = (0,0,0)
  FaceMakerClass = Part::FaceMakerBullseye
  Placement = pos=(89.5,3,68.5) rot=(0,0,1;0rad)
  Solid = false
  Source = -> Face043
  Symmetric = false
FEATURE [Part::Feature] Face044
  shape: bbox 3.2 x 1.5 x 2e-07 mm, 1 faces, 0 solids (baked)
FEATURE [Part::Revolution] Revolve048  label="frontCaseScrewRetainer003"
  Angle = 360
  Axis = (0,1,0)
  Base = (0,0,0)
  FaceMakerClass = Part::FaceMakerBullseye
  Placement = pos=(89.5,3,3.5) rot=(0,0,1;0rad)
  Solid = false
  Source = -> Face044
  Symmetric = false
FEATURE [App::MeasureDistance] Distance002  label="Distance: 1.67 mm"
  Distance = 1.66921
  P1 = (99.2361,4.7524,71.7)
  P2 = (99.2347,6.42161,71.7)
FEATURE [Sketcher::SketchObject] Sketch018
  FullyConstrained = true
  sketch-geometry (7):
    g0: LineSegment StartX=0 StartY=0 StartZ=0 EndX=0 EndY=6 EndZ=0
    g1: Circle CenterX=0 CenterY=0 CenterZ=0 NormalX=0 NormalY=0 NormalZ=1 AngleXU=0 Radius=1
    g2: Circle CenterX=8 CenterY=6 CenterZ=0 NormalX=0 NormalY=0 NormalZ=1 AngleXU=0 Radius=1
    g3: BSplineCurve PolesCount=3 KnotsCount=2 Degree=2 IsPeriodic=0
    g4: GeomPoint X=0 Y=0 Z=0
    g5: GeomPoint X=8 Y=6 Z=0
    g6: LineSegment StartX=0 StartY=6 StartZ=0 EndX=8 EndY=6 EndZ=0
  constraints (14):
    c: Coincident(g0,g-1)
    c: Distance(g0) = 6
    c: Vertical(g0)
    c: Coincident(g3,g0)
    c: Weight(g1) = 1
    c: Equal(g1,g2)
    c: InternalAlignment(g1,g3)
    c: InternalAlignment(g2,g3)
    c: InternalAlignment(g4,g3)
    c: InternalAlignment(g5,g3)
    c: Block(g3)
    c: Coincident(g6,g0)
    c: Coincident(g6,g3)
    c: Horizontal(g6)
FEATURE [Part::Extrusion] Extrude012  label="caseScrewPillarBracket"
  Base = -> Sketch018
  Dir = (0,0,1)
  DirMode = 2
  FaceMakerClass = Part::FaceMakerBullseye
  LengthFwd = 2.4
  LengthRev = 0
  Placement = pos=(15.76,29,8.8) rot=(0,1,0;0rad)
  Solid = true
  Symmetric = false
FEATURE [Sketcher::SketchObject] Sketch019
  FullyConstrained = true
  sketch-geometry (7):
    g0: LineSegment StartX=0 StartY=0 StartZ=0 EndX=0 EndY=6 EndZ=0
    g1: Circle CenterX=0 CenterY=0 CenterZ=0 NormalX=0 NormalY=0 NormalZ=1 AngleXU=0 Radius=1
    g2: Circle CenterX=8 CenterY=6 CenterZ=0 NormalX=0 NormalY=0 NormalZ=1 AngleXU=0 Radius=1
    g3: BSplineCurve PolesCount=3 KnotsCount=2 Degree=2 IsPeriodic=0
    g4: GeomPoint X=0 Y=0 Z=0
    g5: GeomPoint X=8 Y=6 Z=0
    g6: LineSegment StartX=0 StartY=6 StartZ=0 EndX=8 EndY=6 EndZ=0
  constraints (14):
    c: Coincident(g0,g-1)
    c: Distance(g0) = 6
    c: Vertical(g0)
    c: Coincident(g3,g0)
    c: Weight(g1) = 1
    c: Equal(g1,g2)
    c: InternalAlignment(g1,g3)
    c: InternalAlignment(g2,g3)
    c: InternalAlignment(g4,g3)
    c: InternalAlignment(g5,g3)
    c: Block(g3)
    c: Coincident(g6,g0)
    c: Coincident(g6,g3)
    c: Horizontal(g6)
FEATURE [Part::Extrusion] Extrude013  label="caseScrewPillarBracket001"
  Base = -> Sketch019
  Dir = (0,0,1)
  DirMode = 2
  FaceMakerClass = Part::FaceMakerBullseye
  LengthFwd = 2.4
  LengthRev = 0
  Placement = pos=(15.76,29,60.8) rot=(0,0,1;0rad)
  Solid = true
  Symmetric = false
FEATURE [Sketcher::SketchObject] Sketch020
  FullyConstrained = true
  sketch-geometry (7):
    g0: LineSegment StartX=0 StartY=0 StartZ=0 EndX=0 EndY=6 EndZ=0
    g1: Circle CenterX=0 CenterY=0 CenterZ=0 NormalX=0 NormalY=0 NormalZ=1 AngleXU=0 Radius=1
    g2: Circle CenterX=8 CenterY=6 CenterZ=0 NormalX=0 NormalY=0 NormalZ=1 AngleXU=0 Radius=1
    g3: BSplineCurve PolesCount=3 KnotsCount=2 Degree=2 IsPeriodic=0
    g4: GeomPoint X=0 Y=0 Z=0
    g5: GeomPoint X=8 Y=6 Z=0
    g6: LineSegment StartX=0 StartY=6 StartZ=0 EndX=8 EndY=6 EndZ=0
  constraints (14):
    c: Coincident(g0,g-1)
    c: Distance(g0) = 6
    c: Vertical(g0)
    c: Coincident(g3,g0)
    c: Weight(g1) = 1
    c: Equal(g1,g2)
    c: InternalAlignment(g1,g3)
    c: InternalAlignment(g2,g3)
    c: InternalAlignment(g4,g3)
    c: InternalAlignment(g5,g3)
    c: Block(g3)
    c: Coincident(g6,g0)
    c: Coincident(g6,g3)
    c: Horizontal(g6)
FEATURE [Part::Extrusion] Extrude014  label="caseScrewPillarBracket002"
  Base = -> Sketch020
  Dir = (0,0,1)
  DirMode = 2
  FaceMakerClass = Part::FaceMakerBullseye
  LengthFwd = 2.4
  LengthRev = 0
  Placement = pos=(13.7,29,13.26) rot=(0,-1,0;1.5708rad)
  Solid = true
  Symmetric = false
FEATURE [Sketcher::SketchObject] Sketch021
  FullyConstrained = true
  sketch-geometry (7):
    g0: LineSegment StartX=0 StartY=0 StartZ=0 EndX=0 EndY=6 EndZ=0
    g1: Circle CenterX=0 CenterY=0 CenterZ=0 NormalX=0 NormalY=0 NormalZ=1 AngleXU=0 Radius=1
    g2: Circle CenterX=8 CenterY=6 CenterZ=0 NormalX=0 NormalY=0 NormalZ=1 AngleXU=0 Radius=1
    g3: BSplineCurve PolesCount=3 KnotsCount=2 Degree=2 IsPeriodic=0
    g4: GeomPoint X=0 Y=0 Z=0
    g5: GeomPoint X=8 Y=6 Z=0
    g6: LineSegment StartX=0 StartY=6 StartZ=0 EndX=8 EndY=6 EndZ=0
  constraints (14):
    c: Coincident(g0,g-1)
    c: Distance(g0) = 6
    c: Vertical(g0)
    c: Coincident(g3,g0)
    c: Weight(g1) = 1
    c: Equal(g1,g2)
    c: InternalAlignment(g1,g3)
    c: InternalAlignment(g2,g3)
    c: InternalAlignment(g4,g3)
    c: InternalAlignment(g5,g3)
    c: Block(g3)
    c: Coincident(g6,g0)
    c: Coincident(g6,g3)
    c: Horizontal(g6)
FEATURE [Part::Extrusion] Extrude015  label="caseScrewPillarBracket003"
  Base = -> Sketch021
  Dir = (0,0,1)
  DirMode = 2
  FaceMakerClass = Part::FaceMakerBullseye
  LengthFwd = 2.4
  LengthRev = 0
  Placement = pos=(11.3,29,58.74) rot=(0,1,0;1.5708rad)
  Solid = true
  Symmetric = false
FEATURE [Sketcher::SketchObject] Sketch022
  FullyConstrained = true
  sketch-geometry (7):
    g0: LineSegment StartX=0 StartY=0 StartZ=0 EndX=0 EndY=6 EndZ=0
    g1: Circle CenterX=0 CenterY=0 CenterZ=0 NormalX=0 NormalY=0 NormalZ=1 AngleXU=0 Radius=1
    g2: Circle CenterX=8 CenterY=6 CenterZ=0 NormalX=0 NormalY=0 NormalZ=1 AngleXU=0 Radius=1
    g3: BSplineCurve PolesCount=3 KnotsCount=2 Degree=2 IsPeriodic=0
    g4: GeomPoint X=0 Y=0 Z=0
    g5: GeomPoint X=8 Y=6 Z=0
    g6: LineSegment StartX=0 StartY=6 StartZ=0 EndX=8 EndY=6 EndZ=0
  constraints (14):
    c: Coincident(g0,g-1)
    c: Distance(g0) = 6
    c: Vertical(g0)
    c: Coincident(g3,g0)
    c: Weight(g1) = 1
    c: Equal(g1,g2)
    c: InternalAlignment(g1,g3)
    c: InternalAlignment(g2,g3)
    c: InternalAlignment(g4,g3)
    c: InternalAlignment(g5,g3)
    c: Block(g3)
    c: Coincident(g6,g0)
    c: Coincident(g6,g3)
    c: Horizontal(g6)
FEATURE [Part::Extrusion] Extrude016  label="caseScrewPillarBracket004"
  Base = -> Sketch022
  Dir = (0,0,1)
  DirMode = 2
  FaceMakerClass = Part::FaceMakerBullseye
  LengthFwd = 2.4
  LengthRev = 0
  Placement = pos=(88.3,29,65.23) rot=(0,1,0;1.5708rad)
  Solid = true
  Symmetric = false
FEATURE [Sketcher::SketchObject] Sketch023
  FullyConstrained = true
  sketch-geometry (7):
    g0: LineSegment StartX=0 StartY=0 StartZ=0 EndX=0 EndY=6 EndZ=0
    g1: Circle CenterX=0 CenterY=0 CenterZ=0 NormalX=0 NormalY=0 NormalZ=1 AngleXU=0 Radius=1
    g2: Circle CenterX=8 CenterY=6 CenterZ=0 NormalX=0 NormalY=0 NormalZ=1 AngleXU=0 Radius=1
    g3: BSplineCurve PolesCount=3 KnotsCount=2 Degree=2 IsPeriodic=0
    g4: GeomPoint X=0 Y=0 Z=0
    g5: GeomPoint X=8 Y=6 Z=0
    g6: LineSegment StartX=0 StartY=6 StartZ=0 EndX=8 EndY=6 EndZ=0
  constraints (14):
    c: Coincident(g0,g-1)
    c: Distance(g0) = 6
    c: Vertical(g0)
    c: Coincident(g3,g0)
    c: Weight(g1) = 1
    c: Equal(g1,g2)
    c: InternalAlignment(g1,g3)
    c: InternalAlignment(g2,g3)
    c: InternalAlignment(g4,g3)
    c: InternalAlignment(g5,g3)
    c: Block(g3)
    c: Coincident(g6,g0)
    c: Coincident(g6,g3)
    c: Horizontal(g6)
FEATURE [Part::Extrusion] Extrude017  label="caseScrewPillarBracket005"
  Base = -> Sketch023
  Dir = (0,0,1)
  DirMode = 2
  FaceMakerClass = Part::FaceMakerBullseye
  LengthFwd = 2.4
  LengthRev = 0
  Placement = pos=(90.7,29,6.77) rot=(0,-1,0;1.5708rad)
  Solid = true
  Symmetric = false
FEATURE [Sketcher::SketchObject] Sketch024
  FullyConstrained = true
  sketch-geometry (7):
    g0: LineSegment StartX=0 StartY=0 StartZ=0 EndX=0 EndY=6 EndZ=0
    g1: Circle CenterX=0 CenterY=0 CenterZ=0 NormalX=0 NormalY=0 NormalZ=1 AngleXU=0 Radius=1
    g2: Circle CenterX=8 CenterY=6 CenterZ=0 NormalX=0 NormalY=0 NormalZ=1 AngleXU=0 Radius=1
    g3: BSplineCurve PolesCount=3 KnotsCount=2 Degree=2 IsPeriodic=0
    g4: GeomPoint X=0 Y=0 Z=0
    g5: GeomPoint X=8 Y=6 Z=0
    g6: LineSegment StartX=0 StartY=6 StartZ=0 EndX=8 EndY=6 EndZ=0
  constraints (14):
    c: Coincident(g0,g-1)
    c: Distance(g0) = 6
    c: Vertical(g0)
    c: Coincident(g3,g0)
    c: Weight(g1) = 1
    c: Equal(g1,g2)
    c: InternalAlignment(g1,g3)
    c: InternalAlignment(g2,g3)
    c: InternalAlignment(g4,g3)
    c: InternalAlignment(g5,g3)
    c: Block(g3)
    c: Coincident(g6,g0)
    c: Coincident(g6,g3)
    c: Horizontal(g6)
FEATURE [Part::Extrusion] Extrude018  label="caseScrewPillarBracket006"
  Base = -> Sketch024
  Dir = (0,0,1)
  DirMode = 2
  FaceMakerClass = Part::FaceMakerBullseye
  LengthFwd = 2.4
  LengthRev = 0
  Placement = pos=(103.7,29,6.77) rot=(0,-1,0;1.5708rad)
  Solid = true
  Symmetric = false
FEATURE [Sketcher::SketchObject] Sketch025
  FullyConstrained = true
  sketch-geometry (7):
    g0: LineSegment StartX=0 StartY=0 StartZ=0 EndX=0 EndY=6 EndZ=0
    g1: Circle CenterX=0 CenterY=0 CenterZ=0 NormalX=0 NormalY=0 NormalZ=1 AngleXU=0 Radius=1
    g2: Circle CenterX=8 CenterY=6 CenterZ=0 NormalX=0 NormalY=0 NormalZ=1 AngleXU=0 Radius=1
    g3: BSplineCurve PolesCount=3 KnotsCount=2 Degree=2 IsPeriodic=0
    g4: GeomPoint X=0 Y=0 Z=0
    g5: GeomPoint X=8 Y=6 Z=0
    g6: LineSegment StartX=0 StartY=6 StartZ=0 EndX=8 EndY=6 EndZ=0
  constraints (14):
    c: Coincident(g0,g-1)
    c: Distance(g0) = 6
    c: Vertical(g0)
    c: Coincident(g3,g0)
    c: Weight(g1) = 1
    c: Equal(g1,g2)
    c: InternalAlignment(g1,g3)
    c: InternalAlignment(g2,g3)
    c: InternalAlignment(g4,g3)
    c: InternalAlignment(g5,g3)
    c: Block(g3)
    c: Coincident(g6,g0)
    c: Coincident(g6,g3)
    c: Horizontal(g6)
FEATURE [Part::Extrusion] Extrude019  label="caseScrewPillarBracket007"
  Base = -> Sketch025
  Dir = (0,0,1)
  DirMode = 2
  FaceMakerClass = Part::FaceMakerBullseye
  LengthFwd = 2.4
  LengthRev = 0
  Placement = pos=(101.3,29,65.23) rot=(0,1,0;1.5708rad)
  Solid = true
  Symmetric = false
FEATURE [Part::Box] Box011  label="frontCaseScrewPillarBracket"
  AttacherType = Attacher::AttachEngine3D
  Height = 2.4
  Length = 16
  Placement = pos=(87,28,2.3) rot=(0,0,1;0rad)
  Width = 7
FEATURE [Part::Box] Box012  label="frontCaseScrewPillarBracket001"
  AttacherType = Attacher::AttachEngine3D
  Height = 2.4
  Length = 16
  Placement = pos=(87,28,67.3) rot=(0,0,1;0rad)
  Width = 7
FEATURE [Sketcher::SketchObject] Sketch026
  FullyConstrained = true
  sketch-geometry (17):
    g0: Circle CenterX=-3.5 CenterY=23.5 CenterZ=0 NormalX=0 NormalY=0 NormalZ=1 AngleXU=0 Radius=1
    g1: Circle CenterX=-1 CenterY=15.25 CenterZ=0 NormalX=0 NormalY=0 NormalZ=1 AngleXU=0 Radius=1
    g2: Circle CenterX=-3.5 CenterY=7 CenterZ=0 NormalX=0 NormalY=0 NormalZ=1 AngleXU=0 Radius=1
    g3: BSplineCurve PolesCount=3 KnotsCount=2 Degree=2 IsPeriodic=0
    g4: GeomPoint X=-3.5 Y=23.5 Z=0
    g5: GeomPoint X=-3.5 Y=7 Z=0
    g6: Circle CenterX=-4.8 CenterY=30.5 CenterZ=0 NormalX=0 NormalY=0 NormalZ=1 AngleXU=0 Radius=1
    g7: Circle CenterX=-3.5 CenterY=30.5 CenterZ=0 NormalX=0 NormalY=0 NormalZ=1 AngleXU=0 Radius=1
    g8: Circle CenterX=-3.5 CenterY=29.2 CenterZ=0 NormalX=0 NormalY=0 NormalZ=1 AngleXU=0 Radius=1
    g9: BSplineCurve PolesCount=3 KnotsCount=2 Degree=2 IsPeriodic=0
    g10: GeomPoint X=-4.8 Y=30.5 Z=0
    g11: GeomPoint X=-3.5 Y=29.2 Z=0
    g12: LineSegment StartX=-3.5 StartY=29.2 StartZ=0 EndX=-3.5 EndY=23.5 EndZ=0
    g13: LineSegment StartX=-4.8 StartY=30.5 StartZ=0 EndX=0 EndY=30.5 EndZ=0
    g14: LineSegment StartX=-3.5 StartY=5 StartZ=0 EndX=-3.5 EndY=7 EndZ=0
    g15: LineSegment StartX=0 StartY=5 StartZ=0 EndX=0 EndY=30.5 EndZ=0
    g16: LineSegment StartX=-3.5 StartY=5 StartZ=0 EndX=0 EndY=5 EndZ=0
  constraints (33):
    c: Weight(g0) = 1
    c: Equal(g0,g1)
    c: Equal(g0,g2)
    c: InternalAlignment(g0,g3)
    c: InternalAlignment(g1,g3)
    c: InternalAlignment(g2,g3)
    c: InternalAlignment(g4,g3)
    c: InternalAlignment(g5,g3)
    c: Block(g3)
    c: Weight(g6) = 1
    c: Equal(g6,g7)
    c: Equal(g6,g8)
    c: InternalAlignment(g6,g9)
    c: InternalAlignment(g7,g9)
    c: InternalAlignment(g8,g9)
    c: InternalAlignment(g10,g9)
    c: InternalAlignment(g11,g9)
    c: Block(g9)
    c: Coincident(g12,g9)
    c: Coincident(g12,g3)
    c: Vertical(g12)
    c: Coincident(g13,g9)
    c: Horizontal(g13)
    c: Distance(g13) = 4.8
    c: Coincident(g14,g3)
    c: Vertical(g14)
    c: Coincident(g15,g13)
    c: Vertical(g15)
    c: Tangent(g15,g1)
    c: Distance(g14) = 2
    c: Coincident(g16,g14)
    c: Horizontal(g16)
    c: Coincident(g15,g16)
FEATURE [Part::Feature] Face050
  shape: bbox 4.8 x 25.5 x 2e-07 mm, 1 faces, 0 solids (baked)
FEATURE [Part::Revolution] Revolve054  label="moreFrontCaseScrewPost001"
  Angle = 360
  Axis = (0,1,0)
  Base = (0,0,0)
  FaceMakerClass = Part::FaceMakerBullseye
  Placement = pos=(102.5,4.5,3.5) rot=(0,0,1;0rad)
  Solid = false
  Source = -> Face050
  Symmetric = false
FEATURE [Part::Feature] Face051
  shape: bbox 4.8 x 25.5 x 2e-07 mm, 1 faces, 0 solids (baked)
FEATURE [Part::Revolution] Revolve055  label="moreFrontCaseScrewPost002"
  Angle = 360
  Axis = (0,1,0)
  Base = (0,0,0)
  FaceMakerClass = Part::FaceMakerBullseye
  Placement = pos=(102.5,4.5,68.5) rot=(0,0,1;0rad)
  Solid = false
  Source = -> Face051
  Symmetric = false
FEATURE [Sketcher::SketchObject] Sketch027
  FullyConstrained = true
  sketch-geometry (10):
    g0: LineSegment StartX=-1.6 StartY=4.7 StartZ=0 EndX=-1.6 EndY=1.7 EndZ=0
    g1: LineSegment StartX=-3.5 StartY=4.7 StartZ=0 EndX=-1.6 EndY=4.7 EndZ=0
    g2: LineSegment StartX=-1.6 StartY=1.7 StartZ=0 EndX=-1.6 EndY=1.5 EndZ=0
    g3: LineSegment StartX=-1.6 StartY=1.5 StartZ=0 EndX=-5.2 EndY=1.5 EndZ=0
    g4: Circle CenterX=-3.5 CenterY=4.7 CenterZ=0 NormalX=0 NormalY=0 NormalZ=1 AngleXU=0 Radius=1
    g5: Circle CenterX=-3.59627 CenterY=2.99743 CenterZ=0 NormalX=0 NormalY=0 NormalZ=1 AngleXU=0 Radius=1
    g6: Circle CenterX=-5.2 CenterY=1.5 CenterZ=0 NormalX=0 NormalY=0 NormalZ=1 AngleXU=0 Radius=1
    g7: BSplineCurve PolesCount=3 KnotsCount=2 Degree=2 IsPeriodic=0
    g8: GeomPoint X=-3.5 Y=4.7 Z=0
    g9: GeomPoint X=-5.2 Y=1.5 Z=0
  constraints (23):
    c: Vertical(g0)
    c: Distance(g0) = 3
    c: Coincident(g1,g0)
    c: Horizontal(g1)
    c: Block(g0)
    c: Block(g1)
    c: Coincident(g2,g0)
    c: Vertical(g2)
    c: Distance(g2) = 0.2
    c: Coincident(g3,g2)
    c: Horizontal(g3)
    c: Block(g3)
    c: Coincident(g7,g1)
    c: Weight(g4) = 1
    c: Equal(g4,g5)
    c: Equal(g4,g6)
    c: Coincident(g7,g3)
    c: InternalAlignment(g4,g7)
    c: InternalAlignment(g5,g7)
    c: InternalAlignment(g6,g7)
    c: InternalAlignment(g8,g7)
    c: InternalAlignment(g9,g7)
    c: Block(g7)
FEATURE [Sketcher::SketchObject] Sketch028
  FullyConstrained = true
  sketch-geometry (18):
    g0: LineSegment StartX=0 StartY=3e-16 StartZ=0 EndX=0 EndY=1.7 EndZ=0
    g1: LineSegment StartX=-3.5 StartY=0 StartZ=0 EndX=-3.5 EndY=0.9 EndZ=0
    g2: Circle CenterX=-2.7 CenterY=1.7 CenterZ=0 NormalX=0 NormalY=0 NormalZ=1 AngleXU=0 Radius=1
    g3: Circle CenterX=-3.5 CenterY=1.7 CenterZ=0 NormalX=0 NormalY=0 NormalZ=1 AngleXU=0 Radius=1
    g4: Circle CenterX=-3.5 CenterY=0.9 CenterZ=0 NormalX=0 NormalY=0 NormalZ=1 AngleXU=0 Radius=1
    g5: BSplineCurve PolesCount=3 KnotsCount=2 Degree=2 IsPeriodic=0
    g6: GeomPoint X=-2.7 Y=1.7 Z=0
    g7: GeomPoint X=-3.5 Y=0.9 Z=0
    g8: LineSegment StartX=-3.5 StartY=0 StartZ=0 EndX=-3.5 EndY=-7 EndZ=0
    g9: LineSegment StartX=0 StartY=3e-16 StartZ=0 EndX=0 EndY=-7 EndZ=0
    g10: LineSegment StartX=-3.5 StartY=-7 StartZ=0 EndX=0 EndY=-7 EndZ=0
    g11: LineSegment StartX=-2.7 StartY=1.7 StartZ=0 EndX=-1.6 EndY=1.7 EndZ=0
    g12: LineSegment StartX=0 StartY=1.7 StartZ=0 EndX=0 EndY=4.5 EndZ=0
    g13: LineSegment StartX=0 StartY=4.5 StartZ=0 EndX=0 EndY=10.8 EndZ=0
    g14: LineSegment StartX=0 StartY=10.8 StartZ=0 EndX=-2 EndY=10.8 EndZ=0
    g15: LineSegment StartX=-1.6 StartY=4.7 StartZ=0 EndX=-1.6 EndY=1.7 EndZ=0
    g16: LineSegment StartX=-1.6 StartY=4.7 StartZ=0 EndX=-2 EndY=4.7 EndZ=0
    g17: LineSegment StartX=-2 StartY=4.7 StartZ=0 EndX=-2 EndY=10.8 EndZ=0
  constraints (44):
    c: Vertical(g0)
    c: Vertical(g1)
    c: Distance(g1) = 0.9
    c: Block(g0)
    c: Distance(g0) = 1.7
    c: Weight(g2) = 1
    c: Equal(g2,g3)
    c: Equal(g2,g4)
    c: Coincident(g5,g1)
    c: InternalAlignment(g2,g5)
    c: InternalAlignment(g3,g5)
    c: InternalAlignment(g4,g5)
    c: InternalAlignment(g6,g5)
    c: InternalAlignment(g7,g5)
    c: Block(g5)
    c: Coincident(g8,g1)
    c: Vertical(g8)
    c: Distance(g8) = 7
    c: Vertical(g9)
    c: Equal(g8,g9) = 7
    c: Coincident(g9,g0)
    c: Coincident(g10,g8)
    c: Coincident(g10,g9)
    c: Horizontal(g10)
    c: Coincident(g11,g5)
    c: Horizontal(g11)
    c: Coincident(g12,g0)
    c: Vertical(g12)
    c: Distance(g12) = 2.8
    c: Coincident(g13,g12)
    c: Vertical(g13)
    c: Distance(g13) = 6.3
    c: Coincident(g14,g13)
    c: Horizontal(g14)
    c: Distance(g14) = 2
    c: Vertical(g15)
    c: Distance(g15) = 3
    c: Block(g11)
    c: Coincident(g15,g11)
    c: Coincident(g16,g15)
    c: Horizontal(g16)
    c: Coincident(g17,g16)
    c: Coincident(g17,g14)
    c: Vertical(g17)
FEATURE [Part::Revolution] Revolve040  label="backCaseScrewRetainer001"
  Angle = 360
  Axis = (0,1,0)
  Base = (0,0,0)
  FaceMakerClass = Part::FaceMakerBullseye
  Placement = pos=(12.5,3,10) rot=(0,0,1;0rad)
  Solid = false
  Source = -> Face036
  Symmetric = false
FEATURE [Part::Feature] Face055
  shape: bbox 3.5 x 30.2 x 2e-07 mm, 1 faces, 0 solids (baked)
FEATURE [Part::Revolution] Revolve059  label="backCaseScrewPost"
  Angle = 360
  Axis = (0,1,0)
  Base = (0,0,0)
  FaceMakerClass = Part::FaceMakerBullseye
  Placement = pos=(12.5,4.5,10) rot=(0,0,1;0rad)
  Solid = false
  Source = -> Face055
  Symmetric = false
FEATURE [Part::Feature] Face056
  shape: bbox 3.5 x 30.2 x 2e-07 mm, 1 faces, 0 solids (baked)
FEATURE [Part::Revolution] Revolve060  label="backCaseScrewPost001"
  Angle = 360
  Axis = (0,1,0)
  Base = (0,0,0)
  FaceMakerClass = Part::FaceMakerBullseye
  Placement = pos=(12.5,4.5,62) rot=(0,0,1;0rad)
  Solid = false
  Source = -> Face056
  Symmetric = false
FEATURE [Part::Feature] Face057
  shape: bbox 3.5 x 17.8 x 2e-07 mm, 1 faces, 0 solids (baked)
FEATURE [Part::Revolution] Revolve061  label="removeToCreateScrewAndThreadedInsertHole"
  Angle = 360
  Axis = (0,1,0)
  Base = (0,0,0)
  FaceMakerClass = Part::FaceMakerBullseye
  Placement = pos=(12.5,0,10) rot=(0,0,1;0rad)
  Solid = false
  Source = -> Face057
  Symmetric = false
FEATURE [Part::Feature] Face058
  shape: bbox 3.5 x 17.8 x 2e-07 mm, 1 faces, 0 solids (baked)
FEATURE [Part::Revolution] Revolve062  label="removeToCreateScrewAndThreadedInsertHole001"
  Angle = 360
  Axis = (0,1,0)
  Base = (0,0,0)
  FaceMakerClass = Part::FaceMakerBullseye
  Placement = pos=(12.5,0,62) rot=(0,0,1;0rad)
  Solid = false
  Source = -> Face058
  Symmetric = false
FEATURE [Part::Feature] Face059
  shape: bbox 3.5 x 17.8 x 2e-07 mm, 1 faces, 0 solids (baked)
FEATURE [Part::Revolution] Revolve063  label="removeToCreateScrewAndThreadedInsertHole002"
  Angle = 360
  Axis = (0,1,0)
  Base = (0,0,0)
  FaceMakerClass = Part::FaceMakerBullseye
  Placement = pos=(89.5,0,68.5) rot=(0,0,1;0rad)
  Solid = false
  Source = -> Face059
  Symmetric = false
FEATURE [Part::Feature] Face060
  shape: bbox 3.5 x 17.8 x 2e-07 mm, 1 faces, 0 solids (baked)
FEATURE [Part::Revolution] Revolve064  label="removeToCreateScrewAndThreadedInsertHole003"
  Angle = 360
  Axis = (0,1,0)
  Base = (0,0,0)
  FaceMakerClass = Part::FaceMakerBullseye
  Placement = pos=(89.5,0,3.5) rot=(0,0,1;0rad)
  Solid = false
  Source = -> Face060
  Symmetric = false
FEATURE [Part::Feature] Face061
  shape: bbox 3.5 x 17.8 x 2e-07 mm, 1 faces, 0 solids (baked)
FEATURE [Part::Revolution] Revolve065  label="removeToCreateScrewAndThreadedInsertHole004"
  Angle = 360
  Axis = (0,1,0)
  Base = (0,0,0)
  FaceMakerClass = Part::FaceMakerBullseye
  Placement = pos=(102.5,4.7,3.5) rot=(0,0,1;0rad)
  Solid = false
  Source = -> Face061
  Symmetric = false
FEATURE [Part::Feature] Face062
  shape: bbox 3.5 x 17.8 x 2e-07 mm, 1 faces, 0 solids (baked)
FEATURE [Part::Revolution] Revolve066  label="removeToCreateScrewAndThreadedInsertHole005"
  Angle = 360
  Axis = (0,1,0)
  Base = (0,0,0)
  FaceMakerClass = Part::FaceMakerBullseye
  Placement = pos=(102.5,4.7,68.5) rot=(0,0,1;0rad)
  Solid = false
  Source = -> Face062
  Symmetric = false
FEATURE [Part::MultiFuse] Fusion047  label="makeHoles"
  Shapes = -> [Revolve066,Revolve065,Revolve064,Revolve063,Revolve062,Revolve061]
FEATURE [Part::Feature] Face063
  shape: bbox 3.6 x 3.2 x 2e-07 mm, 1 faces, 0 solids (baked)
FEATURE [Part::Revolution] Revolve067  label="moreFrontCaseScrewRetainer002"
  Angle = 360
  Axis = (0,1,0)
  Base = (0,0,0)
  FaceMakerClass = Part::FaceMakerBullseye
  Placement = pos=(102.5,4.5,68.5) rot=(0,0,1;0rad)
  Solid = false
  Source = -> Face063
  Symmetric = false
FEATURE [Part::Feature] Face064
  shape: bbox 3.6 x 3.2 x 2e-07 mm, 1 faces, 0 solids (baked)
FEATURE [Part::Revolution] Revolve068  label="moreFrontCaseScrewRetainer003"
  Angle = 360
  Axis = (0,1,0)
  Base = (0,0,0)
  FaceMakerClass = Part::FaceMakerBullseye
  Placement = pos=(102.5,4.5,3.5) rot=(0,0,1;0rad)
  Solid = false
  Source = -> Face064
  Symmetric = false
FEATURE [Part::Feature] Face065
  shape: bbox 3.5 x 17.8 x 2e-07 mm, 1 faces, 0 solids (baked)
FEATURE [Part::Revolution] Revolve069  label="removeToCreateScrewAndThreadedInsertHole006"
  Angle = 360
  Axis = (0,1,0)
  Base = (0,0,0)
  FaceMakerClass = Part::FaceMakerBullseye
  Placement = pos=(12.5,0,10) rot=(0,0,1;0rad)
  Solid = false
  Source = -> Face065
  Symmetric = false
FEATURE [Part::Feature] Face066
  shape: bbox 3.5 x 17.8 x 2e-07 mm, 1 faces, 0 solids (baked)
FEATURE [Part::Revolution] Revolve070  label="removeToCreateScrewAndThreadedInsertHole007"
  Angle = 360
  Axis = (0,1,0)
  Base = (0,0,0)
  FaceMakerClass = Part::FaceMakerBullseye
  Placement = pos=(12.5,0,62) rot=(0,0,1;0rad)
  Solid = false
  Source = -> Face066
  Symmetric = false
FEATURE [Part::Feature] Face067
  shape: bbox 3.5 x 17.8 x 2e-07 mm, 1 faces, 0 solids (baked)
FEATURE [Part::Revolution] Revolve071  label="removeToCreateScrewAndThreadedInsertHole008"
  Angle = 360
  Axis = (0,1,0)
  Base = (0,0,0)
  FaceMakerClass = Part::FaceMakerBullseye
  Placement = pos=(89.5,0,68.5) rot=(0,0,1;0rad)
  Solid = false
  Source = -> Face067
  Symmetric = false
FEATURE [Part::Feature] Face068
  shape: bbox 3.5 x 17.8 x 2e-07 mm, 1 faces, 0 solids (baked)
FEATURE [Part::Revolution] Revolve072  label="removeToCreateScrewAndThreadedInsertHole009"
  Angle = 360
  Axis = (0,1,0)
  Base = (0,0,0)
  FaceMakerClass = Part::FaceMakerBullseye
  Placement = pos=(89.5,0,3.5) rot=(0,0,1;0rad)
  Solid = false
  Source = -> Face068
  Symmetric = false
FEATURE [Part::Feature] Face069
  shape: bbox 3.5 x 17.8 x 2e-07 mm, 1 faces, 0 solids (baked)
FEATURE [Part::Feature] Face070
  shape: bbox 3.5 x 17.8 x 2e-07 mm, 1 faces, 0 solids (baked)
FEATURE [Part::Revolution] Revolve073  label="removeToCreateScrewAndThreadedInsertHole010"
  Angle = 360
  Axis = (0,1,0)
  Base = (0,0,0)
  FaceMakerClass = Part::FaceMakerBullseye
  Placement = pos=(102.5,4.7,3.5) rot=(0,0,1;0rad)
  Solid = false
  Source = -> Face069
  Symmetric = false
FEATURE [Part::Revolution] Revolve074  label="removeToCreateScrewAndThreadedInsertHole011"
  Angle = 360
  Axis = (0,1,0)
  Base = (0,0,0)
  FaceMakerClass = Part::FaceMakerBullseye
  Placement = pos=(102.5,4.7,68.5) rot=(0,0,1;0rad)
  Solid = false
  Source = -> Face070
  Symmetric = false
FEATURE [Part::MultiFuse] Fusion048  label="makeHoles001"
  Shapes = -> [Revolve074,Revolve073,Revolve072,Revolve071,Revolve070,Revolve069]
FEATURE [Part::MultiFuse] Fusion049  label="caseScrewRetainers"
  Shapes = -> [Revolve067,Revolve068,Revolve048,Revolve047,Revolve039,Revolve040]
FEATURE [Part::Cut] Cut015  label="caseScrewRetainers001"
  Base = -> Fusion049
  Tool = -> Fusion048
FEATURE [Part::MultiFuse] Fusion050  label="casePillars"
  Shapes = -> [Revolve055,Revolve054,Revolve043,Revolve046,Revolve059,Revolve060]
FEATURE [Part::Feature] Face071 .. Face076  x6 (patterned run collapsed; names and placements below)
  shape: bbox 3.5 x 17.8 x 2e-07 mm, 1 faces, 0 solids (baked)
FEATURE [Part::Revolution] Revolve075  label="removeToCreateScrewAndThreadedInsertHole012"
  Angle = 360
  Axis = (0,1,0)
  Base = (0,0,0)
  FaceMakerClass = Part::FaceMakerBullseye
  Placement = pos=(12.5,0,10) rot=(0,0,1;0rad)
  Solid = false
  Source = -> Face071
  Symmetric = false
FEATURE [Part::Revolution] Revolve076  label="removeToCreateScrewAndThreadedInsertHole013"
  Angle = 360
  Axis = (0,1,0)
  Base = (0,0,0)
  FaceMakerClass = Part::FaceMakerBullseye
  Placement = pos=(12.5,0,62) rot=(0,0,1;0rad)
  Solid = false
  Source = -> Face072
  Symmetric = false
FEATURE [Part::Revolution] Revolve077  label="removeToCreateScrewAndThreadedInsertHole014"
  Angle = 360
  Axis = (0,1,0)
  Base = (0,0,0)
  FaceMakerClass = Part::FaceMakerBullseye
  Placement = pos=(89.5,0,68.5) rot=(0,0,1;0rad)
  Solid = false
  Source = -> Face073
  Symmetric = false
FEATURE [Part::Revolution] Revolve078  label="removeToCreateScrewAndThreadedInsertHole015"
  Angle = 360
  Axis = (0,1,0)
  Base = (0,0,0)
  FaceMakerClass = Part::FaceMakerBullseye
  Placement = pos=(89.5,0,3.5) rot=(0,0,1;0rad)
  Solid = false
  Source = -> Face074
  Symmetric = false
FEATURE [Part::Revolution] Revolve079  label="removeToCreateScrewAndThreadedInsertHole016"
  Angle = 360
  Axis = (0,1,0)
  Base = (0,0,0)
  FaceMakerClass = Part::FaceMakerBullseye
  Placement = pos=(102.5,4.7,3.5) rot=(0,0,1;0rad)
  Solid = false
  Source = -> Face075
  Symmetric = false
FEATURE [Part::Revolution] Revolve080  label="removeToCreateScrewAndThreadedInsertHole017"
  Angle = 360
  Axis = (0,1,0)
  Base = (0,0,0)
  FaceMakerClass = Part::FaceMakerBullseye
  Placement = pos=(102.5,4.7,68.5) rot=(0,0,1;0rad)
  Solid = false
  Source = -> Face076
  Symmetric = false
FEATURE [Part::MultiFuse] Fusion051  label="makeHoles002"
  Shapes = -> [Revolve080,Revolve079,Revolve078,Revolve077,Revolve076,Revolve075]
FEATURE [Part::Cut] Cut016  label="caesPillars"
  Base = -> Fusion050
  Tool = -> Fusion051
FEATURE [Part::Revolution] Revolve009  label="plugHousing016"
  Angle = 360
  Axis = (0,1,0)
  Base = (0,0,0)
  FaceMakerClass = Part::FaceMakerBullseye
  Placement = pos=(0,0,36.15) rot=(0,0,1;0rad)
  Solid = false
  Source = -> Face012
  Symmetric = false
FEATURE [Part::MultiFuse] Fusion014  label="plugHousing023"
  Placement = pos=(0,0,0) rot=(0,0,1;1.5708rad)
  Shapes = -> [Revolve011,Revolve009]
FEATURE [Part::Revolution] Revolve010  label="plugHousing017"
  Angle = 360
  Axis = (0,1,0)
  Base = (0,0,0)
  FaceMakerClass = Part::FaceMakerBullseye
  Placement = pos=(0,0,36.15) rot=(0,0,1;0rad)
  Solid = false
  Source = -> Face014
  Symmetric = false
FEATURE [Part::MultiFuse] Fusion015  label="plugHousing024"
  Placement = pos=(0,0,0) rot=(0,0,1;1.5708rad)
  Shapes = -> [Revolve010,Revolve015]
FEATURE [Part::Revolution] Revolve014  label="plugHousing026"
  Angle = 360
  Axis = (0,1,0)
  Base = (0,0,0)
  FaceMakerClass = Part::FaceMakerBullseye
  Placement = pos=(0,0,36.15) rot=(0,0,1;0rad)
  Solid = false
  Source = -> Face011
  Symmetric = false
FEATURE [Part::Revolution] Revolve013  label="plugHousing025"
  Angle = 360
  Axis = (0,1,0)
  Base = (0,0,0)
  FaceMakerClass = Part::FaceMakerBullseye
  Placement = pos=(0,0,36.15) rot=(0,0,1;0rad)
  Solid = false
  Source = -> Face015
  Symmetric = false
FEATURE [Part::MultiFuse] Fusion016  label="plugHousing028"
  Placement = pos=(0,19,0) rot=(0,0,1;3.14159rad)
  Shapes = -> [Fusion014,Fusion013]
FEATURE [Part::MultiFuse] Fusion011  label="plugHousing018"
  Placement = pos=(0,0,0) rot=(0,0,1;1.5708rad)
  Shapes = -> [Revolve014,Revolve013]
FEATURE [Part::MultiFuse] Fusion012  label="plugHousing019"
  Placement = pos=(0,19,0) rot=(0,0,1;3.14159rad)
  Shapes = -> [Fusion011,Fusion015]
FEATURE [Part::MultiFuse] Fusion017  label="plugHousing029"
  Placement = pos=(122.621,0,-0.15) rot=(0,0,1;0rad)
  Shapes = -> [Fusion016,Fusion012]
FEATURE [Part::MultiFuse] Fusion052  label="casePillarRetainers"
  Shapes = -> [Extrude012,Extrude013,Extrude014,Extrude015,Extrude016,Extrude017,Extrude018,Extrude019,Box011,Box012]
FEATURE [Part::Feature] Face077
  shape: bbox 3.5 x 17.8 x 2e-07 mm, 1 faces, 0 solids (baked)
FEATURE [Part::Revolution] Revolve081  label="removeToCreateScrewAndThreadedInsertHole018"
  Angle = 360
  Axis = (0,1,0)
  Base = (0,0,0)
  FaceMakerClass = Part::FaceMakerBullseye
  Placement = pos=(62.3,30.3,19.7) rot=(0,0,1;0rad)
  Solid = false
  Source = -> Face077
  Symmetric = false
FEATURE [Part::Feature] Face078
  shape: bbox 3.5 x 17.8 x 2e-07 mm, 1 faces, 0 solids (baked)
FEATURE [Part::Revolution] Revolve082  label="removeToCreateScrewAndThreadedInsertHole019"
  Angle = 360
  Axis = (0,1,0)
  Base = (0,0,0)
  FaceMakerClass = Part::FaceMakerBullseye
  Placement = pos=(62.3,30.3,51.7) rot=(0,0,1;0rad)
  Solid = false
  Source = -> Face078
  Symmetric = false
FEATURE [Part::Feature] Face079
  shape: bbox 3.5 x 17.8 x 2e-07 mm, 1 faces, 0 solids (baked)
FEATURE [Part::Revolution] Revolve083  label="removeToCreateScrewAndThreadedInsertHole020"
  Angle = 360
  Axis = (0,1,0)
  Base = (0,0,0)
  FaceMakerClass = Part::FaceMakerBullseye
  Placement = pos=(30.3,30.3,19.7) rot=(0,0,1;0rad)
  Solid = false
  Source = -> Face079
  Symmetric = false
FEATURE [Part::Feature] Face080
  shape: bbox 3.5 x 17.8 x 2e-07 mm, 1 faces, 0 solids (baked)
FEATURE [Part::Revolution] Revolve084  label="removeToCreateScrewAndThreadedInsertHole021"
  Angle = 360
  Axis = (0,1,0)
  Base = (0,0,0)
  FaceMakerClass = Part::FaceMakerBullseye
  Placement = pos=(30.3,30.3,51.7) rot=(0,0,1;0rad)
  Solid = false
  Source = -> Face080
  Symmetric = false
FEATURE [Part::MultiFuse] Fusion053  label="createThreadedInsertHolesForFan"
  Shapes = -> [Revolve081,Revolve082,Revolve083,Revolve084]
FEATURE [Part::Cut] Cut017  label="fanScrewHousing001"
  Base = -> Fusion046
  Tool = -> Fusion053
FEATURE [Part::Feature] Face081
  shape: bbox 3.5 x 17.8 x 2e-07 mm, 1 faces, 0 solids (baked)
FEATURE [Part::Revolution] Revolve085  label="removeToCreateScrewAndThreadedInsertHole022"
  Angle = 360
  Axis = (0,1,0)
  Base = (0,0,0)
  FaceMakerClass = Part::FaceMakerBullseye
  Placement = pos=(62.3,30.3,19.7) rot=(0,0,1;0rad)
  Solid = false
  Source = -> Face081
  Symmetric = false
FEATURE [Part::Feature] Face082
  shape: bbox 3.5 x 17.8 x 2e-07 mm, 1 faces, 0 solids (baked)
FEATURE [Part::Revolution] Revolve086  label="removeToCreateScrewAndThreadedInsertHole023"
  Angle = 360
  Axis = (0,1,0)
  Base = (0,0,0)
  FaceMakerClass = Part::FaceMakerBullseye
  Placement = pos=(62.3,30.3,51.7) rot=(0,0,1;0rad)
  Solid = false
  Source = -> Face082
  Symmetric = false
FEATURE [Part::Feature] Face083
  shape: bbox 3.5 x 17.8 x 2e-07 mm, 1 faces, 0 solids (baked)
FEATURE [Part::Revolution] Revolve087  label="removeToCreateScrewAndThreadedInsertHole024"
  Angle = 360
  Axis = (0,1,0)
  Base = (0,0,0)
  FaceMakerClass = Part::FaceMakerBullseye
  Placement = pos=(30.3,30.3,19.7) rot=(0,0,1;0rad)
  Solid = false
  Source = -> Face083
  Symmetric = false
FEATURE [Part::Feature] Face084
  shape: bbox 3.5 x 17.8 x 2e-07 mm, 1 faces, 0 solids (baked)
FEATURE [Part::Revolution] Revolve088  label="removeToCreateScrewAndThreadedInsertHole025"
  Angle = 360
  Axis = (0,1,0)
  Base = (0,0,0)
  FaceMakerClass = Part::FaceMakerBullseye
  Placement = pos=(30.3,30.3,51.7) rot=(0,0,1;0rad)
  Solid = false
  Source = -> Face084
  Symmetric = false
FEATURE [Part::MultiFuse] Fusion054  label="createThreadedInsertHolesForFan001"
  Shapes = -> [Revolve085,Revolve086,Revolve087,Revolve088]
FEATURE [Part::Cut] Cut018  label="top007"
  Base = -> Fusion040
  Tool = -> Fusion054
FEATURE [Sketcher::SketchObject] Sketch029
  FullyConstrained = false
  Placement = pos=(0,0,0) rot=(1,0,0;1.5708rad)
  sketch-geometry (24):
    g0: ArcOfCircle CenterX=-4 CenterY=-10.5 CenterZ=0 NormalX=0 NormalY=0 NormalZ=1 AngleXU=0 Radius=1.5 StartAngle=6e-16 EndAngle=3.14159
    g1: ArcOfCircle CenterX=-34.2 CenterY=-10.5 CenterZ=0 NormalX=0 NormalY=0 NormalZ=1 AngleXU=0 Radius=1.5 StartAngle=0 EndAngle=3.14159
    g2: ArcOfCircle CenterX=-34.2 CenterY=-27.7 CenterZ=0 NormalX=0 NormalY=0 NormalZ=1 AngleXU=0 Radius=1.5 StartAngle=3.14159 EndAngle=6.28319
    g3: ArcOfCircle CenterX=-4 CenterY=-27.7 CenterZ=0 NormalX=0 NormalY=0 NormalZ=1 AngleXU=0 Radius=1.5 StartAngle=3.1416 EndAngle=6.28319
    g4: ArcOfCircle CenterX=-10 CenterY=-4.3 CenterZ=0 NormalX=0 NormalY=0 NormalZ=1 AngleXU=0 Radius=1.5 StartAngle=2e-16 EndAngle=3.14159
    g5: ArcOfCircle CenterX=-16.1 CenterY=-1.8 CenterZ=0 NormalX=0 NormalY=0 NormalZ=1 AngleXU=0 Radius=1.5 StartAngle=5e-16 EndAngle=3.14159
    g6: ArcOfCircle CenterX=-22.1 CenterY=-1.8 CenterZ=0 NormalX=0 NormalY=0 NormalZ=1 AngleXU=0 Radius=1.5 StartAngle=5e-16 EndAngle=3.14159
    g7: ArcOfCircle CenterX=-28.2 CenterY=-4.3 CenterZ=0 NormalX=0 NormalY=0 NormalZ=1 AngleXU=0 Radius=1.5 StartAngle=2e-16 EndAngle=3.14159
    g8: ArcOfCircle CenterX=-10 CenterY=-33.9 CenterZ=0 NormalX=0 NormalY=0 NormalZ=1 AngleXU=0 Radius=1.5 StartAngle=3.14159 EndAngle=6.28319
    g9: ArcOfCircle CenterX=-16.1 CenterY=-36.4 CenterZ=0 NormalX=0 NormalY=0 NormalZ=1 AngleXU=0 Radius=1.5 StartAngle=3.14159 EndAngle=6.28319
    g10: ArcOfCircle CenterX=-22.1 CenterY=-36.4 CenterZ=0 NormalX=0 NormalY=0 NormalZ=1 AngleXU=0 Radius=1.5 StartAngle=3.14159 EndAngle=6.28319
    g11: ArcOfCircle CenterX=-28.2 CenterY=-33.9 CenterZ=0 NormalX=0 NormalY=0 NormalZ=1 AngleXU=0 Radius=1.5 StartAngle=3.14159 EndAngle=6.28319
    g12: LineSegment StartX=-35.7 StartY=-10.5 StartZ=0 EndX=-35.7 EndY=-27.7 EndZ=0
    g13: LineSegment StartX=-32.7 StartY=-10.5 StartZ=0 EndX=-32.7 EndY=-27.7 EndZ=0
    g14: LineSegment StartX=-29.7 StartY=-33.9 StartZ=0 EndX=-29.7 EndY=-4.3 EndZ=0
    g15: LineSegment StartX=-26.7 StartY=-33.9 StartZ=0 EndX=-26.7 EndY=-4.3 EndZ=0
    g16: LineSegment StartX=-2.5 StartY=-10.5 StartZ=0 EndX=-2.5 EndY=-27.7 EndZ=0
    g17: LineSegment StartX=-8.5 StartY=-4.3 StartZ=0 EndX=-8.5 EndY=-33.9 EndZ=0
    g18: LineSegment StartX=-5.5 StartY=-10.5 StartZ=0 EndX=-5.5 EndY=-27.7 EndZ=0
    g19: LineSegment StartX=-11.5 StartY=-4.3 StartZ=0 EndX=-11.5 EndY=-33.9 EndZ=0
    g20: LineSegment StartX=-14.6 StartY=-1.8 StartZ=0 EndX=-14.6 EndY=-36.4 EndZ=0
    g21: LineSegment StartX=-17.6 StartY=-1.8 StartZ=0 EndX=-17.6 EndY=-36.4 EndZ=0
    g22: LineSegment StartX=-20.6 StartY=-36.4 StartZ=0 EndX=-20.6 EndY=-1.8 EndZ=0
    g23: LineSegment StartX=-23.6 StartY=-1.8 StartZ=0 EndX=-23.6 EndY=-36.4 EndZ=0
  constraints (48):
    c: Block(g0)
    c: Block(g1)
    c: Block(g2)
    c: Block(g3)
    c: Block(g4)
    c: Block(g5)
    c: Block(g6)
    c: Block(g7)
    c: Block(g8)
    c: Block(g9)
    c: Block(g10)
    c: Block(g11)
    c: Coincident(g12,g1)
    c: Coincident(g12,g2)
    c: Vertical(g12)
    c: Coincident(g13,g1)
    c: Coincident(g13,g2)
    c: Vertical(g13)
    c: Coincident(g14,g11)
    c: Coincident(g14,g7)
    c: Vertical(g14)
    c: Coincident(g15,g11)
    c: Coincident(g15,g7)
    c: Vertical(g15)
    c: Coincident(g16,g0)
    c: Coincident(g16,g3)
    c: Vertical(g16)
    c: Coincident(g17,g4)
    c: Coincident(g17,g8)
    c: Vertical(g17)
    c: Coincident(g18,g0)
    c: Coincident(g18,g3)
    c: Vertical(g18)
    c: Coincident(g19,g4)
    c: Coincident(g19,g8)
    c: Vertical(g19)
    c: Coincident(g20,g5)
    c: Coincident(g20,g9)
    c: Vertical(g20)
    c: Coincident(g21,g5)
    c: Coincident(g21,g9)
    c: Vertical(g21)
    c: Coincident(g22,g10)
    c: Coincident(g22,g6)
    c: Vertical(g22)
    c: Coincident(g23,g6)
    c: Coincident(g23,g10)
    c: Vertical(g23)
FEATURE [Part::Extrusion] Extrude020  label="removeToCreateFanGrillHoles"
  Base = -> Sketch029
  Dir = (0,-1,6e-16)
  DirMode = 2
  FaceMakerClass = Part::FaceMakerBullseye
  LengthFwd = 10
  LengthRev = 0
  Placement = pos=(65.4,44,54.82) rot=(0,0,1;0rad)
  Solid = true
  Symmetric = false
FEATURE [Part::MultiFuse] Fusion055  label="top008"
  Shapes = -> [Cut017,Cut018]
FEATURE [Part::Cut] Cut019  label="top009"
  Base = -> Fusion055
  Tool = -> Extrude020
FEATURE [App::MeasureDistance] Distance003  label="Distance: 71.95 mm"
  Distance = 71.9513
  P1 = (117,38,72)
  P2 = (117,38,0.0487319)
FEATURE [Sketcher::SketchObject] Sketch030
  FullyConstrained = true
  Placement = pos=(117,19,0) rot=(0.57735,0.57735,0.57735;2.0944rad)
  sketch-geometry (48):
    g0: LineSegment StartX=-49.19 StartY=69.25 StartZ=0 EndX=-49.19 EndY=66.25 EndZ=0
    g1: LineSegment StartX=-49.19 StartY=63.5 StartZ=0 EndX=-49.19 EndY=60.5 EndZ=0
    g2: LineSegment StartX=-49.19 StartY=57.75 StartZ=0 EndX=-49.19 EndY=54.75 EndZ=0
    g3: LineSegment StartX=-49.19 StartY=52 StartZ=0 EndX=-49.19 EndY=49 EndZ=0
    g4: LineSegment StartX=-49.19 StartY=46.25 StartZ=0 EndX=-49.19 EndY=43.25 EndZ=0
    g5: LineSegment StartX=-49.19 StartY=40.5 StartZ=0 EndX=-49.19 EndY=37.5 EndZ=0
    g6: LineSegment StartX=-49.19 StartY=34.5 StartZ=0 EndX=-49.19 EndY=31.5 EndZ=0
    g7: LineSegment StartX=-49.19 StartY=28.75 StartZ=0 EndX=-49.19 EndY=25.75 EndZ=0
    g8: LineSegment StartX=-49.19 StartY=23 StartZ=0 EndX=-49.19 EndY=20 EndZ=0
    g9: LineSegment StartX=-49.19 StartY=17.25 StartZ=0 EndX=-49.19 EndY=14.25 EndZ=0
    g10: LineSegment StartX=-49.19 StartY=11.5 StartZ=0 EndX=-49.19 EndY=8.5 EndZ=0
    g11: LineSegment StartX=-49.19 StartY=5.75 StartZ=0 EndX=-49.19 EndY=2.75 EndZ=0
    g12: ArcOfCircle CenterX=-1.5 CenterY=67.75 CenterZ=0 NormalX=0 NormalY=0 NormalZ=1 AngleXU=0 Radius=1.5 StartAngle=4.71239 EndAngle=7.85398
    g13: ArcOfCircle CenterX=-1.5 CenterY=62 CenterZ=0 NormalX=0 NormalY=0 NormalZ=1 AngleXU=0 Radius=1.5 StartAngle=4.71239 EndAngle=7.85398
    g14: ArcOfCircle CenterX=-1.5 CenterY=56.25 CenterZ=0 NormalX=0 NormalY=0 NormalZ=1 AngleXU=0 Radius=1.5 StartAngle=4.71239 EndAngle=7.85398
    g15: ArcOfCircle CenterX=-11.49 CenterY=50.5 CenterZ=0 NormalX=0 NormalY=0 NormalZ=1 AngleXU=0 Radius=1.5 StartAngle=4.71239 EndAngle=7.85398
    g16: ArcOfCircle CenterX=-16.28 CenterY=44.75 CenterZ=0 NormalX=0 NormalY=0 NormalZ=1 AngleXU=0 Radius=1.5 StartAngle=4.71239 EndAngle=7.85398
    g17: ArcOfCircle CenterX=-18.2337 CenterY=39 CenterZ=0 NormalX=0 NormalY=0 NormalZ=1 AngleXU=0 Radius=1.5 StartAngle=4.71485 EndAngle=7.85398
    g18: ArcOfCircle CenterX=-16.2837 CenterY=27.25 CenterZ=0 NormalX=0 NormalY=0 NormalZ=1 AngleXU=0 Radius=1.5 StartAngle=4.71485 EndAngle=7.85398
    g19: ArcOfCircle CenterX=-18.2337 CenterY=33 CenterZ=0 NormalX=0 NormalY=0 NormalZ=1 AngleXU=0 Radius=1.5 StartAngle=4.71485 EndAngle=7.85398
    g20: ArcOfCircle CenterX=-11.49 CenterY=21.5 CenterZ=0 NormalX=0 NormalY=0 NormalZ=1 AngleXU=0 Radius=1.5 StartAngle=4.71239 EndAngle=7.85398
    g21: ArcOfCircle CenterX=-1.5 CenterY=4.25 CenterZ=0 NormalX=0 NormalY=0 NormalZ=1 AngleXU=0 Radius=1.5 StartAngle=4.71239 EndAngle=7.85398
    g22: ArcOfCircle CenterX=-1.5 CenterY=10 CenterZ=0 NormalX=0 NormalY=0 NormalZ=1 AngleXU=0 Radius=1.5 StartAngle=4.71239 EndAngle=7.85398
    g23: ArcOfCircle CenterX=-1.5 CenterY=15.75 CenterZ=0 NormalX=0 NormalY=0 NormalZ=1 AngleXU=0 Radius=1.5 StartAngle=4.71239 EndAngle=7.85398
    g24: LineSegment StartX=-49.19 StartY=69.25 StartZ=0 EndX=-1.5 EndY=69.25 EndZ=0
    g25: LineSegment StartX=-49.19 StartY=66.25 StartZ=0 EndX=-1.5 EndY=66.25 EndZ=0
    g26: LineSegment StartX=-49.19 StartY=63.5 StartZ=0 EndX=-1.5 EndY=63.5 EndZ=0
    g27: LineSegment StartX=-49.19 StartY=60.5 StartZ=0 EndX=-1.5 EndY=60.5 EndZ=0
    g28: LineSegment StartX=-49.19 StartY=57.75 StartZ=0 EndX=-1.5 EndY=57.75 EndZ=0
    g29: LineSegment StartX=-49.19 StartY=54.75 StartZ=0 EndX=-1.5 EndY=54.75 EndZ=0
    g30: LineSegment StartX=-49.19 StartY=52 StartZ=0 EndX=-11.49 EndY=52 EndZ=0
    g31: LineSegment StartX=-49.19 StartY=49 StartZ=0 EndX=-11.49 EndY=49 EndZ=0
    g32: LineSegment StartX=-49.19 StartY=46.25 StartZ=0 EndX=-16.28 EndY=46.25 EndZ=0
    g33: LineSegment StartX=-49.19 StartY=43.25 StartZ=0 EndX=-16.28 EndY=43.25 EndZ=0
    g34: LineSegment StartX=-49.19 StartY=40.5 StartZ=0 EndX=-18.2337 EndY=40.5 EndZ=0
    g35: LineSegment StartX=-49.19 StartY=37.5 StartZ=0 EndX=-18.23 EndY=37.5 EndZ=0
    g36: LineSegment StartX=-49.19 StartY=34.5 StartZ=0 EndX=-18.2337 EndY=34.5 EndZ=0
    g37: LineSegment StartX=-49.19 StartY=31.5 StartZ=0 EndX=-18.23 EndY=31.5 EndZ=0
    g38: LineSegment StartX=-49.19 StartY=28.75 StartZ=0 EndX=-16.2837 EndY=28.75 EndZ=0
    g39: LineSegment StartX=-49.19 StartY=25.75 StartZ=0 EndX=-16.28 EndY=25.75 EndZ=0
    g40: LineSegment StartX=-49.19 StartY=23 StartZ=0 EndX=-11.49 EndY=23 EndZ=0
    g41: LineSegment StartX=-49.19 StartY=20 StartZ=0 EndX=-11.49 EndY=20 EndZ=0
    g42: LineSegment StartX=-49.19 StartY=17.25 StartZ=0 EndX=-1.5 EndY=17.25 EndZ=0
    g43: LineSegment StartX=-49.19 StartY=14.25 StartZ=0 EndX=-1.5 EndY=14.25 EndZ=0
    g44: LineSegment StartX=-49.19 StartY=11.5 StartZ=0 EndX=-1.5 EndY=11.5 EndZ=0
    g45: LineSegment StartX=-49.19 StartY=8.5 StartZ=0 EndX=-1.5 EndY=8.5 EndZ=0
    g46: LineSegment StartX=-49.19 StartY=5.75 StartZ=0 EndX=-1.5 EndY=5.75 EndZ=0
    g47: LineSegment StartX=-49.19 StartY=2.75 StartZ=0 EndX=-1.5 EndY=2.75 EndZ=0
  constraints (120):
    c: Vertical(g0)
    c: Distance(g0) = 3
    c: Block(g0)
    c: Vertical(g1)
    c: Distance(g1) = 3
    c: Vertical(g2)
    c: Equal(g0,g2) = 3
    c: Block(g2)
    c: Vertical(g3)
    c: Equal(g1,g3) = 3
    c: Vertical(g4)
    c: Equal(g0,g4) = 3
    c: Block(g4)
    c: Vertical(g5)
    c: Equal(g1,g5) = 3
    c: Vertical(g6)
    c: Equal(g0,g6) = 3
    c: Block(g6)
    c: Vertical(g7)
    c: Equal(g1,g7) = 3
    c: Vertical(g8)
    c: Equal(g0,g8) = 3
    c: Block(g8)
    c: Vertical(g9)
    c: Equal(g1,g9) = 3
    c: Vertical(g10)
    c: Equal(g0,g10) = 3
    c: Block(g10)
    c: Vertical(g11)
    c: Equal(g1,g11) = 3
    c: Block(g12)
    c: Block(g13)
    c: Block(g14)
    c: Block(g15)
    c: Block(g16)
    c: Block(g17)
    c: Block(g18)
    c: Block(g19)
    c: Block(g20)
    c: Block(g21)
    c: Block(g22)
    c: Block(g23)
    c: Block(g11)
    c: Block(g9)
    c: Block(g7)
    c: Block(g5)
    c: Block(g3)
    c: Block(g1)
    c: Coincident(g24,g0)
    c: Coincident(g24,g12)
    c: Horizontal(g24)
    c: Coincident(g25,g0)
    c: Coincident(g25,g12)
    c: Horizontal(g25)
    c: Coincident(g26,g1)
    c: Coincident(g26,g13)
    c: Horizontal(g26)
    c: Coincident(g27,g1)
    c: Coincident(g27,g13)
    c: Horizontal(g27)
    c: Coincident(g28,g2)
    c: Coincident(g28,g14)
    c: Horizontal(g28)
    c: Coincident(g29,g2)
    c: Coincident(g29,g14)
    c: Horizontal(g29)
    c: Coincident(g30,g3)
    c: Coincident(g30,g15)
    c: Horizontal(g30)
    c: Coincident(g31,g3)
    c: Coincident(g31,g15)
    c: Horizontal(g31)
    c: Coincident(g32,g4)
    c: Coincident(g32,g16)
    c: Horizontal(g32)
    c: Coincident(g33,g4)
    c: Coincident(g33,g16)
    c: Horizontal(g33)
    c: Coincident(g34,g5)
    c: Coincident(g34,g17)
    c: Horizontal(g34)
    c: Coincident(g35,g5)
    c: Coincident(g35,g17)
    c: Horizontal(g35)
    c: Coincident(g36,g6)
    c: Coincident(g36,g19)
    c: Horizontal(g36)
    c: Coincident(g37,g6)
    c: Coincident(g37,g19)
    c: Horizontal(g37)
    c: Coincident(g38,g7)
    c: Coincident(g38,g18)
    c: Horizontal(g38)
    c: Coincident(g39,g7)
    c: Coincident(g39,g18)
    c: Horizontal(g39)
    c: Coincident(g40,g8)
    c: Coincident(g40,g20)
    c: Horizontal(g40)
    c: Coincident(g41,g8)
    c: Coincident(g41,g20)
    c: Horizontal(g41)
    c: Coincident(g42,g9)
    c: Coincident(g42,g23)
    c: Horizontal(g42)
    c: Coincident(g43,g9)
    c: Coincident(g43,g23)
    c: Horizontal(g43)
    c: Coincident(g44,g10)
    c: Coincident(g44,g22)
    c: Horizontal(g44)
    c: Coincident(g45,g10)
    c: Coincident(g45,g22)
    c: Horizontal(g45)
    c: Coincident(g46,g11)
    c: Coincident(g46,g21)
    c: Horizontal(g46)
    c: Coincident(g47,g11)
    c: Coincident(g47,g21)
    c: Horizontal(g47)
FEATURE [Sketcher::SketchObject] Sketch031
  FullyConstrained = true
  Placement = pos=(117,19,0) rot=(0.57735,0.57735,0.57735;2.0944rad)
  sketch-geometry (24):
    g0: ArcOfCircle CenterX=-49.19 CenterY=67.75 CenterZ=0 NormalX=0 NormalY=0 NormalZ=1 AngleXU=0 Radius=1.5 StartAngle=1.5708 EndAngle=4.71239
    g1: ArcOfCircle CenterX=-49.19 CenterY=62 CenterZ=0 NormalX=0 NormalY=0 NormalZ=1 AngleXU=0 Radius=1.5 StartAngle=1.5708 EndAngle=4.71239
    g2: ArcOfCircle CenterX=-49.19 CenterY=56.25 CenterZ=0 NormalX=0 NormalY=0 NormalZ=1 AngleXU=0 Radius=1.5 StartAngle=1.5708 EndAngle=4.71239
    g3: ArcOfCircle CenterX=-49.19 CenterY=50.5 CenterZ=0 NormalX=0 NormalY=0 NormalZ=1 AngleXU=0 Radius=1.5 StartAngle=1.5708 EndAngle=4.71239
    g4: ArcOfCircle CenterX=-49.19 CenterY=44.75 CenterZ=0 NormalX=0 NormalY=0 NormalZ=1 AngleXU=0 Radius=1.5 StartAngle=1.5708 EndAngle=4.71239
    g5: ArcOfCircle CenterX=-49.19 CenterY=39 CenterZ=0 NormalX=0 NormalY=0 NormalZ=1 AngleXU=0 Radius=1.5 StartAngle=1.5708 EndAngle=4.71239
    g6: ArcOfCircle CenterX=-49.19 CenterY=33 CenterZ=0 NormalX=0 NormalY=0 NormalZ=1 AngleXU=0 Radius=1.5 StartAngle=1.5708 EndAngle=4.71239
    g7: ArcOfCircle CenterX=-49.19 CenterY=27.25 CenterZ=0 NormalX=0 NormalY=0 NormalZ=1 AngleXU=0 Radius=1.5 StartAngle=1.5708 EndAngle=4.71239
    g8: ArcOfCircle CenterX=-49.19 CenterY=21.5 CenterZ=0 NormalX=0 NormalY=0 NormalZ=1 AngleXU=0 Radius=1.5 StartAngle=1.5708 EndAngle=4.71239
    g9: ArcOfCircle CenterX=-49.19 CenterY=15.75 CenterZ=0 NormalX=0 NormalY=0 NormalZ=1 AngleXU=0 Radius=1.5 StartAngle=1.5708 EndAngle=4.71239
    g10: ArcOfCircle CenterX=-49.19 CenterY=10 CenterZ=0 NormalX=0 NormalY=0 NormalZ=1 AngleXU=0 Radius=1.5 StartAngle=1.5708 EndAngle=4.71239
    g11: ArcOfCircle CenterX=-49.19 CenterY=4.25 CenterZ=0 NormalX=0 NormalY=0 NormalZ=1 AngleXU=0 Radius=1.5 StartAngle=1.5708 EndAngle=4.71239
    g12: LineSegment StartX=-49.19 StartY=69.25 StartZ=0 EndX=-49.19 EndY=66.25 EndZ=0
    g13: LineSegment StartX=-49.19 StartY=63.5 StartZ=0 EndX=-49.19 EndY=60.5 EndZ=0
    g14: LineSegment StartX=-49.19 StartY=57.75 StartZ=0 EndX=-49.19 EndY=54.75 EndZ=0
    g15: LineSegment StartX=-49.19 StartY=52 StartZ=0 EndX=-49.19 EndY=49 EndZ=0
    g16: LineSegment StartX=-49.19 StartY=46.25 StartZ=0 EndX=-49.19 EndY=43.25 EndZ=0
    g17: LineSegment StartX=-49.19 StartY=40.5 StartZ=0 EndX=-49.19 EndY=37.5 EndZ=0
    g18: LineSegment StartX=-49.19 StartY=34.5 StartZ=0 EndX=-49.19 EndY=31.5 EndZ=0
    g19: LineSegment StartX=-49.19 StartY=28.75 StartZ=0 EndX=-49.19 EndY=25.75 EndZ=0
    g20: LineSegment StartX=-49.19 StartY=23 StartZ=0 EndX=-49.19 EndY=20 EndZ=0
    g21: LineSegment StartX=-49.19 StartY=17.25 StartZ=0 EndX=-49.19 EndY=14.25 EndZ=0
    g22: LineSegment StartX=-49.19 StartY=11.5 StartZ=0 EndX=-49.19 EndY=8.5 EndZ=0
    g23: LineSegment StartX=-49.19 StartY=5.75 StartZ=0 EndX=-49.19 EndY=2.75 EndZ=0
  constraints (48):
    c: Block(g0)
    c: Block(g1)
    c: Block(g2)
    c: Block(g3)
    c: Block(g4)
    c: Block(g5)
    c: Block(g6)
    c: Block(g7)
    c: Block(g8)
    c: Block(g9)
    c: Block(g10)
    c: Block(g11)
    c: Coincident(g12,g0)
    c: Coincident(g12,g0)
    c: Vertical(g12)
    c: Vertical(g13)
    c: Coincident(g13,g1)
    c: Vertical(g14)
    c: Coincident(g14,g2)
    c: Vertical(g15)
    c: Coincident(g15,g3)
    c: Vertical(g16)
    c: Coincident(g16,g4)
    c: Vertical(g17)
    c: Coincident(g17,g5)
    c: Vertical(g18)
    c: Coincident(g18,g6)
    c: Vertical(g19)
    c: Coincident(g19,g7)
    c: Vertical(g20)
    c: Coincident(g20,g8)
    c: Vertical(g21)
    c: Coincident(g21,g9)
    c: Vertical(g22)
    c: Coincident(g22,g10)
    c: Vertical(g23)
    c: Coincident(g23,g11)
    c: Block(g23)
    c: Block(g22)
    c: Block(g21)
    c: Block(g20)
    c: Block(g13)
    c: Block(g14)
    c: Block(g15)
    c: Block(g16)
    c: Block(g17)
    c: Block(g18)
    c: Block(g19)
FEATURE [Part::Extrusion] Extrude022
  Base = -> Sketch030
  Dir = (1,-2e-16,2e-16)
  DirMode = 2
  FaceMakerClass = Part::FaceMakerBullseye
  LengthFwd = 19
  LengthRev = 0
  Placement = pos=(-19,0,0) rot=(0,0,1;0rad)
  Solid = true
  Symmetric = false
FEATURE [Part::Fillet] Fillet022
  Base = -> Extrude022
  Edges = 24 edges r=1.49: [Edge6,Edge11,Edge18,Edge23,Edge30,Edge35,Edge42,Edge47,Edge54,Edge59,Edge66,Edge71,Edge78,Edge83,Edge90,Edge95,Edge102,Edge107,Edge114,Edge119,Edge126,Edge131,Edge138,Edge143]
FEATURE [Part::Cut] Cut020  label="top010"
  Base = -> Cut019
  Tool = -> Fillet022
FEATURE [Sketcher::SketchObject] Sketch032
  FullyConstrained = true
  Placement = pos=(117,19,0) rot=(0.57735,0.57735,0.57735;2.0944rad)
  sketch-geometry (48):
    g0: LineSegment StartX=-49.19 StartY=69.25 StartZ=0 EndX=-49.19 EndY=66.25 EndZ=0
    g1: LineSegment StartX=-49.19 StartY=63.5 StartZ=0 EndX=-49.19 EndY=60.5 EndZ=0
    g2: LineSegment StartX=-49.19 StartY=57.75 StartZ=0 EndX=-49.19 EndY=54.75 EndZ=0
    g3: LineSegment StartX=-49.19 StartY=52 StartZ=0 EndX=-49.19 EndY=49 EndZ=0
    g4: LineSegment StartX=-49.19 StartY=46.25 StartZ=0 EndX=-49.19 EndY=43.25 EndZ=0
    g5: LineSegment StartX=-49.19 StartY=40.5 StartZ=0 EndX=-49.19 EndY=37.5 EndZ=0
    g6: LineSegment StartX=-49.19 StartY=34.5 StartZ=0 EndX=-49.19 EndY=31.5 EndZ=0
    g7: LineSegment StartX=-49.19 StartY=28.75 StartZ=0 EndX=-49.19 EndY=25.75 EndZ=0
    g8: LineSegment StartX=-49.19 StartY=23 StartZ=0 EndX=-49.19 EndY=20 EndZ=0
    g9: LineSegment StartX=-49.19 StartY=17.25 StartZ=0 EndX=-49.19 EndY=14.25 EndZ=0
    g10: LineSegment StartX=-49.19 StartY=11.5 StartZ=0 EndX=-49.19 EndY=8.5 EndZ=0
    g11: LineSegment StartX=-49.19 StartY=5.75 StartZ=0 EndX=-49.19 EndY=2.75 EndZ=0
    g12: ArcOfCircle CenterX=-1.5 CenterY=67.75 CenterZ=0 NormalX=0 NormalY=0 NormalZ=1 AngleXU=0 Radius=1.5 StartAngle=4.71239 EndAngle=7.85398
    g13: ArcOfCircle CenterX=-1.5 CenterY=62 CenterZ=0 NormalX=0 NormalY=0 NormalZ=1 AngleXU=0 Radius=1.5 StartAngle=4.71239 EndAngle=7.85398
    g14: ArcOfCircle CenterX=-1.5 CenterY=56.25 CenterZ=0 NormalX=0 NormalY=0 NormalZ=1 AngleXU=0 Radius=1.5 StartAngle=4.71239 EndAngle=7.85398
    g15: ArcOfCircle CenterX=-11.49 CenterY=50.5 CenterZ=0 NormalX=0 NormalY=0 NormalZ=1 AngleXU=0 Radius=1.5 StartAngle=4.71239 EndAngle=7.85398
    g16: ArcOfCircle CenterX=-16.28 CenterY=44.75 CenterZ=0 NormalX=0 NormalY=0 NormalZ=1 AngleXU=0 Radius=1.5 StartAngle=4.71239 EndAngle=7.85398
    g17: ArcOfCircle CenterX=-18.2337 CenterY=39 CenterZ=0 NormalX=0 NormalY=0 NormalZ=1 AngleXU=0 Radius=1.5 StartAngle=4.71485 EndAngle=7.85398
    g18: ArcOfCircle CenterX=-16.2837 CenterY=27.25 CenterZ=0 NormalX=0 NormalY=0 NormalZ=1 AngleXU=0 Radius=1.5 StartAngle=4.71485 EndAngle=7.85398
    g19: ArcOfCircle CenterX=-18.2337 CenterY=33 CenterZ=0 NormalX=0 NormalY=0 NormalZ=1 AngleXU=0 Radius=1.5 StartAngle=4.71485 EndAngle=7.85398
    g20: ArcOfCircle CenterX=-11.49 CenterY=21.5 CenterZ=0 NormalX=0 NormalY=0 NormalZ=1 AngleXU=0 Radius=1.5 StartAngle=4.71239 EndAngle=7.85398
    g21: ArcOfCircle CenterX=-1.5 CenterY=4.25 CenterZ=0 NormalX=0 NormalY=0 NormalZ=1 AngleXU=0 Radius=1.5 StartAngle=4.71239 EndAngle=7.85398
    g22: ArcOfCircle CenterX=-1.5 CenterY=10 CenterZ=0 NormalX=0 NormalY=0 NormalZ=1 AngleXU=0 Radius=1.5 StartAngle=4.71239 EndAngle=7.85398
    g23: ArcOfCircle CenterX=-1.5 CenterY=15.75 CenterZ=0 NormalX=0 NormalY=0 NormalZ=1 AngleXU=0 Radius=1.5 StartAngle=4.71239 EndAngle=7.85398
    g24: LineSegment StartX=-49.19 StartY=69.25 StartZ=0 EndX=-1.5 EndY=69.25 EndZ=0
    g25: LineSegment StartX=-49.19 StartY=66.25 StartZ=0 EndX=-1.5 EndY=66.25 EndZ=0
    g26: LineSegment StartX=-49.19 StartY=63.5 StartZ=0 EndX=-1.5 EndY=63.5 EndZ=0
    g27: LineSegment StartX=-49.19 StartY=60.5 StartZ=0 EndX=-1.5 EndY=60.5 EndZ=0
    g28: LineSegment StartX=-49.19 StartY=57.75 StartZ=0 EndX=-1.5 EndY=57.75 EndZ=0
    g29: LineSegment StartX=-49.19 StartY=54.75 StartZ=0 EndX=-1.5 EndY=54.75 EndZ=0
    g30: LineSegment StartX=-49.19 StartY=52 StartZ=0 EndX=-11.49 EndY=52 EndZ=0
    g31: LineSegment StartX=-49.19 StartY=49 StartZ=0 EndX=-11.49 EndY=49 EndZ=0
    g32: LineSegment StartX=-49.19 StartY=46.25 StartZ=0 EndX=-16.28 EndY=46.25 EndZ=0
    g33: LineSegment StartX=-49.19 StartY=43.25 StartZ=0 EndX=-16.28 EndY=43.25 EndZ=0
    g34: LineSegment StartX=-49.19 StartY=40.5 StartZ=0 EndX=-18.2337 EndY=40.5 EndZ=0
    g35: LineSegment StartX=-49.19 StartY=37.5 StartZ=0 EndX=-18.23 EndY=37.5 EndZ=0
    g36: LineSegment StartX=-49.19 StartY=34.5 StartZ=0 EndX=-18.2337 EndY=34.5 EndZ=0
    g37: LineSegment StartX=-49.19 StartY=31.5 StartZ=0 EndX=-18.23 EndY=31.5 EndZ=0
    g38: LineSegment StartX=-49.19 StartY=28.75 StartZ=0 EndX=-16.2837 EndY=28.75 EndZ=0
    g39: LineSegment StartX=-49.19 StartY=25.75 StartZ=0 EndX=-16.28 EndY=25.75 EndZ=0
    g40: LineSegment StartX=-49.19 StartY=23 StartZ=0 EndX=-11.49 EndY=23 EndZ=0
    g41: LineSegment StartX=-49.19 StartY=20 StartZ=0 EndX=-11.49 EndY=20 EndZ=0
    g42: LineSegment StartX=-49.19 StartY=17.25 StartZ=0 EndX=-1.5 EndY=17.25 EndZ=0
    g43: LineSegment StartX=-49.19 StartY=14.25 StartZ=0 EndX=-1.5 EndY=14.25 EndZ=0
    g44: LineSegment StartX=-49.19 StartY=11.5 StartZ=0 EndX=-1.5 EndY=11.5 EndZ=0
    g45: LineSegment StartX=-49.19 StartY=8.5 StartZ=0 EndX=-1.5 EndY=8.5 EndZ=0
    g46: LineSegment StartX=-49.19 StartY=5.75 StartZ=0 EndX=-1.5 EndY=5.75 EndZ=0
    g47: LineSegment StartX=-49.19 StartY=2.75 StartZ=0 EndX=-1.5 EndY=2.75 EndZ=0
  constraints (120):
    c: Vertical(g0)
    c: Distance(g0) = 3
    c: Block(g0)
    c: Vertical(g1)
    c: Distance(g1) = 3
    c: Vertical(g2)
    c: Equal(g0,g2) = 3
    c: Block(g2)
    c: Vertical(g3)
    c: Equal(g1,g3) = 3
    c: Vertical(g4)
    c: Equal(g0,g4) = 3
    c: Block(g4)
    c: Vertical(g5)
    c: Equal(g1,g5) = 3
    c: Vertical(g6)
    c: Equal(g0,g6) = 3
    c: Block(g6)
    c: Vertical(g7)
    c: Equal(g1,g7) = 3
    c: Vertical(g8)
    c: Equal(g0,g8) = 3
    c: Block(g8)
    c: Vertical(g9)
    c: Equal(g1,g9) = 3
    c: Vertical(g10)
    c: Equal(g0,g10) = 3
    c: Block(g10)
    c: Vertical(g11)
    c: Equal(g1,g11) = 3
    c: Block(g12)
    c: Block(g13)
    c: Block(g14)
    c: Block(g15)
    c: Block(g16)
    c: Block(g17)
    c: Block(g18)
    c: Block(g19)
    c: Block(g20)
    c: Block(g21)
    c: Block(g22)
    c: Block(g23)
    c: Block(g11)
    c: Block(g9)
    c: Block(g7)
    c: Block(g5)
    c: Block(g3)
    c: Block(g1)
    c: Coincident(g24,g0)
    c: Coincident(g24,g12)
    c: Horizontal(g24)
    c: Coincident(g25,g0)
    c: Coincident(g25,g12)
    c: Horizontal(g25)
    c: Coincident(g26,g1)
    c: Coincident(g26,g13)
    c: Horizontal(g26)
    c: Coincident(g27,g1)
    c: Coincident(g27,g13)
    c: Horizontal(g27)
    c: Coincident(g28,g2)
    c: Coincident(g28,g14)
    c: Horizontal(g28)
    c: Coincident(g29,g2)
    c: Coincident(g29,g14)
    c: Horizontal(g29)
    c: Coincident(g30,g3)
    c: Coincident(g30,g15)
    c: Horizontal(g30)
    c: Coincident(g31,g3)
    c: Coincident(g31,g15)
    c: Horizontal(g31)
    c: Coincident(g32,g4)
    c: Coincident(g32,g16)
    c: Horizontal(g32)
    c: Coincident(g33,g4)
    c: Coincident(g33,g16)
    c: Horizontal(g33)
    c: Coincident(g34,g5)
    c: Coincident(g34,g17)
    c: Horizontal(g34)
    c: Coincident(g35,g5)
    c: Coincident(g35,g17)
    c: Horizontal(g35)
    c: Coincident(g36,g6)
    c: Coincident(g36,g19)
    c: Horizontal(g36)
    c: Coincident(g37,g6)
    c: Coincident(g37,g19)
    c: Horizontal(g37)
    c: Coincident(g38,g7)
    c: Coincident(g38,g18)
    c: Horizontal(g38)
    c: Coincident(g39,g7)
    c: Coincident(g39,g18)
    c: Horizontal(g39)
    c: Coincident(g40,g8)
    c: Coincident(g40,g20)
    c: Horizontal(g40)
    c: Coincident(g41,g8)
    c: Coincident(g41,g20)
    c: Horizontal(g41)
    c: Coincident(g42,g9)
    c: Coincident(g42,g23)
    c: Horizontal(g42)
    c: Coincident(g43,g9)
    c: Coincident(g43,g23)
    c: Horizontal(g43)
    c: Coincident(g44,g10)
    c: Coincident(g44,g22)
    c: Horizontal(g44)
    c: Coincident(g45,g10)
    c: Coincident(g45,g22)
    c: Horizontal(g45)
    c: Coincident(g46,g11)
    c: Coincident(g46,g21)
    c: Horizontal(g46)
    c: Coincident(g47,g11)
    c: Coincident(g47,g21)
    c: Horizontal(g47)
FEATURE [Part::Extrusion] Extrude023
  Base = -> Sketch032
  Dir = (1,-2e-16,2e-16)
  DirMode = 2
  FaceMakerClass = Part::FaceMakerBullseye
  LengthFwd = 19
  LengthRev = 0
  Placement = pos=(-19,0,0) rot=(0,0,1;0rad)
  Solid = true
  Symmetric = false
FEATURE [Part::Fillet] Fillet023
  Base = -> Extrude023
  Edges = <same value as first occurrence — deduplicated (x4 in doc)>
  Placement = pos=(0,0.05,0) rot=(0,0,1;0rad)
FEATURE [Part::Cut] Cut014  label="bottom003"
  Base = -> Cut007
  Tool = -> Fusion047
FEATURE [Part::Cut] Cut021  label="bottom004"
  Base = -> Cut014
  Tool = -> Fillet023
FEATURE [Sketcher::SketchObject] Sketch033
  FullyConstrained = true
  Placement = pos=(117,19,0) rot=(0.57735,0.57735,0.57735;2.0944rad)
  sketch-geometry (8):
    g0: LineSegment StartX=-49.19 StartY=69.25 StartZ=0 EndX=-49.19 EndY=66.25 EndZ=0
    g1: LineSegment StartX=-49.19 StartY=5.75 StartZ=0 EndX=-49.19 EndY=2.75 EndZ=0
    g2: ArcOfCircle CenterX=-1.5 CenterY=67.75 CenterZ=0 NormalX=0 NormalY=0 NormalZ=1 AngleXU=0 Radius=1.5 StartAngle=4.71239 EndAngle=7.85398
    g3: ArcOfCircle CenterX=-1.5 CenterY=4.25 CenterZ=0 NormalX=0 NormalY=0 NormalZ=1 AngleXU=0 Radius=1.5 StartAngle=4.71239 EndAngle=7.85398
    g4: LineSegment StartX=-49.19 StartY=69.25 StartZ=0 EndX=-1.5 EndY=69.25 EndZ=0
    g5: LineSegment StartX=-49.19 StartY=66.25 StartZ=0 EndX=-1.5 EndY=66.25 EndZ=0
    g6: LineSegment StartX=-49.19 StartY=5.75 StartZ=0 EndX=-1.5 EndY=5.75 EndZ=0
    g7: LineSegment StartX=-49.19 StartY=2.75 StartZ=0 EndX=-1.5 EndY=2.75 EndZ=0
  constraints (19):
    c: Vertical(g0)
    c: Distance(g0) = 3
    c: Block(g0)
    c: Vertical(g1)
    c: Block(g2)
    c: Block(g3)
    c: Block(g1)
    c: Coincident(g4,g0)
    c: Coincident(g4,g2)
    c: Horizontal(g4)
    c: Coincident(g5,g0)
    c: Coincident(g5,g2)
    c: Horizontal(g5)
    c: Coincident(g6,g1)
    c: Coincident(g6,g3)
    c: Horizontal(g6)
    c: Coincident(g7,g1)
    c: Coincident(g7,g3)
    c: Horizontal(g7)
FEATURE [Sketcher::SketchObject] Sketch034
  FullyConstrained = true
  Placement = pos=(117,19,0) rot=(0.57735,0.57735,0.57735;2.0944rad)
  sketch-geometry (8):
    g0: LineSegment StartX=-49.19 StartY=63.5 StartZ=0 EndX=-49.19 EndY=60.5 EndZ=0
    g1: LineSegment StartX=-49.19 StartY=11.5 StartZ=0 EndX=-49.19 EndY=8.5 EndZ=0
    g2: ArcOfCircle CenterX=-1.5 CenterY=62 CenterZ=0 NormalX=0 NormalY=0 NormalZ=1 AngleXU=0 Radius=1.5 StartAngle=4.71239 EndAngle=7.85398
    g3: ArcOfCircle CenterX=-1.5 CenterY=10 CenterZ=0 NormalX=0 NormalY=0 NormalZ=1 AngleXU=0 Radius=1.5 StartAngle=4.71239 EndAngle=7.85398
    g4: LineSegment StartX=-49.19 StartY=63.5 StartZ=0 EndX=-1.5 EndY=63.5 EndZ=0
    g5: LineSegment StartX=-49.19 StartY=60.5 StartZ=0 EndX=-1.5 EndY=60.5 EndZ=0
    g6: LineSegment StartX=-49.19 StartY=11.5 StartZ=0 EndX=-1.5 EndY=11.5 EndZ=0
    g7: LineSegment StartX=-49.19 StartY=8.5 StartZ=0 EndX=-1.5 EndY=8.5 EndZ=0
  constraints (19):
    c: Vertical(g0)
    c: Distance(g0) = 3
    c: Vertical(g1)
    c: Block(g1)
    c: Block(g2)
    c: Block(g3)
    c: Block(g0)
    c: Coincident(g4,g0)
    c: Coincident(g4,g2)
    c: Horizontal(g4)
    c: Coincident(g5,g0)
    c: Coincident(g5,g2)
    c: Horizontal(g5)
    c: Coincident(g6,g1)
    c: Coincident(g6,g3)
    c: Horizontal(g6)
    c: Coincident(g7,g1)
    c: Coincident(g7,g3)
    c: Horizontal(g7)
FEATURE [Part::Extrusion] Extrude024
  Base = -> Sketch033
  Dir = (1,0,0)
  DirMode = 2
  FaceMakerClass = Part::FaceMakerBullseye
  LengthFwd = 10
  LengthRev = 0
  Solid = true
  Symmetric = false
FEATURE [Part::Extrusion] Extrude025
  Base = -> Sketch034
  Dir = (1,0,0)
  DirMode = 2
  FaceMakerClass = Part::FaceMakerBullseye
  LengthFwd = 10
  LengthRev = 0
  Solid = true
  Symmetric = false
FEATURE [Part::Fillet] Fillet024  label="removeFromtMoreFrontCaseScrewRetainers"
  Base = -> Extrude024
  Edges = 4 edges r=1.49: [Edge6,Edge11,Edge18,Edge23]
  Placement = pos=(-11,0,0) rot=(0,0,1;0rad)
FEATURE [Part::Fillet] Fillet025  label="removeFromtMoreFrontCaseScrewRetainers001"
  Base = -> Extrude025
  Edges = 4 edges r=1.49: [Edge6,Edge11,Edge18,Edge23]
  Placement = pos=(-19,0,0) rot=(0,0,1;0rad)
FEATURE [Part::Cut] Cut022
  Base = -> Cut015
  Tool = -> Fillet025
FEATURE [Part::Cut] Cut023  label="screwRetainers"
  Base = -> Cut022
  Tool = -> Fillet024
FEATURE [Part::MultiFuse] Fusion056  label="bottom005"
  Shapes = -> [Fusion044,Cut021]
FEATURE [Part::MultiFuse] Fusion057  label="casePillars001"
  Shapes = -> [Cut016,Fusion052]
FEATURE [Part::MultiFuse] Fusion058  label="bottom006"
  Shapes = -> [Fusion056,Cut023]
FEATURE [Part::MultiFuse] Fusion059  label="bottom007"
  Shapes = -> [Fusion058,Fillet005]
FEATURE [Part::MultiFuse] Fusion060  label="bottom008"
  Shapes = -> [Fusion059,Fusion]
FEATURE [Part::MultiFuse] Fusion061  label="top011"
  Shapes = -> [Cut006,Cut020]
FEATURE [Part::MultiFuse] Fusion062  label="top012"
  Shapes = -> [Fusion057,Fusion061]
FEATURE [Sketcher::SketchObject] Sketch035  label="topSketch007"
  FullyConstrained = true
  sketch-geometry (6):
    g0: LineSegment StartX=19 StartY=38 StartZ=0 EndX=117 EndY=38 EndZ=0
    g1: ArcOfCircle CenterX=19 CenterY=19 CenterZ=0 NormalX=0 NormalY=0 NormalZ=1 AngleXU=0 Radius=19 StartAngle=1.5708 EndAngle=3.14159
    g2: LineSegment StartX=117 StartY=38 StartZ=0 EndX=117 EndY=19 EndZ=0
    g3: LineSegment StartX=98 StartY=1.0161e-12 StartZ=0 EndX=5.22862e-06 EndY=1.0161e-12 EndZ=0
    g4: LineSegment StartX=5.22862e-06 StartY=19 StartZ=0 EndX=5.22862e-06 EndY=1.0161e-12 EndZ=0
    g5: ArcOfCircle CenterX=98 CenterY=19 CenterZ=0 NormalX=0 NormalY=0 NormalZ=1 AngleXU=0 Radius=19 StartAngle=4.71239 EndAngle=6.28319
  constraints (16):
    c: Horizontal(g0)
    c: Distance(g0) = 98
    c: Coincident(g1,g0)
    c: Block(g1)
    c: Coincident(g2,g0)
    c: Vertical(g2)
    c: Distance(g2) = 19
    c: Horizontal(g3)
    c: Coincident(g4,g1)
    c: Vertical(g4)
    c: Coincident(g3,g4)
    c: Block(g3)
    c: Coincident(g5,g2)
    c: Coincident(g5,g3)
    c: Block(g0)
    c: Block(g5)
FEATURE [Part::Extrusion] Extrude026  label="sideA001"
  Base = -> Sketch035
  Dir = (0,0,1)
  DirMode = 2
  FaceMakerClass = Part::FaceMakerBullseye
  LengthFwd = 3
  LengthRev = 0
  Placement = pos=(0,0,-2.7) rot=(0,0,1;0rad)
  Solid = true
  Symmetric = false
FEATURE [Sketcher::SketchObject] Sketch036  label="topSketch008"
  FullyConstrained = true
  sketch-geometry (6):
    g0: LineSegment StartX=19 StartY=38 StartZ=0 EndX=117 EndY=38 EndZ=0
    g1: ArcOfCircle CenterX=19 CenterY=19 CenterZ=0 NormalX=0 NormalY=0 NormalZ=1 AngleXU=0 Radius=19 StartAngle=1.5708 EndAngle=3.14159
    g2: LineSegment StartX=117 StartY=38 StartZ=0 EndX=117 EndY=19 EndZ=0
    g3: LineSegment StartX=98 StartY=1.0161e-12 StartZ=0 EndX=5.22862e-06 EndY=1.0161e-12 EndZ=0
    g4: LineSegment StartX=5.22862e-06 StartY=19 StartZ=0 EndX=5.22862e-06 EndY=1.0161e-12 EndZ=0
    g5: ArcOfCircle CenterX=98 CenterY=19 CenterZ=0 NormalX=0 NormalY=0 NormalZ=1 AngleXU=0 Radius=19 StartAngle=4.71239 EndAngle=6.28319
  constraints (16):
    c: Horizontal(g0)
    c: Distance(g0) = 98
    c: Coincident(g1,g0)
    c: Block(g1)
    c: Coincident(g2,g0)
    c: Vertical(g2)
    c: Distance(g2) = 19
    c: Horizontal(g3)
    c: Coincident(g4,g1)
    c: Vertical(g4)
    c: Coincident(g3,g4)
    c: Block(g3)
    c: Coincident(g5,g2)
    c: Coincident(g5,g3)
    c: Block(g0)
    c: Block(g5)
FEATURE [Part::Extrusion] Extrude027  label="sideB001"
  Base = -> Sketch036
  Dir = (0,0,1)
  DirMode = 2
  FaceMakerClass = Part::FaceMakerBullseye
  LengthFwd = 3
  LengthRev = 0
  Placement = pos=(0,0,71.7) rot=(0,0,1;0rad)
  Solid = true
  Symmetric = false
FEATURE [Part::MultiFuse] Fusion064  label="removeFromBottom"
  Shapes = -> [Extrude026,Extrude027]
FEATURE [Part::Cut] Cut024  label="bottom009"
  Base = -> Fusion060
  Tool = -> Fusion064
FEATURE [Sketcher::SketchObject] Sketch037  label="topSketch009"
  FullyConstrained = true
  sketch-geometry (6):
    g0: ArcOfCircle CenterX=19 CenterY=19 CenterZ=0 NormalX=0 NormalY=0 NormalZ=1 AngleXU=0 Radius=19 StartAngle=1.5708 EndAngle=3.14159
    g1: LineSegment StartX=5.22862e-06 StartY=19 StartZ=0 EndX=5.22862e-06 EndY=1.19904e-11 EndZ=0
    g2: LineSegment StartX=19 StartY=38 StartZ=0 EndX=124 EndY=38 EndZ=0
    g3: LineSegment StartX=5.22862e-06 StartY=1.19904e-11 StartZ=0 EndX=105 EndY=1.19904e-11 EndZ=0
    g4: ArcOfCircle CenterX=105 CenterY=19 CenterZ=0 NormalX=0 NormalY=0 NormalZ=1 AngleXU=0 Radius=19 StartAngle=4.71239 EndAngle=6.28319
    g5: LineSegment StartX=124 StartY=38 StartZ=0 EndX=124 EndY=19 EndZ=0
  constraints (16):
    c: Block(g0)
    c: Coincident(g1,g0)
    c: Vertical(g1)
    c: Horizontal(g2)
    c: Distance(g2) = 105
    c: Coincident(g2,g0)
    c: Distance(g1) = 19
    c: Coincident(g3,g1)
    c: Horizontal(g3)
    c: Distance(g3) = 105
    c: Block(g4)
    c: Coincident(g4,g3)
    c: Coincident(g5,g2)
    c: Coincident(g5,g4)
    c: Vertical(g5)
    c: Distance(g5) = 19
FEATURE [Part::Extrusion] Extrude028  label="sideB"
  Base = -> Sketch037
  Dir = (0,0,1)
  DirMode = 2
  FaceMakerClass = Part::FaceMakerBullseye
  LengthFwd = 3
  LengthRev = 0
  Placement = pos=(0,0,72) rot=(0,0,1;0rad)
  Solid = true
  Symmetric = false
FEATURE [Sketcher::SketchObject] Sketch038  label="topSketch010"
  FullyConstrained = true
  sketch-geometry (22):
    g0: LineSegment StartX=5.21097e-06 StartY=3 StartZ=0 EndX=5.21097e-06 EndY=19 EndZ=0
    g1: ArcOfCircle CenterX=19 CenterY=19 CenterZ=0 NormalX=0 NormalY=0 NormalZ=1 AngleXU=0 Radius=19 StartAngle=1.5708 EndAngle=3.14159
    g2: ArcOfCircle CenterX=19 CenterY=19 CenterZ=0 NormalX=0 NormalY=0 NormalZ=1 AngleXU=0 Radius=16 StartAngle=1.5708 EndAngle=3.14159
    g3: LineSegment StartX=114 StartY=35 StartZ=0 EndX=19 EndY=35 EndZ=0
    g4: LineSegment StartX=5.21097e-06 StartY=3 StartZ=0 EndX=5.21097e-06 EndY=0 EndZ=0
    g5: LineSegment StartX=3 StartY=0 StartZ=0 EndX=5.21097e-06 EndY=0 EndZ=0
    g6: LineSegment StartX=3 StartY=19 StartZ=0 EndX=3 EndY=0 EndZ=0
    g7: LineSegment StartX=19 StartY=38 StartZ=0 EndX=124 EndY=38 EndZ=0
    g8: Circle CenterX=119 CenterY=35 CenterZ=0 NormalX=0 NormalY=0 NormalZ=1 AngleXU=0 Radius=1
    g9: Circle CenterX=121 CenterY=35 CenterZ=0 NormalX=0 NormalY=0 NormalZ=1 AngleXU=0 Radius=1
    g10: Circle CenterX=121 CenterY=33 CenterZ=0 NormalX=0 NormalY=0 NormalZ=1 AngleXU=0 Radius=1
    g11: BSplineCurve PolesCount=3 KnotsCount=2 Degree=2 IsPeriodic=0
    g12: GeomPoint X=119 Y=35 Z=0
    g13: GeomPoint X=121 Y=33 Z=0
    g14: LineSegment StartX=119 StartY=35 StartZ=0 EndX=114 EndY=35 EndZ=0
    g15: ArcOfCircle CenterX=105 CenterY=19 CenterZ=0 NormalX=0 NormalY=0 NormalZ=1 AngleXU=0 Radius=16 StartAngle=5.60905 EndAngle=6.28319
    g16: LineSegment StartX=121 StartY=33 StartZ=0 EndX=121 EndY=19 EndZ=0
    g17: LineSegment StartX=117.5 StartY=9.01251 StartZ=0 EndX=121.163 EndY=9.0125 EndZ=0
    g18: ArcOfCircle CenterX=105 CenterY=19 CenterZ=0 NormalX=0 NormalY=0 NormalZ=1 AngleXU=0 Radius=20.6155 StartAngle=5.7297 EndAngle=6.28319
    g19: LineSegment StartX=121.163 StartY=9.0125 StartZ=0 EndX=122.538 EndY=8.16329 EndZ=0
    g20: LineSegment StartX=124 StartY=38 StartZ=0 EndX=125.616 EndY=38 EndZ=0
    g21: LineSegment StartX=125.616 StartY=19 StartZ=0 EndX=125.616 EndY=38 EndZ=0
  constraints (49):
    c: Vertical(g0)
    c: Block(g0)
    c: Coincident(g1,g0)
    c: Block(g1)
    c: Coincident(g2,g1)
    c: Block(g2)
    c: Coincident(g3,g2)
    c: Horizontal(g3)
    c: Tangent(g3,g2)
    c: Coincident(g4,g0)
    c: Distance(g4) = 3
    c: Vertical(g4)
    c: Coincident(g5,g4)
    c: Horizontal(g5)
    c: Coincident(g6,g2)
    c: Coincident(g6,g5)
    c: Vertical(g6)
    c: Horizontal(g7)
    c: Distance(g7) = 105
    c: Coincident(g7,g1)
    c: Block(g3)
    c: Weight(g8) = 1
    c: Equal(g8,g9)
    c: Equal(g8,g10)
    c: InternalAlignment(g8,g11)
    c: InternalAlignment(g9,g11)
    c: InternalAlignment(g10,g11)
    c: InternalAlignment(g12,g11)
    c: InternalAlignment(g13,g11)
    c: Block(g11)
    c: Coincident(g14,g11)
    c: Coincident(g14,g3)
    c: Horizontal(g14)
    c: Block(g15)
    c: Coincident(g16,g11)
    c: Coincident(g16,g15)
    c: Vertical(g16)
    c: Distance(g16) = 14
    c: Coincident(g17,g15)
    c: Block(g18)
    c: Coincident(g19,g18)
    c: Coincident(g20,g7)
    c: Horizontal(g20)
    c: Vertical(g21)
    c: Coincident(g20,g21)
    c: Block(g20)
    c: Block(g21)
    c: Block(g19)
    c: Block(g17)
FEATURE [Part::Extrusion] Extrude029
  Base = -> Sketch038
  Dir = (0,0,1)
  DirMode = 2
  FaceMakerClass = Part::FaceMakerBullseye
  LengthFwd = 72
  LengthRev = 0
  Solid = true
  Symmetric = false
FEATURE [Part::Feature] Face085
  shape: bbox 4.8 x 25.5 x 2e-07 mm, 1 faces, 0 solids (baked)
FEATURE [Part::Revolution] Revolve089  label="moreFrontCaseScrewPost003"
  Angle = 360
  Axis = (0,1,0)
  Base = (0,0,0)
  FaceMakerClass = Part::FaceMakerBullseye
  Placement = pos=(109.5,4.5,3.5) rot=(0,0,1;0rad)
  Solid = false
  Source = -> Face085
  Symmetric = false
FEATURE [Part::Feature] Face086
  shape: bbox 4.8 x 25.5 x 2e-07 mm, 1 faces, 0 solids (baked)
FEATURE [Part::Revolution] Revolve090  label="moreFrontCaseScrewPost004"
  Angle = 360
  Axis = (0,1,0)
  Base = (0,0,0)
  FaceMakerClass = Part::FaceMakerBullseye
  Placement = pos=(109.5,4.5,68.5) rot=(0,0,1;0rad)
  Solid = false
  Source = -> Face086
  Symmetric = false
FEATURE [Part::Fillet] Fillet026  label="top013"
  Base = -> Extrude029
  Edges = 1 edges r=2: [Edge35]
FEATURE [Sketcher::SketchObject] Sketch039
  FullyConstrained = true
  sketch-geometry (7):
    g0: LineSegment StartX=0 StartY=0 StartZ=0 EndX=0 EndY=6 EndZ=0
    g1: Circle CenterX=0 CenterY=0 CenterZ=0 NormalX=0 NormalY=0 NormalZ=1 AngleXU=0 Radius=1
    g2: Circle CenterX=8 CenterY=6 CenterZ=0 NormalX=0 NormalY=0 NormalZ=1 AngleXU=0 Radius=1
    g3: BSplineCurve PolesCount=3 KnotsCount=2 Degree=2 IsPeriodic=0
    g4: GeomPoint X=0 Y=0 Z=0
    g5: GeomPoint X=8 Y=6 Z=0
    g6: LineSegment StartX=0 StartY=6 StartZ=0 EndX=8 EndY=6 EndZ=0
  constraints (14):
    c: Coincident(g0,g-1)
    c: Distance(g0) = 6
    c: Vertical(g0)
    c: Coincident(g3,g0)
    c: Weight(g1) = 1
    c: Equal(g1,g2)
    c: InternalAlignment(g1,g3)
    c: InternalAlignment(g2,g3)
    c: InternalAlignment(g4,g3)
    c: InternalAlignment(g5,g3)
    c: Block(g3)
    c: Coincident(g6,g0)
    c: Coincident(g6,g3)
    c: Horizontal(g6)
FEATURE [Sketcher::SketchObject] Sketch040
  FullyConstrained = true
  sketch-geometry (7):
    g0: LineSegment StartX=0 StartY=0 StartZ=0 EndX=0 EndY=6 EndZ=0
    g1: Circle CenterX=0 CenterY=0 CenterZ=0 NormalX=0 NormalY=0 NormalZ=1 AngleXU=0 Radius=1
    g2: Circle CenterX=8 CenterY=6 CenterZ=0 NormalX=0 NormalY=0 NormalZ=1 AngleXU=0 Radius=1
    g3: BSplineCurve PolesCount=3 KnotsCount=2 Degree=2 IsPeriodic=0
    g4: GeomPoint X=0 Y=0 Z=0
    g5: GeomPoint X=8 Y=6 Z=0
    g6: LineSegment StartX=0 StartY=6 StartZ=0 EndX=8 EndY=6 EndZ=0
  constraints (14):
    c: Coincident(g0,g-1)
    c: Distance(g0) = 6
    c: Vertical(g0)
    c: Coincident(g3,g0)
    c: Weight(g1) = 1
    c: Equal(g1,g2)
    c: InternalAlignment(g1,g3)
    c: InternalAlignment(g2,g3)
    c: InternalAlignment(g4,g3)
    c: InternalAlignment(g5,g3)
    c: Block(g3)
    c: Coincident(g6,g0)
    c: Coincident(g6,g3)
    c: Horizontal(g6)
FEATURE [Sketcher::SketchObject] Sketch041
  FullyConstrained = true
  sketch-geometry (7):
    g0: LineSegment StartX=0 StartY=0 StartZ=0 EndX=0 EndY=6 EndZ=0
    g1: Circle CenterX=0 CenterY=0 CenterZ=0 NormalX=0 NormalY=0 NormalZ=1 AngleXU=0 Radius=1
    g2: Circle CenterX=8 CenterY=6 CenterZ=0 NormalX=0 NormalY=0 NormalZ=1 AngleXU=0 Radius=1
    g3: BSplineCurve PolesCount=3 KnotsCount=2 Degree=2 IsPeriodic=0
    g4: GeomPoint X=0 Y=0 Z=0
    g5: GeomPoint X=8 Y=6 Z=0
    g6: LineSegment StartX=0 StartY=6 StartZ=0 EndX=8 EndY=6 EndZ=0
  constraints (14):
    c: Coincident(g0,g-1)
    c: Distance(g0) = 6
    c: Vertical(g0)
    c: Coincident(g3,g0)
    c: Weight(g1) = 1
    c: Equal(g1,g2)
    c: InternalAlignment(g1,g3)
    c: InternalAlignment(g2,g3)
    c: InternalAlignment(g4,g3)
    c: InternalAlignment(g5,g3)
    c: Block(g3)
    c: Coincident(g6,g0)
    c: Coincident(g6,g3)
    c: Horizontal(g6)
FEATURE [Sketcher::SketchObject] Sketch042
  FullyConstrained = true
  sketch-geometry (7):
    g0: LineSegment StartX=0 StartY=0 StartZ=0 EndX=0 EndY=6 EndZ=0
    g1: Circle CenterX=0 CenterY=0 CenterZ=0 NormalX=0 NormalY=0 NormalZ=1 AngleXU=0 Radius=1
    g2: Circle CenterX=8 CenterY=6 CenterZ=0 NormalX=0 NormalY=0 NormalZ=1 AngleXU=0 Radius=1
    g3: BSplineCurve PolesCount=3 KnotsCount=2 Degree=2 IsPeriodic=0
    g4: GeomPoint X=0 Y=0 Z=0
    g5: GeomPoint X=8 Y=6 Z=0
    g6: LineSegment StartX=0 StartY=6 StartZ=0 EndX=8 EndY=6 EndZ=0
  constraints (14):
    c: Coincident(g0,g-1)
    c: Distance(g0) = 6
    c: Vertical(g0)
    c: Coincident(g3,g0)
    c: Weight(g1) = 1
    c: Equal(g1,g2)
    c: InternalAlignment(g1,g3)
    c: InternalAlignment(g2,g3)
    c: InternalAlignment(g4,g3)
    c: InternalAlignment(g5,g3)
    c: Block(g3)
    c: Coincident(g6,g0)
    c: Coincident(g6,g3)
    c: Horizontal(g6)
FEATURE [Part::Extrusion] Extrude030  label="caseScrewPillarBracket008"
  Base = -> Sketch039
  Dir = (0,0,1)
  DirMode = 2
  FaceMakerClass = Part::FaceMakerBullseye
  LengthFwd = 2.4
  LengthRev = 0
  Placement = pos=(15.76,29,8.8) rot=(0,1,0;0rad)
  Solid = true
  Symmetric = false
FEATURE [Part::Extrusion] Extrude031  label="caseScrewPillarBracket009"
  Base = -> Sketch040
  Dir = (0,0,1)
  DirMode = 2
  FaceMakerClass = Part::FaceMakerBullseye
  LengthFwd = 2.4
  LengthRev = 0
  Placement = pos=(15.76,29,60.8) rot=(0,0,1;0rad)
  Solid = true
  Symmetric = false
FEATURE [Part::Extrusion] Extrude032  label="caseScrewPillarBracket010"
  Base = -> Sketch041
  Dir = (0,0,1)
  DirMode = 2
  FaceMakerClass = Part::FaceMakerBullseye
  LengthFwd = 2.4
  LengthRev = 0
  Placement = pos=(13.7,29,13.26) rot=(0,-1,0;1.5708rad)
  Solid = true
  Symmetric = false
FEATURE [Part::Extrusion] Extrude033  label="caseScrewPillarBracket011"
  Base = -> Sketch042
  Dir = (0,0,1)
  DirMode = 2
  FaceMakerClass = Part::FaceMakerBullseye
  LengthFwd = 2.4
  LengthRev = 0
  Placement = pos=(11.3,29,58.74) rot=(0,1,0;1.5708rad)
  Solid = true
  Symmetric = false
FEATURE [Sketcher::SketchObject] Sketch043
  FullyConstrained = true
  sketch-geometry (7):
    g0: LineSegment StartX=0 StartY=0 StartZ=0 EndX=0 EndY=6 EndZ=0
    g1: Circle CenterX=0 CenterY=0 CenterZ=0 NormalX=0 NormalY=0 NormalZ=1 AngleXU=0 Radius=1
    g2: Circle CenterX=8 CenterY=6 CenterZ=0 NormalX=0 NormalY=0 NormalZ=1 AngleXU=0 Radius=1
    g3: BSplineCurve PolesCount=3 KnotsCount=2 Degree=2 IsPeriodic=0
    g4: GeomPoint X=0 Y=0 Z=0
    g5: GeomPoint X=8 Y=6 Z=0
    g6: LineSegment StartX=0 StartY=6 StartZ=0 EndX=8 EndY=6 EndZ=0
  constraints (14):
    c: Coincident(g0,g-1)
    c: Distance(g0) = 6
    c: Vertical(g0)
    c: Coincident(g3,g0)
    c: Weight(g1) = 1
    c: Equal(g1,g2)
    c: InternalAlignment(g1,g3)
    c: InternalAlignment(g2,g3)
    c: InternalAlignment(g4,g3)
    c: InternalAlignment(g5,g3)
    c: Block(g3)
    c: Coincident(g6,g0)
    c: Coincident(g6,g3)
    c: Horizontal(g6)
FEATURE [Part::Extrusion] Extrude034  label="caseScrewPillarBracket012"
  Base = -> Sketch043
  Dir = (0,0,1)
  DirMode = 2
  FaceMakerClass = Part::FaceMakerBullseye
  LengthFwd = 2.4
  LengthRev = 0
  Placement = pos=(88.3,29,65.23) rot=(0,1,0;1.5708rad)
  Solid = true
  Symmetric = false
FEATURE [Sketcher::SketchObject] Sketch044
  FullyConstrained = true
  sketch-geometry (7):
    g0: LineSegment StartX=0 StartY=0 StartZ=0 EndX=0 EndY=6 EndZ=0
    g1: Circle CenterX=0 CenterY=0 CenterZ=0 NormalX=0 NormalY=0 NormalZ=1 AngleXU=0 Radius=1
    g2: Circle CenterX=8 CenterY=6 CenterZ=0 NormalX=0 NormalY=0 NormalZ=1 AngleXU=0 Radius=1
    g3: BSplineCurve PolesCount=3 KnotsCount=2 Degree=2 IsPeriodic=0
    g4: GeomPoint X=0 Y=0 Z=0
    g5: GeomPoint X=8 Y=6 Z=0
    g6: LineSegment StartX=0 StartY=6 StartZ=0 EndX=8 EndY=6 EndZ=0
  constraints (14):
    c: Coincident(g0,g-1)
    c: Distance(g0) = 6
    c: Vertical(g0)
    c: Coincident(g3,g0)
    c: Weight(g1) = 1
    c: Equal(g1,g2)
    c: InternalAlignment(g1,g3)
    c: InternalAlignment(g2,g3)
    c: InternalAlignment(g4,g3)
    c: InternalAlignment(g5,g3)
    c: Block(g3)
    c: Coincident(g6,g0)
    c: Coincident(g6,g3)
    c: Horizontal(g6)
FEATURE [Part::Extrusion] Extrude035  label="caseScrewPillarBracket013"
  Base = -> Sketch044
  Dir = (0,0,1)
  DirMode = 2
  FaceMakerClass = Part::FaceMakerBullseye
  LengthFwd = 2.4
  LengthRev = 0
  Placement = pos=(90.7,29,6.77) rot=(0,-1,0;1.5708rad)
  Solid = true
  Symmetric = false
FEATURE [Sketcher::SketchObject] Sketch045
  FullyConstrained = true
  sketch-geometry (7):
    g0: LineSegment StartX=0 StartY=0 StartZ=0 EndX=0 EndY=6 EndZ=0
    g1: Circle CenterX=0 CenterY=0 CenterZ=0 NormalX=0 NormalY=0 NormalZ=1 AngleXU=0 Radius=1
    g2: Circle CenterX=8 CenterY=6 CenterZ=0 NormalX=0 NormalY=0 NormalZ=1 AngleXU=0 Radius=1
    g3: BSplineCurve PolesCount=3 KnotsCount=2 Degree=2 IsPeriodic=0
    g4: GeomPoint X=0 Y=0 Z=0
    g5: GeomPoint X=8 Y=6 Z=0
    g6: LineSegment StartX=0 StartY=6 StartZ=0 EndX=8 EndY=6 EndZ=0
  constraints (14):
    c: Coincident(g0,g-1)
    c: Distance(g0) = 6
    c: Vertical(g0)
    c: Coincident(g3,g0)
    c: Weight(g1) = 1
    c: Equal(g1,g2)
    c: InternalAlignment(g1,g3)
    c: InternalAlignment(g2,g3)
    c: InternalAlignment(g4,g3)
    c: InternalAlignment(g5,g3)
    c: Block(g3)
    c: Coincident(g6,g0)
    c: Coincident(g6,g3)
    c: Horizontal(g6)
FEATURE [Sketcher::SketchObject] Sketch046
  FullyConstrained = true
  sketch-geometry (7):
    g0: LineSegment StartX=0 StartY=0 StartZ=0 EndX=0 EndY=6 EndZ=0
    g1: Circle CenterX=0 CenterY=0 CenterZ=0 NormalX=0 NormalY=0 NormalZ=1 AngleXU=0 Radius=1
    g2: Circle CenterX=8 CenterY=6 CenterZ=0 NormalX=0 NormalY=0 NormalZ=1 AngleXU=0 Radius=1
    g3: BSplineCurve PolesCount=3 KnotsCount=2 Degree=2 IsPeriodic=0
    g4: GeomPoint X=0 Y=0 Z=0
    g5: GeomPoint X=8 Y=6 Z=0
    g6: LineSegment StartX=0 StartY=6 StartZ=0 EndX=8 EndY=6 EndZ=0
  constraints (14):
    c: Coincident(g0,g-1)
    c: Distance(g0) = 6
    c: Vertical(g0)
    c: Coincident(g3,g0)
    c: Weight(g1) = 1
    c: Equal(g1,g2)
    c: InternalAlignment(g1,g3)
    c: InternalAlignment(g2,g3)
    c: InternalAlignment(g4,g3)
    c: InternalAlignment(g5,g3)
    c: Block(g3)
    c: Coincident(g6,g0)
    c: Coincident(g6,g3)
    c: Horizontal(g6)
FEATURE [Part::Extrusion] Extrude036  label="caseScrewPillarBracket014"
  Base = -> Sketch045
  Dir = (0,0,1)
  DirMode = 2
  FaceMakerClass = Part::FaceMakerBullseye
  LengthFwd = 2.4
  LengthRev = 0
  Placement = pos=(110.7,29,6.77) rot=(0,-1,0;1.5708rad)
  Solid = true
  Symmetric = false
FEATURE [Part::Extrusion] Extrude037  label="caseScrewPillarBracket015"
  Base = -> Sketch046
  Dir = (0,0,1)
  DirMode = 2
  FaceMakerClass = Part::FaceMakerBullseye
  LengthFwd = 2.4
  LengthRev = 0
  Placement = pos=(108.3,29,65.23) rot=(0,1,0;1.5708rad)
  Solid = true
  Symmetric = false
FEATURE [Part::Box] Box013  label="frontCaseScrewPillarBracket002"
  AttacherType = Attacher::AttachEngine3D
  Height = 2.4
  Length = 22
  Placement = pos=(87,28,2.3) rot=(0,0,1;0rad)
  Width = 7
FEATURE [Part::Box] Box014  label="frontCaseScrewPillarBracket003"
  AttacherType = Attacher::AttachEngine3D
  Height = 2.4
  Length = 22
  Placement = pos=(87,28,67.3) rot=(0,0,1;0rad)
  Width = 7
FEATURE [Part::Feature] Face087
  shape: bbox 4.8 x 30.2 x 2e-07 mm, 1 faces, 0 solids (baked)
FEATURE [Part::Revolution] Revolve091  label="frontCaseScrewPost004"
  Angle = 360
  Axis = (0,1,0)
  Base = (0,0,0)
  FaceMakerClass = Part::FaceMakerBullseye
  Placement = pos=(89.5,4.5,3.5) rot=(0,0,1;0rad)
  Solid = false
  Source = -> Face087
  Symmetric = false
FEATURE [Part::Feature] Face088
  shape: bbox 4.8 x 30.2 x 2e-07 mm, 1 faces, 0 solids (baked)
FEATURE [Part::Revolution] Revolve092  label="frontCaseScrewPost005"
  Angle = 360
  Axis = (0,1,0)
  Base = (0,0,0)
  FaceMakerClass = Part::FaceMakerBullseye
  Placement = pos=(89.5,4.5,68.5) rot=(0,0,1;0rad)
  Solid = false
  Source = -> Face088
  Symmetric = false
FEATURE [Part::Feature] Face089
  shape: bbox 3.5 x 30.2 x 2e-07 mm, 1 faces, 0 solids (baked)
FEATURE [Part::Revolution] Revolve093  label="backCaseScrewPost002"
  Angle = 360
  Axis = (0,1,0)
  Base = (0,0,0)
  FaceMakerClass = Part::FaceMakerBullseye
  Placement = pos=(12.5,4.5,10) rot=(0,0,1;0rad)
  Solid = false
  Source = -> Face089
  Symmetric = false
FEATURE [Part::Feature] Face090
  shape: bbox 3.5 x 30.2 x 2e-07 mm, 1 faces, 0 solids (baked)
FEATURE [Part::Revolution] Revolve094  label="backCaseScrewPost003"
  Angle = 360
  Axis = (0,1,0)
  Base = (0,0,0)
  FaceMakerClass = Part::FaceMakerBullseye
  Placement = pos=(12.5,4.5,62) rot=(0,0,1;0rad)
  Solid = false
  Source = -> Face090
  Symmetric = false
FEATURE [Part::Box] Box015  label="Cube011"
  AttacherType = Attacher::AttachEngine3D
  Height = 28.8
  Length = 3
  Placement = pos=(107.3,28,21.6) rot=(0,0,1;0rad)
  Width = 7
FEATURE [Part::Box] Box016  label="Cube012"
  AttacherType = Attacher::AttachEngine3D
  Height = 3
  Length = 7.4
  Placement = pos=(107.3,28,18.6) rot=(0,0,1;0rad)
  Width = 7
FEATURE [Part::Box] Box017  label="Cube013"
  AttacherType = Attacher::AttachEngine3D
  Height = 3
  Length = 7.4
  Placement = pos=(107.3,28,50.4) rot=(0,0,1;0rad)
  Width = 7
FEATURE [Part::Cylinder] Cylinder024
  Angle = 360
  AttacherType = Attacher::AttachEngine3D
  Height = 20
  Placement = pos=(0,0,36.15) rot=(0,0,1;0rad)
  Radius = 14.3
FEATURE [Part::Cylinder] Cylinder025
  Angle = 360
  AttacherType = Attacher::AttachEngine3D
  Height = 10
  Placement = pos=(0,0,36.15) rot=(0,0,1;0rad)
  Radius = 4
FEATURE [Part::MultiFuse] Fusion066  label="removeToCreteHoleForPlugHousing009"
  Placement = pos=(70,19,36) rot=(0,1,0;1.5708rad)
  Shapes = -> [Cylinder024,Cylinder025]
FEATURE [Part::MultiFuse] Fusion065  label="plugHousingBracketHolder002"
  Shapes = -> [Box017,Box015,Box016]
FEATURE [Part::Cut] Cut025  label="plugHousingBracketHolder003"
  Base = -> Fusion065
  Placement = pos=(7,0,0) rot=(0,0,1;0rad)
  Tool = -> Fusion066
FEATURE [Sketcher::SketchObject] Sketch047
  FullyConstrained = false
  Placement = pos=(0,0,0) rot=(1,0,0;1.5708rad)
  sketch-geometry (24):
    g0: ArcOfCircle CenterX=-4 CenterY=-10.5 CenterZ=0 NormalX=0 NormalY=0 NormalZ=1 AngleXU=0 Radius=1.5 StartAngle=6e-16 EndAngle=3.14159
    g1: ArcOfCircle CenterX=-34.2 CenterY=-10.5 CenterZ=0 NormalX=0 NormalY=0 NormalZ=1 AngleXU=0 Radius=1.5 StartAngle=0 EndAngle=3.14159
    g2: ArcOfCircle CenterX=-34.2 CenterY=-27.7 CenterZ=0 NormalX=0 NormalY=0 NormalZ=1 AngleXU=0 Radius=1.5 StartAngle=3.14159 EndAngle=6.28319
    g3: ArcOfCircle CenterX=-4 CenterY=-27.7 CenterZ=0 NormalX=0 NormalY=0 NormalZ=1 AngleXU=0 Radius=1.5 StartAngle=3.1416 EndAngle=6.28319
    g4: ArcOfCircle CenterX=-10 CenterY=-4.3 CenterZ=0 NormalX=0 NormalY=0 NormalZ=1 AngleXU=0 Radius=1.5 StartAngle=2e-16 EndAngle=3.14159
    g5: ArcOfCircle CenterX=-16.1 CenterY=-1.8 CenterZ=0 NormalX=0 NormalY=0 NormalZ=1 AngleXU=0 Radius=1.5 StartAngle=5e-16 EndAngle=3.14159
    g6: ArcOfCircle CenterX=-22.1 CenterY=-1.8 CenterZ=0 NormalX=0 NormalY=0 NormalZ=1 AngleXU=0 Radius=1.5 StartAngle=5e-16 EndAngle=3.14159
    g7: ArcOfCircle CenterX=-28.2 CenterY=-4.3 CenterZ=0 NormalX=0 NormalY=0 NormalZ=1 AngleXU=0 Radius=1.5 StartAngle=2e-16 EndAngle=3.14159
    g8: ArcOfCircle CenterX=-10 CenterY=-33.9 CenterZ=0 NormalX=0 NormalY=0 NormalZ=1 AngleXU=0 Radius=1.5 StartAngle=3.14159 EndAngle=6.28319
    g9: ArcOfCircle CenterX=-16.1 CenterY=-36.4 CenterZ=0 NormalX=0 NormalY=0 NormalZ=1 AngleXU=0 Radius=1.5 StartAngle=3.14159 EndAngle=6.28319
    g10: ArcOfCircle CenterX=-22.1 CenterY=-36.4 CenterZ=0 NormalX=0 NormalY=0 NormalZ=1 AngleXU=0 Radius=1.5 StartAngle=3.14159 EndAngle=6.28319
    g11: ArcOfCircle CenterX=-28.2 CenterY=-33.9 CenterZ=0 NormalX=0 NormalY=0 NormalZ=1 AngleXU=0 Radius=1.5 StartAngle=3.14159 EndAngle=6.28319
    g12: LineSegment StartX=-35.7 StartY=-10.5 StartZ=0 EndX=-35.7 EndY=-27.7 EndZ=0
    g13: LineSegment StartX=-32.7 StartY=-10.5 StartZ=0 EndX=-32.7 EndY=-27.7 EndZ=0
    g14: LineSegment StartX=-29.7 StartY=-33.9 StartZ=0 EndX=-29.7 EndY=-4.3 EndZ=0
    g15: LineSegment StartX=-26.7 StartY=-33.9 StartZ=0 EndX=-26.7 EndY=-4.3 EndZ=0
    g16: LineSegment StartX=-2.5 StartY=-10.5 StartZ=0 EndX=-2.5 EndY=-27.7 EndZ=0
    g17: LineSegment StartX=-8.5 StartY=-4.3 StartZ=0 EndX=-8.5 EndY=-33.9 EndZ=0
    g18: LineSegment StartX=-5.5 StartY=-10.5 StartZ=0 EndX=-5.5 EndY=-27.7 EndZ=0
    g19: LineSegment StartX=-11.5 StartY=-4.3 StartZ=0 EndX=-11.5 EndY=-33.9 EndZ=0
    g20: LineSegment StartX=-14.6 StartY=-1.8 StartZ=0 EndX=-14.6 EndY=-36.4 EndZ=0
    g21: LineSegment StartX=-17.6 StartY=-1.8 StartZ=0 EndX=-17.6 EndY=-36.4 EndZ=0
    g22: LineSegment StartX=-20.6 StartY=-36.4 StartZ=0 EndX=-20.6 EndY=-1.8 EndZ=0
    g23: LineSegment StartX=-23.6 StartY=-1.8 StartZ=0 EndX=-23.6 EndY=-36.4 EndZ=0
  constraints (48):
    c: Block(g0)
    c: Block(g1)
    c: Block(g2)
    c: Block(g3)
    c: Block(g4)
    c: Block(g5)
    c: Block(g6)
    c: Block(g7)
    c: Block(g8)
    c: Block(g9)
    c: Block(g10)
    c: Block(g11)
    c: Coincident(g12,g1)
    c: Coincident(g12,g2)
    c: Vertical(g12)
    c: Coincident(g13,g1)
    c: Coincident(g13,g2)
    c: Vertical(g13)
    c: Coincident(g14,g11)
    c: Coincident(g14,g7)
    c: Vertical(g14)
    c: Coincident(g15,g11)
    c: Coincident(g15,g7)
    c: Vertical(g15)
    c: Coincident(g16,g0)
    c: Coincident(g16,g3)
    c: Vertical(g16)
    c: Coincident(g17,g4)
    c: Coincident(g17,g8)
    c: Vertical(g17)
    c: Coincident(g18,g0)
    c: Coincident(g18,g3)
    c: Vertical(g18)
    c: Coincident(g19,g4)
    c: Coincident(g19,g8)
    c: Vertical(g19)
    c: Coincident(g20,g5)
    c: Coincident(g20,g9)
    c: Vertical(g20)
    c: Coincident(g21,g5)
    c: Coincident(g21,g9)
    c: Vertical(g21)
    c: Coincident(g22,g10)
    c: Coincident(g22,g6)
    c: Vertical(g22)
    c: Coincident(g23,g6)
    c: Coincident(g23,g10)
    c: Vertical(g23)
FEATURE [Part::Extrusion] Extrude038  label="removeToCreateFanGrillHoles001"
  Base = -> Sketch047
  Dir = (0,-1,6e-16)
  DirMode = 2
  FaceMakerClass = Part::FaceMakerBullseye
  LengthFwd = 10
  LengthRev = 0
  Placement = pos=(65.4,44,54.82) rot=(0,0,1;0rad)
  Solid = true
  Symmetric = false
FEATURE [Part::Feature] Wire004
  shape: bbox 11 x 5.2 x 2e-07 mm, 0 faces, 0 solids (baked)
FEATURE [Part::Revolution] Revolve095
  Angle = 360
  Axis = (0,1,0)
  Base = (0,0,0)
  FaceMakerClass = Part::FaceMakerBullseye
  Placement = pos=(30.3,38,19.7) rot=(0,0,1;0rad)
  Solid = true
  Source = -> Wire004
  Symmetric = false
FEATURE [Part::Feature] Wire005
  shape: bbox 11 x 5.2 x 2e-07 mm, 0 faces, 0 solids (baked)
FEATURE [Part::Revolution] Revolve096
  Angle = 360
  Axis = (0,1,0)
  Base = (0,0,0)
  FaceMakerClass = Part::FaceMakerBullseye
  Placement = pos=(30.3,38,51.7) rot=(0,0,1;0rad)
  Solid = true
  Source = -> Wire005
  Symmetric = false
FEATURE [Part::Feature] Wire006
  shape: bbox 11 x 5.2 x 2e-07 mm, 0 faces, 0 solids (baked)
FEATURE [Part::Revolution] Revolve097
  Angle = 360
  Axis = (0,1,0)
  Base = (0,0,0)
  FaceMakerClass = Part::FaceMakerBullseye
  Placement = pos=(62.3,38,51.7) rot=(0,0,1;0rad)
  Solid = true
  Source = -> Wire006
  Symmetric = false
FEATURE [Part::Feature] Wire007
  shape: bbox 11 x 5.2 x 2e-07 mm, 0 faces, 0 solids (baked)
FEATURE [Part::Revolution] Revolve098
  Angle = 360
  Axis = (0,1,0)
  Base = (0,0,0)
  FaceMakerClass = Part::FaceMakerBullseye
  Placement = pos=(62.3,38,19.7) rot=(0,0,1;0rad)
  Solid = true
  Source = -> Wire007
  Symmetric = false
FEATURE [Part::MultiFuse] Fusion067  label="fanScrewHousing002"
  Shapes = -> [Revolve098,Revolve097,Revolve096,Revolve095]
FEATURE [Part::Feature] Face091 .. Face094  x4 (patterned run collapsed; names and placements below)
  shape: bbox 3.5 x 17.8 x 2e-07 mm, 1 faces, 0 solids (baked)
FEATURE [Part::Revolution] Revolve099  label="removeToCreateScrewAndThreadedInsertHole026"
  Angle = 360
  Axis = (0,1,0)
  Base = (0,0,0)
  FaceMakerClass = Part::FaceMakerBullseye
  Placement = pos=(62.3,30.3,19.7) rot=(0,0,1;0rad)
  Solid = false
  Source = -> Face091
  Symmetric = false
FEATURE [Part::Revolution] Revolve100  label="removeToCreateScrewAndThreadedInsertHole027"
  Angle = 360
  Axis = (0,1,0)
  Base = (0,0,0)
  FaceMakerClass = Part::FaceMakerBullseye
  Placement = pos=(62.3,30.3,51.7) rot=(0,0,1;0rad)
  Solid = false
  Source = -> Face092
  Symmetric = false
FEATURE [Part::Revolution] Revolve101  label="removeToCreateScrewAndThreadedInsertHole028"
  Angle = 360
  Axis = (0,1,0)
  Base = (0,0,0)
  FaceMakerClass = Part::FaceMakerBullseye
  Placement = pos=(30.3,30.3,19.7) rot=(0,0,1;0rad)
  Solid = false
  Source = -> Face093
  Symmetric = false
FEATURE [Part::Revolution] Revolve102  label="removeToCreateScrewAndThreadedInsertHole029"
  Angle = 360
  Axis = (0,1,0)
  Base = (0,0,0)
  FaceMakerClass = Part::FaceMakerBullseye
  Placement = pos=(30.3,30.3,51.7) rot=(0,0,1;0rad)
  Solid = false
  Source = -> Face094
  Symmetric = false
FEATURE [Part::MultiFuse] Fusion068  label="createThreadedInsertHolesForFan002"
  Shapes = -> [Revolve099,Revolve100,Revolve101,Revolve102]
FEATURE [Part::Cut] Cut026  label="fanScrewHousing003"
  Base = -> Fusion067
  Tool = -> Fusion068
FEATURE [Sketcher::SketchObject] Sketch048
  FullyConstrained = false
  Placement = pos=(0,0,0) rot=(1,0,0;1.5708rad)
  sketch-geometry (24):
    g0: ArcOfCircle CenterX=-4 CenterY=-10.5 CenterZ=0 NormalX=0 NormalY=0 NormalZ=1 AngleXU=0 Radius=1.5 StartAngle=6e-16 EndAngle=3.14159
    g1: ArcOfCircle CenterX=-34.2 CenterY=-10.5 CenterZ=0 NormalX=0 NormalY=0 NormalZ=1 AngleXU=0 Radius=1.5 StartAngle=0 EndAngle=3.14159
    g2: ArcOfCircle CenterX=-34.2 CenterY=-27.7 CenterZ=0 NormalX=0 NormalY=0 NormalZ=1 AngleXU=0 Radius=1.5 StartAngle=3.14159 EndAngle=6.28319
    g3: ArcOfCircle CenterX=-4 CenterY=-27.7 CenterZ=0 NormalX=0 NormalY=0 NormalZ=1 AngleXU=0 Radius=1.5 StartAngle=3.1416 EndAngle=6.28319
    g4: ArcOfCircle CenterX=-10 CenterY=-4.3 CenterZ=0 NormalX=0 NormalY=0 NormalZ=1 AngleXU=0 Radius=1.5 StartAngle=2e-16 EndAngle=3.14159
    g5: ArcOfCircle CenterX=-16.1 CenterY=-1.8 CenterZ=0 NormalX=0 NormalY=0 NormalZ=1 AngleXU=0 Radius=1.5 StartAngle=5e-16 EndAngle=3.14159
    g6: ArcOfCircle CenterX=-22.1 CenterY=-1.8 CenterZ=0 NormalX=0 NormalY=0 NormalZ=1 AngleXU=0 Radius=1.5 StartAngle=5e-16 EndAngle=3.14159
    g7: ArcOfCircle CenterX=-28.2 CenterY=-4.3 CenterZ=0 NormalX=0 NormalY=0 NormalZ=1 AngleXU=0 Radius=1.5 StartAngle=2e-16 EndAngle=3.14159
    g8: ArcOfCircle CenterX=-10 CenterY=-33.9 CenterZ=0 NormalX=0 NormalY=0 NormalZ=1 AngleXU=0 Radius=1.5 StartAngle=3.14159 EndAngle=6.28319
    g9: ArcOfCircle CenterX=-16.1 CenterY=-36.4 CenterZ=0 NormalX=0 NormalY=0 NormalZ=1 AngleXU=0 Radius=1.5 StartAngle=3.14159 EndAngle=6.28319
    g10: ArcOfCircle CenterX=-22.1 CenterY=-36.4 CenterZ=0 NormalX=0 NormalY=0 NormalZ=1 AngleXU=0 Radius=1.5 StartAngle=3.14159 EndAngle=6.28319
    g11: ArcOfCircle CenterX=-28.2 CenterY=-33.9 CenterZ=0 NormalX=0 NormalY=0 NormalZ=1 AngleXU=0 Radius=1.5 StartAngle=3.14159 EndAngle=6.28319
    g12: LineSegment StartX=-35.7 StartY=-10.5 StartZ=0 EndX=-35.7 EndY=-27.7 EndZ=0
    g13: LineSegment StartX=-32.7 StartY=-10.5 StartZ=0 EndX=-32.7 EndY=-27.7 EndZ=0
    g14: LineSegment StartX=-29.7 StartY=-33.9 StartZ=0 EndX=-29.7 EndY=-4.3 EndZ=0
    g15: LineSegment StartX=-26.7 StartY=-33.9 StartZ=0 EndX=-26.7 EndY=-4.3 EndZ=0
    g16: LineSegment StartX=-2.5 StartY=-10.5 StartZ=0 EndX=-2.5 EndY=-27.7 EndZ=0
    g17: LineSegment StartX=-8.5 StartY=-4.3 StartZ=0 EndX=-8.5 EndY=-33.9 EndZ=0
    g18: LineSegment StartX=-5.5 StartY=-10.5 StartZ=0 EndX=-5.5 EndY=-27.7 EndZ=0
    g19: LineSegment StartX=-11.5 StartY=-4.3 StartZ=0 EndX=-11.5 EndY=-33.9 EndZ=0
    g20: LineSegment StartX=-14.6 StartY=-1.8 StartZ=0 EndX=-14.6 EndY=-36.4 EndZ=0
    g21: LineSegment StartX=-17.6 StartY=-1.8 StartZ=0 EndX=-17.6 EndY=-36.4 EndZ=0
    g22: LineSegment StartX=-20.6 StartY=-36.4 StartZ=0 EndX=-20.6 EndY=-1.8 EndZ=0
    g23: LineSegment StartX=-23.6 StartY=-1.8 StartZ=0 EndX=-23.6 EndY=-36.4 EndZ=0
  constraints (48):
    c: Block(g0)
    c: Block(g1)
    c: Block(g2)
    c: Block(g3)
    c: Block(g4)
    c: Block(g5)
    c: Block(g6)
    c: Block(g7)
    c: Block(g8)
    c: Block(g9)
    c: Block(g10)
    c: Block(g11)
    c: Coincident(g12,g1)
    c: Coincident(g12,g2)
    c: Vertical(g12)
    c: Coincident(g13,g1)
    c: Coincident(g13,g2)
    c: Vertical(g13)
    c: Coincident(g14,g11)
    c: Coincident(g14,g7)
    c: Vertical(g14)
    c: Coincident(g15,g11)
    c: Coincident(g15,g7)
    c: Vertical(g15)
    c: Coincident(g16,g0)
    c: Coincident(g16,g3)
    c: Vertical(g16)
    c: Coincident(g17,g4)
    c: Coincident(g17,g8)
    c: Vertical(g17)
    c: Coincident(g18,g0)
    c: Coincident(g18,g3)
    c: Vertical(g18)
    c: Coincident(g19,g4)
    c: Coincident(g19,g8)
    c: Vertical(g19)
    c: Coincident(g20,g5)
    c: Coincident(g20,g9)
    c: Vertical(g20)
    c: Coincident(g21,g5)
    c: Coincident(g21,g9)
    c: Vertical(g21)
    c: Coincident(g22,g10)
    c: Coincident(g22,g6)
    c: Vertical(g22)
    c: Coincident(g23,g6)
    c: Coincident(g23,g10)
    c: Vertical(g23)
FEATURE [Part::Extrusion] Extrude039  label="removeToCreateFanGrillHoles002"
  Base = -> Sketch048
  Dir = (0,-1,6e-16)
  DirMode = 2
  FaceMakerClass = Part::FaceMakerBullseye
  LengthFwd = 10
  LengthRev = 0
  Placement = pos=(65.4,44,54.82) rot=(0,0,1;0rad)
  Solid = true
  Symmetric = false
FEATURE [Part::Cut] Cut027  label="fanScrewHousing004"
  Base = -> Cut026
  Tool = -> Extrude038
FEATURE [Part::Cut] Cut028  label="top014"
  Base = -> Fillet026
  Tool = -> Extrude039
FEATURE [Part::Feature] Face095 .. Face098  x4 (patterned run collapsed; names and placements below)
  shape: bbox 3.5 x 17.8 x 2e-07 mm, 1 faces, 0 solids (baked)
FEATURE [Part::Revolution] Revolve103  label="removeToCreateScrewAndThreadedInsertHole030"
  Angle = 360
  Axis = (0,1,0)
  Base = (0,0,0)
  FaceMakerClass = Part::FaceMakerBullseye
  Placement = pos=(62.3,30.3,19.7) rot=(0,0,1;0rad)
  Solid = false
  Source = -> Face095
  Symmetric = false
FEATURE [Part::Revolution] Revolve104  label="removeToCreateScrewAndThreadedInsertHole031"
  Angle = 360
  Axis = (0,1,0)
  Base = (0,0,0)
  FaceMakerClass = Part::FaceMakerBullseye
  Placement = pos=(62.3,30.3,51.7) rot=(0,0,1;0rad)
  Solid = false
  Source = -> Face096
  Symmetric = false
FEATURE [Part::Revolution] Revolve105  label="removeToCreateScrewAndThreadedInsertHole032"
  Angle = 360
  Axis = (0,1,0)
  Base = (0,0,0)
  FaceMakerClass = Part::FaceMakerBullseye
  Placement = pos=(30.3,30.3,19.7) rot=(0,0,1;0rad)
  Solid = false
  Source = -> Face097
  Symmetric = false
FEATURE [Part::Revolution] Revolve106  label="removeToCreateScrewAndThreadedInsertHole033"
  Angle = 360
  Axis = (0,1,0)
  Base = (0,0,0)
  FaceMakerClass = Part::FaceMakerBullseye
  Placement = pos=(30.3,30.3,51.7) rot=(0,0,1;0rad)
  Solid = false
  Source = -> Face098
  Symmetric = false
FEATURE [Part::MultiFuse] Fusion069  label="createThreadedInsertHolesForFan003"
  Shapes = -> [Revolve103,Revolve104,Revolve105,Revolve106]
FEATURE [Part::Cut] Cut029  label="top015"
  Base = -> Cut028
  Tool = -> Fusion054
FEATURE [Part::Cut] Cut030  label="fanScrewHousing005"
  Base = -> Cut027
  Tool = -> Fusion069
FEATURE [Part::Cylinder] Cylinder026  label="removeToCreteHoleForPlugHousing010"
  Angle = 360
  AttacherType = Attacher::AttachEngine3D
  Height = 20
  Placement = pos=(-2,19,36) rot=(0,1,0;1.5708rad)
  Radius = 14.3
FEATURE [Part::Box] Box018  label="removeToCreteHoleForPlugHousing011"
  AttacherType = Attacher::AttachEngine3D
  Height = 28.6
  Length = 10
  Placement = pos=(-2,0,21.7) rot=(0,0,1;0rad)
  Width = 19
FEATURE [Part::Box] Box019  label="wireHolderBottomCaseBit"
  AttacherType = Attacher::AttachEngine3D
  Height = 28
  Length = 3
  Placement = pos=(0,0,22) rot=(0,0,1;0rad)
  Width = 21
FEATURE [Part::Cylinder] Cylinder027  label="removeToCreteHoleForPlugHousing012"
  Angle = 360
  AttacherType = Attacher::AttachEngine3D
  Height = 20
  Placement = pos=(-2,19,36) rot=(0,1,0;1.5708rad)
  Radius = 14.3
FEATURE [Part::Cut] Cut031  label="wireHolderBottomCaseBit001"
  Base = -> Box019
  Tool = -> Cylinder027
FEATURE [Part::MultiFuse] Fusion070  label="removeToCreteHoleForPlugHousing013"
  Shapes = -> [Box018,Cylinder026]
FEATURE [Part::Cut] Cut032  label="top016"
  Base = -> Cut029
  Tool = -> Fusion070
FEATURE [Part::Cylinder] Cylinder028
  Angle = 360
  AttacherType = Attacher::AttachEngine3D
  Height = 20
  Placement = pos=(0,0,36.15) rot=(0,0,1;0rad)
  Radius = 14.3
FEATURE [Part::Cylinder] Cylinder029
  Angle = 360
  AttacherType = Attacher::AttachEngine3D
  Height = 10
  Placement = pos=(0,0,36.15) rot=(0,0,1;0rad)
  Radius = 4
FEATURE [Part::MultiFuse] Fusion071  label="removeToCreteHoleForPlugHousing014"
  Placement = pos=(70,19,36) rot=(0,1,0;1.5708rad)
  Shapes = -> [Cylinder028,Cylinder029]
FEATURE [Sketcher::SketchObject] Sketch049  label="topSketch011"
  FullyConstrained = true
  sketch-geometry (4):
    g0: ArcOfCircle CenterX=105 CenterY=19 CenterZ=0 NormalX=0 NormalY=0 NormalZ=1 AngleXU=0 Radius=20.6155 StartAngle=5.54125 EndAngle=6.28319
    g1: ArcOfCircle CenterX=105 CenterY=19 CenterZ=0 NormalX=0 NormalY=0 NormalZ=1 AngleXU=0 Radius=13 StartAngle=5.54125 EndAngle=6.28319
    g2: LineSegment StartX=118 StartY=19 StartZ=0 EndX=125.616 EndY=19 EndZ=0
    g3: LineSegment StartX=114.583 StartY=10.2157 StartZ=0 EndX=120.197 EndY=5.06982 EndZ=0
  constraints (7):
    c: Block(g0)
    c: Block(g1)
    c: Coincident(g2,g1)
    c: Coincident(g2,g0)
    c: Horizontal(g2)
    c: Coincident(g3,g1)
    c: Coincident(g3,g0)
FEATURE [Part::Box] Box020  label="removeToCreteHoleForPlugHousing015"
  AttacherType = Attacher::AttachEngine3D
  Height = 28.6
  Length = 20
  Placement = pos=(106.15,0,21.7) rot=(0,0,1;0rad)
  Width = 19
FEATURE [Part::MultiFuse] Fusion072  label="removeToCreteHoleForPlugHousing016"
  Shapes = -> [Box020,Fusion071]
FEATURE [Part::Cut] Cut033  label="removeToCreteHoleForPlugHousing017"
  Base = -> Cut032
  Tool = -> Fusion072
FEATURE [Part::Cylinder] Cylinder030
  Angle = 360
  AttacherType = Attacher::AttachEngine3D
  Height = 20
  Placement = pos=(0,0,36.15) rot=(0,0,1;0rad)
  Radius = 14.3
FEATURE [Part::Cylinder] Cylinder031
  Angle = 360
  AttacherType = Attacher::AttachEngine3D
  Height = 10
  Placement = pos=(0,0,36.15) rot=(0,0,1;0rad)
  Radius = 4
FEATURE [Part::Box] Box021  label="removeToCreteHoleForPlugHousing019"
  AttacherType = Attacher::AttachEngine3D
  Height = 28.6
  Length = 20
  Placement = pos=(106.15,0,21.7) rot=(0,0,1;0rad)
  Width = 19
FEATURE [Part::MultiFuse] Fusion074  label="removeToCreteHoleForPlugHousing020"
  Placement = pos=(70,19,36) rot=(0,1,0;1.5708rad)
  Shapes = -> [Cylinder030,Cylinder031]
FEATURE [Part::MultiFuse] Fusion073  label="removeToCreteHoleForPlugHousing018"
  Placement = pos=(0,0,28.3) rot=(0,0,1;0rad)
  Shapes = -> [Box021,Fusion074]
FEATURE [Part::Cylinder] Cylinder032
  Angle = 360
  AttacherType = Attacher::AttachEngine3D
  Height = 20
  Placement = pos=(0,0,36.15) rot=(0,0,1;0rad)
  Radius = 14.3
FEATURE [Part::Cylinder] Cylinder033
  Angle = 360
  AttacherType = Attacher::AttachEngine3D
  Height = 10
  Placement = pos=(0,0,36.15) rot=(0,0,1;0rad)
  Radius = 4
FEATURE [Part::Box] Box022  label="removeToCreteHoleForPlugHousing021"
  AttacherType = Attacher::AttachEngine3D
  Height = 28.6
  Length = 20
  Placement = pos=(106.15,0,21.7) rot=(0,0,1;0rad)
  Width = 19
FEATURE [Part::MultiFuse] Fusion076  label="removeToCreteHoleForPlugHousing023"
  Placement = pos=(70,19,36) rot=(0,1,0;1.5708rad)
  Shapes = -> [Cylinder032,Cylinder033]
FEATURE [Part::MultiFuse] Fusion075  label="removeToCreteHoleForPlugHousing022"
  Placement = pos=(0,0,-28.3) rot=(0,0,1;0rad)
  Shapes = -> [Box022,Fusion076]
FEATURE [Part::MultiFuse] Fusion077  label="removeToCreatePlugHousingBottomBit"
  Shapes = -> [Fusion075,Fusion073]
FEATURE [Part::Cylinder] Cylinder034
  Angle = 360
  AttacherType = Attacher::AttachEngine3D
  Height = 20
  Placement = pos=(0,0,36.15) rot=(0,0,1;0rad)
  Radius = 14.3
FEATURE [Part::Cylinder] Cylinder035
  Angle = 360
  AttacherType = Attacher::AttachEngine3D
  Height = 10
  Placement = pos=(0,0,36.15) rot=(0,0,1;0rad)
  Radius = 4
FEATURE [Part::MultiFuse] Fusion078  label="removeToCreteHoleForPlugHousing024"
  Placement = pos=(70,19,36) rot=(0,1,0;1.5708rad)
  Shapes = -> [Cylinder034,Cylinder035]
FEATURE [Part::MultiFuse] Fusion079  label="removeToCreatePlugHousingBottomBit001"
  Shapes = -> [Fusion078,Fusion077]
FEATURE [Part::Extrusion] Extrude040  label="bottomPlugHousingBit"
  Base = -> Sketch049
  Dir = (0,0,1)
  DirMode = 2
  FaceMakerClass = Part::FaceMakerBullseye
  LengthFwd = 72
  LengthRev = 0
  Solid = true
  Symmetric = false
FEATURE [Part::Cut] Cut034  label="bottomPlugHousingBit001"
  Base = -> Extrude040
  Tool = -> Fusion079
FEATURE [Part::Box] Box023  label="Cube014"
  AttacherType = Attacher::AttachEngine3D
  Height = 16
  Length = 8
  Placement = pos=(12.7,31.52,28) rot=(0,0,1;0rad)
  Width = 4
FEATURE [Part::Cylinder] Cylinder036
  Angle = 360
  AttacherType = Attacher::AttachEngine3D
  Height = 10
  Placement = pos=(0,0,36.15) rot=(0,0,1;0rad)
  Radius = 4
FEATURE [Part::Cylinder] Cylinder037
  Angle = 360
  AttacherType = Attacher::AttachEngine3D
  Height = 20
  Placement = pos=(0,0,36.15) rot=(0,0,1;0rad)
  Radius = 8.2
FEATURE [Part::MultiFuse] Fusion080  label="removeToCreteHoleForPlugHousing025"
  Placement = pos=(-42,19,36) rot=(0,1,0;1.5708rad)
  Shapes = -> [Cylinder037,Cylinder036]
FEATURE [Sketcher::SketchObject] Sketch050  label="topSketch012"
  FullyConstrained = true
  sketch-geometry (4):
    g0: LineSegment StartX=16.8446 StartY=31.512 StartZ=0 EndX=16.3251 EndY=34.4666 EndZ=0
    g1: ArcOfCircle CenterX=19 CenterY=19.2524 CenterZ=0 NormalX=0 NormalY=0 NormalZ=1 AngleXU=0 Radius=15.4476 StartAngle=1.74483 EndAngle=2.72717
    g2: ArcOfCircle CenterX=19 CenterY=19.2524 CenterZ=0 NormalX=0 NormalY=0 NormalZ=1 AngleXU=0 Radius=12.4476 StartAngle=1.74483 EndAngle=2.73189
    g3: LineSegment StartX=4.86004 StartY=25.4725 StartZ=0 EndX=7.58253 EndY=24.2107 EndZ=0
  constraints (7):
    c: Block(g0)
    c: Coincident(g1,g0)
    c: Coincident(g2,g0)
    c: Coincident(g3,g1)
    c: Coincident(g3,g2)
    c: Block(g1)
    c: Block(g2)
FEATURE [Part::Extrusion] Extrude041
  Base = -> Sketch050
  Dir = (0,0,1)
  DirMode = 2
  FaceMakerClass = Part::FaceMakerBullseye
  LengthFwd = 10.6
  LengthRev = 0
  Placement = pos=(0,0,31) rot=(0,0,1;0rad)
  Solid = true
  Symmetric = false
FEATURE [Part::Cut] Cut035
  Base = -> Extrude041
  Placement = pos=(0,0,-0.3) rot=(0,0,1;0rad)
  Tool = -> Fusion080
FEATURE [Part::Cut] Cut036
  Base = -> Box023
  Tool = -> Cut035
FEATURE [Part::Fillet] Fillet027
  Base = -> Cut036
  Edges = 1 edges r=0.7: [Edge13]
FEATURE [Part::Fillet] Fillet028
  Base = -> Fillet027
  Edges = 1 edges r=0.7: [Edge13]
FEATURE [Part::Fillet] Fillet029
  Base = -> Fillet028
  Edges = 1 edges r=0.7: [Edge16]
FEATURE [Part::Fillet] Fillet030
  Base = -> Fillet029
  Edges = 1 edges r=0.7: [Edge11]
FEATURE [Part::Fillet] Fillet031
  Base = -> Fillet030
  Edges = 1 edges r=0.7: [Edge10]
FEATURE [Part::Fillet] Fillet032
  Base = -> Fillet031
  Edges = 1 edges r=1.2: [Edge5]
FEATURE [Part::Fillet] Fillet033
  Base = -> Fillet032
  Edges = 1 edges r=1.2: [Edge12]
FEATURE [Part::Fillet] Fillet034  label="wireHousingRetainer"
  Base = -> Fillet033
  Edges = 1 edges r=2: [Edge1]
  Placement = pos=(0.3,0,0) rot=(0,0,1;0rad)
FEATURE [Part::Feature] Face099
  shape: bbox 3.5 x 17.8 x 2e-07 mm, 1 faces, 0 solids (baked)
FEATURE [Part::Revolution] Revolve107  label="removeToCreateScrewAndThreadedInsertHole034"
  Angle = 360
  Axis = (0,1,0)
  Base = (0,0,0)
  FaceMakerClass = Part::FaceMakerBullseye
  Placement = pos=(12.5,0,10) rot=(0,0,1;0rad)
  Solid = false
  Source = -> Face099
  Symmetric = false
FEATURE [Part::Feature] Face100
  shape: bbox 3.5 x 17.8 x 2e-07 mm, 1 faces, 0 solids (baked)
FEATURE [Part::Revolution] Revolve108  label="removeToCreateScrewAndThreadedInsertHole035"
  Angle = 360
  Axis = (0,1,0)
  Base = (0,0,0)
  FaceMakerClass = Part::FaceMakerBullseye
  Placement = pos=(12.5,0,62) rot=(0,0,1;0rad)
  Solid = false
  Source = -> Face100
  Symmetric = false
FEATURE [Part::Feature] Face101
  shape: bbox 3.5 x 17.8 x 2e-07 mm, 1 faces, 0 solids (baked)
FEATURE [Part::Revolution] Revolve109  label="removeToCreateScrewAndThreadedInsertHole036"
  Angle = 360
  Axis = (0,1,0)
  Base = (0,0,0)
  FaceMakerClass = Part::FaceMakerBullseye
  Placement = pos=(89.5,0,68.5) rot=(0,0,1;0rad)
  Solid = false
  Source = -> Face101
  Symmetric = false
FEATURE [Part::Feature] Face102
  shape: bbox 3.5 x 17.8 x 2e-07 mm, 1 faces, 0 solids (baked)
FEATURE [Part::Revolution] Revolve110  label="removeToCreateScrewAndThreadedInsertHole037"
  Angle = 360
  Axis = (0,1,0)
  Base = (0,0,0)
  FaceMakerClass = Part::FaceMakerBullseye
  Placement = pos=(89.5,0,3.5) rot=(0,0,1;0rad)
  Solid = false
  Source = -> Face102
  Symmetric = false
FEATURE [Part::Feature] Face103
  shape: bbox 3.5 x 17.8 x 2e-07 mm, 1 faces, 0 solids (baked)
FEATURE [Part::Revolution] Revolve111  label="removeToCreateScrewAndThreadedInsertHole038"
  Angle = 360
  Axis = (0,1,0)
  Base = (0,0,0)
  FaceMakerClass = Part::FaceMakerBullseye
  Placement = pos=(109.5,4.7,3.5) rot=(0,0,1;0rad)
  Solid = false
  Source = -> Face103
  Symmetric = false
FEATURE [Part::Feature] Face104
  shape: bbox 3.5 x 17.8 x 2e-07 mm, 1 faces, 0 solids (baked)
FEATURE [Part::Revolution] Revolve112  label="removeToCreateScrewAndThreadedInsertHole039"
  Angle = 360
  Axis = (0,1,0)
  Base = (0,0,0)
  FaceMakerClass = Part::FaceMakerBullseye
  Placement = pos=(109.5,4.7,68.5) rot=(0,0,1;0rad)
  Solid = false
  Source = -> Face104
  Symmetric = false
FEATURE [Part::MultiFuse] Fusion081  label="removeToCreateScrewAndThreadedInsertHole040"
  Shapes = -> [Revolve107,Revolve108,Revolve109,Revolve110,Revolve111,Revolve112]
FEATURE [Part::MultiFuse] Fusion082  label="casePillars002"
  Shapes = -> [Revolve094,Revolve092,Revolve090,Revolve089,Revolve091,Revolve093]
FEATURE [Part::Cut] Cut037  label="casePillars003"
  Base = -> Fusion082
  Tool = -> Fusion081
FEATURE [Sketcher::SketchObject] Sketch051
  FullyConstrained = true
  Placement = pos=(117,19,0) rot=(0.57735,0.57735,0.57735;2.0944rad)
  sketch-geometry (48):
    g0: LineSegment StartX=-49.19 StartY=69.25 StartZ=0 EndX=-49.19 EndY=66.25 EndZ=0
    g1: LineSegment StartX=-49.19 StartY=63.5 StartZ=0 EndX=-49.19 EndY=60.5 EndZ=0
    g2: LineSegment StartX=-49.19 StartY=57.75 StartZ=0 EndX=-49.19 EndY=54.75 EndZ=0
    g3: LineSegment StartX=-49.19 StartY=52 StartZ=0 EndX=-49.19 EndY=49 EndZ=0
    g4: LineSegment StartX=-49.19 StartY=46.25 StartZ=0 EndX=-49.19 EndY=43.25 EndZ=0
    g5: LineSegment StartX=-49.19 StartY=40.5 StartZ=0 EndX=-49.19 EndY=37.5 EndZ=0
    g6: LineSegment StartX=-49.19 StartY=34.5 StartZ=0 EndX=-49.19 EndY=31.5 EndZ=0
    g7: LineSegment StartX=-49.19 StartY=28.75 StartZ=0 EndX=-49.19 EndY=25.75 EndZ=0
    g8: LineSegment StartX=-49.19 StartY=23 StartZ=0 EndX=-49.19 EndY=20 EndZ=0
    g9: LineSegment StartX=-49.19 StartY=17.25 StartZ=0 EndX=-49.19 EndY=14.25 EndZ=0
    g10: LineSegment StartX=-49.19 StartY=11.5 StartZ=0 EndX=-49.19 EndY=8.5 EndZ=0
    g11: LineSegment StartX=-49.19 StartY=5.75 StartZ=0 EndX=-49.19 EndY=2.75 EndZ=0
    g12: ArcOfCircle CenterX=-1.5 CenterY=67.75 CenterZ=0 NormalX=0 NormalY=0 NormalZ=1 AngleXU=0 Radius=1.5 StartAngle=4.71239 EndAngle=7.85398
    g13: ArcOfCircle CenterX=-1.5 CenterY=62 CenterZ=0 NormalX=0 NormalY=0 NormalZ=1 AngleXU=0 Radius=1.5 StartAngle=4.71239 EndAngle=7.85398
    g14: ArcOfCircle CenterX=-1.5 CenterY=56.25 CenterZ=0 NormalX=0 NormalY=0 NormalZ=1 AngleXU=0 Radius=1.5 StartAngle=4.71239 EndAngle=7.85398
    g15: ArcOfCircle CenterX=-11.49 CenterY=50.5 CenterZ=0 NormalX=0 NormalY=0 NormalZ=1 AngleXU=0 Radius=1.5 StartAngle=4.71239 EndAngle=7.85398
    g16: ArcOfCircle CenterX=-16.28 CenterY=44.75 CenterZ=0 NormalX=0 NormalY=0 NormalZ=1 AngleXU=0 Radius=1.5 StartAngle=4.71239 EndAngle=7.85398
    g17: ArcOfCircle CenterX=-18.2337 CenterY=39 CenterZ=0 NormalX=0 NormalY=0 NormalZ=1 AngleXU=0 Radius=1.5 StartAngle=4.71485 EndAngle=7.85398
    g18: ArcOfCircle CenterX=-16.2837 CenterY=27.25 CenterZ=0 NormalX=0 NormalY=0 NormalZ=1 AngleXU=0 Radius=1.5 StartAngle=4.71485 EndAngle=7.85398
    g19: ArcOfCircle CenterX=-18.2337 CenterY=33 CenterZ=0 NormalX=0 NormalY=0 NormalZ=1 AngleXU=0 Radius=1.5 StartAngle=4.71485 EndAngle=7.85398
    g20: ArcOfCircle CenterX=-11.49 CenterY=21.5 CenterZ=0 NormalX=0 NormalY=0 NormalZ=1 AngleXU=0 Radius=1.5 StartAngle=4.71239 EndAngle=7.85398
    g21: ArcOfCircle CenterX=-1.5 CenterY=4.25 CenterZ=0 NormalX=0 NormalY=0 NormalZ=1 AngleXU=0 Radius=1.5 StartAngle=4.71239 EndAngle=7.85398
    g22: ArcOfCircle CenterX=-1.5 CenterY=10 CenterZ=0 NormalX=0 NormalY=0 NormalZ=1 AngleXU=0 Radius=1.5 StartAngle=4.71239 EndAngle=7.85398
    g23: ArcOfCircle CenterX=-1.5 CenterY=15.75 CenterZ=0 NormalX=0 NormalY=0 NormalZ=1 AngleXU=0 Radius=1.5 StartAngle=4.71239 EndAngle=7.85398
    g24: LineSegment StartX=-49.19 StartY=69.25 StartZ=0 EndX=-1.5 EndY=69.25 EndZ=0
    g25: LineSegment StartX=-49.19 StartY=66.25 StartZ=0 EndX=-1.5 EndY=66.25 EndZ=0
    g26: LineSegment StartX=-49.19 StartY=63.5 StartZ=0 EndX=-1.5 EndY=63.5 EndZ=0
    g27: LineSegment StartX=-49.19 StartY=60.5 StartZ=0 EndX=-1.5 EndY=60.5 EndZ=0
    g28: LineSegment StartX=-49.19 StartY=57.75 StartZ=0 EndX=-1.5 EndY=57.75 EndZ=0
    g29: LineSegment StartX=-49.19 StartY=54.75 StartZ=0 EndX=-1.5 EndY=54.75 EndZ=0
    g30: LineSegment StartX=-49.19 StartY=52 StartZ=0 EndX=-11.49 EndY=52 EndZ=0
    g31: LineSegment StartX=-49.19 StartY=49 StartZ=0 EndX=-11.49 EndY=49 EndZ=0
    g32: LineSegment StartX=-49.19 StartY=46.25 StartZ=0 EndX=-16.28 EndY=46.25 EndZ=0
    g33: LineSegment StartX=-49.19 StartY=43.25 StartZ=0 EndX=-16.28 EndY=43.25 EndZ=0
    g34: LineSegment StartX=-49.19 StartY=40.5 StartZ=0 EndX=-18.2337 EndY=40.5 EndZ=0
    g35: LineSegment StartX=-49.19 StartY=37.5 StartZ=0 EndX=-18.23 EndY=37.5 EndZ=0
    g36: LineSegment StartX=-49.19 StartY=34.5 StartZ=0 EndX=-18.2337 EndY=34.5 EndZ=0
    g37: LineSegment StartX=-49.19 StartY=31.5 StartZ=0 EndX=-18.23 EndY=31.5 EndZ=0
    g38: LineSegment StartX=-49.19 StartY=28.75 StartZ=0 EndX=-16.2837 EndY=28.75 EndZ=0
    g39: LineSegment StartX=-49.19 StartY=25.75 StartZ=0 EndX=-16.28 EndY=25.75 EndZ=0
    g40: LineSegment StartX=-49.19 StartY=23 StartZ=0 EndX=-11.49 EndY=23 EndZ=0
    g41: LineSegment StartX=-49.19 StartY=20 StartZ=0 EndX=-11.49 EndY=20 EndZ=0
    g42: LineSegment StartX=-49.19 StartY=17.25 StartZ=0 EndX=-1.5 EndY=17.25 EndZ=0
    g43: LineSegment StartX=-49.19 StartY=14.25 StartZ=0 EndX=-1.5 EndY=14.25 EndZ=0
    g44: LineSegment StartX=-49.19 StartY=11.5 StartZ=0 EndX=-1.5 EndY=11.5 EndZ=0
    g45: LineSegment StartX=-49.19 StartY=8.5 StartZ=0 EndX=-1.5 EndY=8.5 EndZ=0
    g46: LineSegment StartX=-49.19 StartY=5.75 StartZ=0 EndX=-1.5 EndY=5.75 EndZ=0
    g47: LineSegment StartX=-49.19 StartY=2.75 StartZ=0 EndX=-1.5 EndY=2.75 EndZ=0
  constraints (120):
    c: Vertical(g0)
    c: Distance(g0) = 3
    c: Block(g0)
    c: Vertical(g1)
    c: Distance(g1) = 3
    c: Vertical(g2)
    c: Equal(g0,g2) = 3
    c: Block(g2)
    c: Vertical(g3)
    c: Equal(g1,g3) = 3
    c: Vertical(g4)
    c: Equal(g0,g4) = 3
    c: Block(g4)
    c: Vertical(g5)
    c: Equal(g1,g5) = 3
    c: Vertical(g6)
    c: Equal(g0,g6) = 3
    c: Block(g6)
    c: Vertical(g7)
    c: Equal(g1,g7) = 3
    c: Vertical(g8)
    c: Equal(g0,g8) = 3
    c: Block(g8)
    c: Vertical(g9)
    c: Equal(g1,g9) = 3
    c: Vertical(g10)
    c: Equal(g0,g10) = 3
    c: Block(g10)
    c: Vertical(g11)
    c: Equal(g1,g11) = 3
    c: Block(g12)
    c: Block(g13)
    c: Block(g14)
    c: Block(g15)
    c: Block(g16)
    c: Block(g17)
    c: Block(g18)
    c: Block(g19)
    c: Block(g20)
    c: Block(g21)
    c: Block(g22)
    c: Block(g23)
    c: Block(g11)
    c: Block(g9)
    c: Block(g7)
    c: Block(g5)
    c: Block(g3)
    c: Block(g1)
    c: Coincident(g24,g0)
    c: Coincident(g24,g12)
    c: Horizontal(g24)
    c: Coincident(g25,g0)
    c: Coincident(g25,g12)
    c: Horizontal(g25)
    c: Coincident(g26,g1)
    c: Coincident(g26,g13)
    c: Horizontal(g26)
    c: Coincident(g27,g1)
    c: Coincident(g27,g13)
    c: Horizontal(g27)
    c: Coincident(g28,g2)
    c: Coincident(g28,g14)
    c: Horizontal(g28)
    c: Coincident(g29,g2)
    c: Coincident(g29,g14)
    c: Horizontal(g29)
    c: Coincident(g30,g3)
    c: Coincident(g30,g15)
    c: Horizontal(g30)
    c: Coincident(g31,g3)
    c: Coincident(g31,g15)
    c: Horizontal(g31)
    c: Coincident(g32,g4)
    c: Coincident(g32,g16)
    c: Horizontal(g32)
    c: Coincident(g33,g4)
    c: Coincident(g33,g16)
    c: Horizontal(g33)
    c: Coincident(g34,g5)
    c: Coincident(g34,g17)
    c: Horizontal(g34)
    c: Coincident(g35,g5)
    c: Coincident(g35,g17)
    c: Horizontal(g35)
    c: Coincident(g36,g6)
    c: Coincident(g36,g19)
    c: Horizontal(g36)
    c: Coincident(g37,g6)
    c: Coincident(g37,g19)
    c: Horizontal(g37)
    c: Coincident(g38,g7)
    c: Coincident(g38,g18)
    c: Horizontal(g38)
    c: Coincident(g39,g7)
    c: Coincident(g39,g18)
    c: Horizontal(g39)
    c: Coincident(g40,g8)
    c: Coincident(g40,g20)
    c: Horizontal(g40)
    c: Coincident(g41,g8)
    c: Coincident(g41,g20)
    c: Horizontal(g41)
    c: Coincident(g42,g9)
    c: Coincident(g42,g23)
    c: Horizontal(g42)
    c: Coincident(g43,g9)
    c: Coincident(g43,g23)
    c: Horizontal(g43)
    c: Coincident(g44,g10)
    c: Coincident(g44,g22)
    c: Horizontal(g44)
    c: Coincident(g45,g10)
    c: Coincident(g45,g22)
    c: Horizontal(g45)
    c: Coincident(g46,g11)
    c: Coincident(g46,g21)
    c: Horizontal(g46)
    c: Coincident(g47,g11)
    c: Coincident(g47,g21)
    c: Horizontal(g47)
FEATURE [Part::Extrusion] Extrude042
  Base = -> Sketch051
  Dir = (1,-2e-16,2e-16)
  DirMode = 2
  FaceMakerClass = Part::FaceMakerBullseye
  LengthFwd = 19
  LengthRev = 0
  Placement = pos=(-19,0,0) rot=(0,0,1;0rad)
  Solid = true
  Symmetric = false
FEATURE [Part::Fillet] Fillet035  label="removeToCreateVentalationHoles"
  Base = -> Extrude042
  Edges = <same value as first occurrence — deduplicated (x4 in doc)>
  Placement = pos=(7,0,0) rot=(0,0,1;0rad)
FEATURE [Part::Cut] Cut038  label="top017"
  Base = -> Cut033
  Tool = -> Fillet035
FEATURE [Sketcher::SketchObject] Sketch052  label="bottomSketch001"
  FullyConstrained = true
  sketch-geometry (26):
    g0: LineSegment StartX=6.29999 StartY=8 StartZ=0 EndX=3.29999 EndY=8 EndZ=0
    g1: LineSegment StartX=3.29999 StartY=8 StartZ=0 EndX=3.29999 EndY=-6.03275e-07 EndZ=0
    g2: ArcOfCircle CenterX=8.29999 CenterY=5 CenterZ=0 NormalX=0 NormalY=0 NormalZ=1 AngleXU=0 Radius=2 StartAngle=3.14159 EndAngle=4.71239
    g3: LineSegment StartX=6.29999 StartY=8 StartZ=0 EndX=6.29999 EndY=5 EndZ=0
    g4: ArcOfCircle CenterX=105 CenterY=19 CenterZ=0 NormalX=0 NormalY=0 NormalZ=1 AngleXU=0 Radius=12.7 StartAngle=4.71239 EndAngle=6.28319
    g5-g11: Circle x7 (B-spline internal-alignment scaffolding for g12; pole/knot coordinates omitted)
    g12: BSplineCurve PolesCount=7 KnotsCount=5 Degree=3 IsPeriodic=0
    g13-g17: GeomPoint x5 (B-spline internal-alignment scaffolding for g12; pole/knot coordinates omitted)
    g18: ArcOfCircle CenterX=105 CenterY=19 CenterZ=0 NormalX=0 NormalY=0 NormalZ=1 AngleXU=0 Radius=15.7 StartAngle=5.81226 EndAngle=6.28319
    g19: LineSegment StartX=117.7 StartY=19 StartZ=0 EndX=120.7 EndY=19 EndZ=0
    g20: BSplineCurve PolesCount=5 KnotsCount=3 Degree=3 IsPeriodic=0
    g21: LineSegment StartX=8.29999 StartY=3 StartZ=0 EndX=101.7 EndY=3 EndZ=0
    g22: LineSegment StartX=3.29999 StartY=-6.03275e-07 StartZ=0 EndX=105 EndY=-6.03275e-07 EndZ=0
    g23: LineSegment StartX=120.974 StartY=8.71251 StartZ=0 EndX=122.332 EndY=7.83778 EndZ=0
    g24: LineSegment StartX=105 StartY=-6.03274e-07 StartZ=0 EndX=113 EndY=-6.03274e-07 EndZ=0
    g25: ArcOfCircle CenterX=105 CenterY=19 CenterZ=0 NormalX=0 NormalY=0 NormalZ=1 AngleXU=0 Radius=20.6155 StartAngle=5.11091 EndAngle=5.71103
  constraints (38):
    c: Horizontal(g0)
    c: Distance(g0) = 3
    c: Coincident(g1,g0)
    c: Vertical(g1)
    c: Block(g2)
    c: Block(g0)
    c: Coincident(g3,g0)
    c: Coincident(g3,g2)
    c: Vertical(g3)
    c: Block(g1)
    c: Block(g4)
    c: Coincident(g20,g4)
    c: Block(g20)
    c: Equal(g5, g6-g11) x6
    c: InternalAlignment(g5-g11 -> g12) x7
    c: InternalAlignment(g13-g17 -> g12) x5
    c: Block(g12)
    c: Coincident(g18,g12)
    c: Coincident(g19,g4)
    c: Coincident(g19,g18)
    c: Horizontal(g19)
    c: Block(g19)
    c: Block(g18)
    c: Coincident(g21,g2)
    c: Coincident(g21,g20)
    c: Horizontal(g21)
    c: Distance(g21) = 93.4
    c: Coincident(g22,g1)
    c: Horizontal(g22)
    c: Distance(g22) = 101.7
    c: Horizontal(g24)
    c: Distance(g24) = 8
    c: Coincident(g25,g24)
    c: Block(g24)
    c: Coincident(g23,g25)
    c: Block(g25)
    c: Block(g23)
    c: Distance(g23) = 1.61553
FEATURE [Part::Extrusion] Extrude043  label="bottom010"
  Base = -> Sketch052
  Dir = (0,0,1)
  DirMode = 2
  FaceMakerClass = Part::FaceMakerBullseye
  LengthFwd = 71.4
  LengthRev = 0
  Placement = pos=(0,0,0.3) rot=(0,0,1;0rad)
  Solid = true
  Symmetric = false
FEATURE [Sketcher::SketchObject] Sketch053  label="topSketch013"
  FullyConstrained = true
  sketch-geometry (22):
    g0: LineSegment StartX=5.21097e-06 StartY=3 StartZ=0 EndX=5.21097e-06 EndY=19 EndZ=0
    g1: ArcOfCircle CenterX=19 CenterY=19 CenterZ=0 NormalX=0 NormalY=0 NormalZ=1 AngleXU=0 Radius=19 StartAngle=1.5708 EndAngle=3.14159
    g2: ArcOfCircle CenterX=19 CenterY=19 CenterZ=0 NormalX=0 NormalY=0 NormalZ=1 AngleXU=0 Radius=16 StartAngle=1.5708 EndAngle=3.14159
    g3: LineSegment StartX=114 StartY=35 StartZ=0 EndX=19 EndY=35 EndZ=0
    g4: LineSegment StartX=5.21097e-06 StartY=3 StartZ=0 EndX=5.21097e-06 EndY=0 EndZ=0
    g5: LineSegment StartX=3 StartY=0 StartZ=0 EndX=5.21097e-06 EndY=0 EndZ=0
    g6: LineSegment StartX=3 StartY=19 StartZ=0 EndX=3 EndY=0 EndZ=0
    g7: LineSegment StartX=19 StartY=38 StartZ=0 EndX=124 EndY=38 EndZ=0
    g8: Circle CenterX=119 CenterY=35 CenterZ=0 NormalX=0 NormalY=0 NormalZ=1 AngleXU=0 Radius=1
    g9: Circle CenterX=121 CenterY=35 CenterZ=0 NormalX=0 NormalY=0 NormalZ=1 AngleXU=0 Radius=1
    g10: Circle CenterX=121 CenterY=33 CenterZ=0 NormalX=0 NormalY=0 NormalZ=1 AngleXU=0 Radius=1
    g11: BSplineCurve PolesCount=3 KnotsCount=2 Degree=2 IsPeriodic=0
    g12: GeomPoint X=119 Y=35 Z=0
    g13: GeomPoint X=121 Y=33 Z=0
    g14: LineSegment StartX=119 StartY=35 StartZ=0 EndX=114 EndY=35 EndZ=0
    g15: ArcOfCircle CenterX=105 CenterY=19 CenterZ=0 NormalX=0 NormalY=0 NormalZ=1 AngleXU=0 Radius=16 StartAngle=5.60905 EndAngle=6.28319
    g16: LineSegment StartX=121 StartY=33 StartZ=0 EndX=121 EndY=19 EndZ=0
    g17: LineSegment StartX=117.5 StartY=9.01251 StartZ=0 EndX=121.163 EndY=9.0125 EndZ=0
    g18: ArcOfCircle CenterX=105 CenterY=19 CenterZ=0 NormalX=0 NormalY=0 NormalZ=1 AngleXU=0 Radius=20.6155 StartAngle=5.7297 EndAngle=6.28319
    g19: LineSegment StartX=121.163 StartY=9.0125 StartZ=0 EndX=122.538 EndY=8.16329 EndZ=0
    g20: LineSegment StartX=124 StartY=38 StartZ=0 EndX=125.616 EndY=38 EndZ=0
    g21: LineSegment StartX=125.616 StartY=19 StartZ=0 EndX=125.616 EndY=38 EndZ=0
  constraints (50):
    c: Vertical(g0)
    c: Block(g0)
    c: Coincident(g1,g0)
    c: Block(g1)
    c: Coincident(g2,g1)
    c: Block(g2)
    c: Coincident(g3,g2)
    c: Horizontal(g3)
    c: Tangent(g3,g2)
    c: Coincident(g4,g0)
    c: Distance(g4) = 3
    c: Vertical(g4)
    c: Coincident(g5,g4)
    c: Horizontal(g5)
    c: Coincident(g6,g2)
    c: Coincident(g6,g5)
    c: Vertical(g6)
    c: Horizontal(g7)
    c: Distance(g7) = 105
    c: Coincident(g7,g1)
    c: Block(g3)
    c: Weight(g8) = 1
    c: Equal(g8,g9)
    c: Equal(g8,g10)
    c: InternalAlignment(g8,g11)
    c: InternalAlignment(g9,g11)
    c: InternalAlignment(g10,g11)
    c: InternalAlignment(g12,g11)
    c: InternalAlignment(g13,g11)
    c: Block(g11)
    c: Coincident(g14,g11)
    c: Coincident(g14,g3)
    c: Horizontal(g14)
    c: Block(g15)
    c: Coincident(g16,g11)
    c: Coincident(g16,g15)
    c: Vertical(g16)
    c: Distance(g16) = 14
    c: Coincident(g17,g15)
    c: Block(g18)
    c: Coincident(g19,g18)
    c: Coincident(g20,g7)
    c: Horizontal(g20)
    c: Vertical(g21)
    c: Coincident(g20,g21)
    c: Block(g20)
    c: Block(g21)
    c: Block(g19)
    c: Block(g17)
    c: Distance(g20) = 1.61553
FEATURE [Part::Extrusion] Extrude044
  Base = -> Sketch053
  Dir = (0,0,1)
  DirMode = 2
  FaceMakerClass = Part::FaceMakerBullseye
  LengthFwd = 72
  LengthRev = 0
  Solid = true
  Symmetric = false
FEATURE [Part::Fillet] Fillet036  label="top018"
  Base = -> Extrude044
  Edges = 1 edges r=2: [Edge41]
FEATURE [Part::Fillet] Fillet037  label="bottom011"
  Base = -> Extrude043
  Edges = 1 edges r=2.4: [Edge26]
FEATURE [Sketcher::SketchObject] Sketch054
  FullyConstrained = false
  Placement = pos=(0,0,0) rot=(1,0,0;1.5708rad)
  sketch-geometry (24):
    g0: ArcOfCircle CenterX=-4 CenterY=-10.5 CenterZ=0 NormalX=0 NormalY=0 NormalZ=1 AngleXU=0 Radius=1.5 StartAngle=6e-16 EndAngle=3.14159
    g1: ArcOfCircle CenterX=-34.2 CenterY=-10.5 CenterZ=0 NormalX=0 NormalY=0 NormalZ=1 AngleXU=0 Radius=1.5 StartAngle=0 EndAngle=3.14159
    g2: ArcOfCircle CenterX=-34.2 CenterY=-27.7 CenterZ=0 NormalX=0 NormalY=0 NormalZ=1 AngleXU=0 Radius=1.5 StartAngle=3.14159 EndAngle=6.28319
    g3: ArcOfCircle CenterX=-4 CenterY=-27.7 CenterZ=0 NormalX=0 NormalY=0 NormalZ=1 AngleXU=0 Radius=1.5 StartAngle=3.1416 EndAngle=6.28319
    g4: ArcOfCircle CenterX=-10 CenterY=-4.3 CenterZ=0 NormalX=0 NormalY=0 NormalZ=1 AngleXU=0 Radius=1.5 StartAngle=2e-16 EndAngle=3.14159
    g5: ArcOfCircle CenterX=-16.1 CenterY=-1.8 CenterZ=0 NormalX=0 NormalY=0 NormalZ=1 AngleXU=0 Radius=1.5 StartAngle=5e-16 EndAngle=3.14159
    g6: ArcOfCircle CenterX=-22.1 CenterY=-1.8 CenterZ=0 NormalX=0 NormalY=0 NormalZ=1 AngleXU=0 Radius=1.5 StartAngle=5e-16 EndAngle=3.14159
    g7: ArcOfCircle CenterX=-28.2 CenterY=-4.3 CenterZ=0 NormalX=0 NormalY=0 NormalZ=1 AngleXU=0 Radius=1.5 StartAngle=2e-16 EndAngle=3.14159
    g8: ArcOfCircle CenterX=-10 CenterY=-33.9 CenterZ=0 NormalX=0 NormalY=0 NormalZ=1 AngleXU=0 Radius=1.5 StartAngle=3.14159 EndAngle=6.28319
    g9: ArcOfCircle CenterX=-16.1 CenterY=-36.4 CenterZ=0 NormalX=0 NormalY=0 NormalZ=1 AngleXU=0 Radius=1.5 StartAngle=3.14159 EndAngle=6.28319
    g10: ArcOfCircle CenterX=-22.1 CenterY=-36.4 CenterZ=0 NormalX=0 NormalY=0 NormalZ=1 AngleXU=0 Radius=1.5 StartAngle=3.14159 EndAngle=6.28319
    g11: ArcOfCircle CenterX=-28.2 CenterY=-33.9 CenterZ=0 NormalX=0 NormalY=0 NormalZ=1 AngleXU=0 Radius=1.5 StartAngle=3.14159 EndAngle=6.28319
    g12: LineSegment StartX=-35.7 StartY=-10.5 StartZ=0 EndX=-35.7 EndY=-27.7 EndZ=0
    g13: LineSegment StartX=-32.7 StartY=-10.5 StartZ=0 EndX=-32.7 EndY=-27.7 EndZ=0
    g14: LineSegment StartX=-29.7 StartY=-33.9 StartZ=0 EndX=-29.7 EndY=-4.3 EndZ=0
    g15: LineSegment StartX=-26.7 StartY=-33.9 StartZ=0 EndX=-26.7 EndY=-4.3 EndZ=0
    g16: LineSegment StartX=-2.5 StartY=-10.5 StartZ=0 EndX=-2.5 EndY=-27.7 EndZ=0
    g17: LineSegment StartX=-8.5 StartY=-4.3 StartZ=0 EndX=-8.5 EndY=-33.9 EndZ=0
    g18: LineSegment StartX=-5.5 StartY=-10.5 StartZ=0 EndX=-5.5 EndY=-27.7 EndZ=0
    g19: LineSegment StartX=-11.5 StartY=-4.3 StartZ=0 EndX=-11.5 EndY=-33.9 EndZ=0
    g20: LineSegment StartX=-14.6 StartY=-1.8 StartZ=0 EndX=-14.6 EndY=-36.4 EndZ=0
    g21: LineSegment StartX=-17.6 StartY=-1.8 StartZ=0 EndX=-17.6 EndY=-36.4 EndZ=0
    g22: LineSegment StartX=-20.6 StartY=-36.4 StartZ=0 EndX=-20.6 EndY=-1.8 EndZ=0
    g23: LineSegment StartX=-23.6 StartY=-1.8 StartZ=0 EndX=-23.6 EndY=-36.4 EndZ=0
  constraints (48):
    c: Block(g0)
    c: Block(g1)
    c: Block(g2)
    c: Block(g3)
    c: Block(g4)
    c: Block(g5)
    c: Block(g6)
    c: Block(g7)
    c: Block(g8)
    c: Block(g9)
    c: Block(g10)
    c: Block(g11)
    c: Coincident(g12,g1)
    c: Coincident(g12,g2)
    c: Vertical(g12)
    c: Coincident(g13,g1)
    c: Coincident(g13,g2)
    c: Vertical(g13)
    c: Coincident(g14,g11)
    c: Coincident(g14,g7)
    c: Vertical(g14)
    c: Coincident(g15,g11)
    c: Coincident(g15,g7)
    c: Vertical(g15)
    c: Coincident(g16,g0)
    c: Coincident(g16,g3)
    c: Vertical(g16)
    c: Coincident(g17,g4)
    c: Coincident(g17,g8)
    c: Vertical(g17)
    c: Coincident(g18,g0)
    c: Coincident(g18,g3)
    c: Vertical(g18)
    c: Coincident(g19,g4)
    c: Coincident(g19,g8)
    c: Vertical(g19)
    c: Coincident(g20,g5)
    c: Coincident(g20,g9)
    c: Vertical(g20)
    c: Coincident(g21,g5)
    c: Coincident(g21,g9)
    c: Vertical(g21)
    c: Coincident(g22,g10)
    c: Coincident(g22,g6)
    c: Vertical(g22)
    c: Coincident(g23,g6)
    c: Coincident(g23,g10)
    c: Vertical(g23)
FEATURE [Part::Extrusion] Extrude045  label="removeToCreateFanGrillHoles003"
  Base = -> Sketch054
  Dir = (0,-1,6e-16)
  DirMode = 2
  FaceMakerClass = Part::FaceMakerBullseye
  LengthFwd = 10
  LengthRev = 0
  Placement = pos=(65.4,44,54.82) rot=(0,0,1;0rad)
  Solid = true
  Symmetric = false
FEATURE [Part::Feature] Face105 .. Face108  x4 (patterned run collapsed; names and placements below)
  shape: bbox 3.5 x 17.8 x 2e-07 mm, 1 faces, 0 solids (baked)
FEATURE [Part::Revolution] Revolve113  label="removeToCreateScrewAndThreadedInsertHole041"
  Angle = 360
  Axis = (0,1,0)
  Base = (0,0,0)
  FaceMakerClass = Part::FaceMakerBullseye
  Placement = pos=(62.3,30.3,19.7) rot=(0,0,1;0rad)
  Solid = false
  Source = -> Face105
  Symmetric = false
FEATURE [Part::Revolution] Revolve114  label="removeToCreateScrewAndThreadedInsertHole042"
  Angle = 360
  Axis = (0,1,0)
  Base = (0,0,0)
  FaceMakerClass = Part::FaceMakerBullseye
  Placement = pos=(62.3,30.3,51.7) rot=(0,0,1;0rad)
  Solid = false
  Source = -> Face106
  Symmetric = false
FEATURE [Part::Revolution] Revolve115  label="removeToCreateScrewAndThreadedInsertHole043"
  Angle = 360
  Axis = (0,1,0)
  Base = (0,0,0)
  FaceMakerClass = Part::FaceMakerBullseye
  Placement = pos=(30.3,30.3,19.7) rot=(0,0,1;0rad)
  Solid = false
  Source = -> Face107
  Symmetric = false
FEATURE [Part::Revolution] Revolve116  label="removeToCreateScrewAndThreadedInsertHole044"
  Angle = 360
  Axis = (0,1,0)
  Base = (0,0,0)
  FaceMakerClass = Part::FaceMakerBullseye
  Placement = pos=(30.3,30.3,51.7) rot=(0,0,1;0rad)
  Solid = false
  Source = -> Face108
  Symmetric = false
FEATURE [Part::MultiFuse] Fusion083  label="createThreadedInsertHolesForFan004"
  Shapes = -> [Revolve113,Revolve114,Revolve115,Revolve116]
FEATURE [Part::Box] Box024  label="removeToCreteHoleForPlugHousing026"
  AttacherType = Attacher::AttachEngine3D
  Height = 28.6
  Length = 10
  Placement = pos=(-2,0,21.7) rot=(0,0,1;0rad)
  Width = 19
FEATURE [Part::Cylinder] Cylinder038  label="removeToCreteHoleForPlugHousing027"
  Angle = 360
  AttacherType = Attacher::AttachEngine3D
  Height = 20
  Placement = pos=(-2,19,36) rot=(0,1,0;1.5708rad)
  Radius = 14.3
FEATURE [Part::MultiFuse] Fusion084  label="removeToCreteHoleForPlugHousing028"
  Shapes = -> [Box024,Cylinder038]
FEATURE [Part::Cylinder] Cylinder039
  Angle = 360
  AttacherType = Attacher::AttachEngine3D
  Height = 20
  Placement = pos=(0,0,36.15) rot=(0,0,1;0rad)
  Radius = 14.3
FEATURE [Part::Cylinder] Cylinder040
  Angle = 360
  AttacherType = Attacher::AttachEngine3D
  Height = 10
  Placement = pos=(0,0,36.15) rot=(0,0,1;0rad)
  Radius = 4
FEATURE [Part::Box] Box025  label="removeToCreteHoleForPlugHousing030"
  AttacherType = Attacher::AttachEngine3D
  Height = 28.6
  Length = 20
  Placement = pos=(106.15,0,21.7) rot=(0,0,1;0rad)
  Width = 19
FEATURE [Part::MultiFuse] Fusion086  label="removeToCreteHoleForPlugHousing031"
  Placement = pos=(70,19,36) rot=(0,1,0;1.5708rad)
  Shapes = -> [Cylinder039,Cylinder040]
FEATURE [Part::MultiFuse] Fusion085  label="removeToCreteHoleForPlugHousing029"
  Shapes = -> [Box025,Fusion086]
FEATURE [Sketcher::SketchObject] Sketch055
  FullyConstrained = true
  Placement = pos=(117,19,0) rot=(0.57735,0.57735,0.57735;2.0944rad)
  sketch-geometry (48):
    g0: LineSegment StartX=-49.19 StartY=69.25 StartZ=0 EndX=-49.19 EndY=66.25 EndZ=0
    g1: LineSegment StartX=-49.19 StartY=63.5 StartZ=0 EndX=-49.19 EndY=60.5 EndZ=0
    g2: LineSegment StartX=-49.19 StartY=57.75 StartZ=0 EndX=-49.19 EndY=54.75 EndZ=0
    g3: LineSegment StartX=-49.19 StartY=52 StartZ=0 EndX=-49.19 EndY=49 EndZ=0
    g4: LineSegment StartX=-49.19 StartY=46.25 StartZ=0 EndX=-49.19 EndY=43.25 EndZ=0
    g5: LineSegment StartX=-49.19 StartY=40.5 StartZ=0 EndX=-49.19 EndY=37.5 EndZ=0
    g6: LineSegment StartX=-49.19 StartY=34.5 StartZ=0 EndX=-49.19 EndY=31.5 EndZ=0
    g7: LineSegment StartX=-49.19 StartY=28.75 StartZ=0 EndX=-49.19 EndY=25.75 EndZ=0
    g8: LineSegment StartX=-49.19 StartY=23 StartZ=0 EndX=-49.19 EndY=20 EndZ=0
    g9: LineSegment StartX=-49.19 StartY=17.25 StartZ=0 EndX=-49.19 EndY=14.25 EndZ=0
    g10: LineSegment StartX=-49.19 StartY=11.5 StartZ=0 EndX=-49.19 EndY=8.5 EndZ=0
    g11: LineSegment StartX=-49.19 StartY=5.75 StartZ=0 EndX=-49.19 EndY=2.75 EndZ=0
    g12: ArcOfCircle CenterX=-1.5 CenterY=67.75 CenterZ=0 NormalX=0 NormalY=0 NormalZ=1 AngleXU=0 Radius=1.5 StartAngle=4.71239 EndAngle=7.85398
    g13: ArcOfCircle CenterX=-1.5 CenterY=62 CenterZ=0 NormalX=0 NormalY=0 NormalZ=1 AngleXU=0 Radius=1.5 StartAngle=4.71239 EndAngle=7.85398
    g14: ArcOfCircle CenterX=-1.5 CenterY=56.25 CenterZ=0 NormalX=0 NormalY=0 NormalZ=1 AngleXU=0 Radius=1.5 StartAngle=4.71239 EndAngle=7.85398
    g15: ArcOfCircle CenterX=-11.49 CenterY=50.5 CenterZ=0 NormalX=0 NormalY=0 NormalZ=1 AngleXU=0 Radius=1.5 StartAngle=4.71239 EndAngle=7.85398
    g16: ArcOfCircle CenterX=-16.28 CenterY=44.75 CenterZ=0 NormalX=0 NormalY=0 NormalZ=1 AngleXU=0 Radius=1.5 StartAngle=4.71239 EndAngle=7.85398
    g17: ArcOfCircle CenterX=-18.2337 CenterY=39 CenterZ=0 NormalX=0 NormalY=0 NormalZ=1 AngleXU=0 Radius=1.5 StartAngle=4.71485 EndAngle=7.85398
    g18: ArcOfCircle CenterX=-16.2837 CenterY=27.25 CenterZ=0 NormalX=0 NormalY=0 NormalZ=1 AngleXU=0 Radius=1.5 StartAngle=4.71485 EndAngle=7.85398
    g19: ArcOfCircle CenterX=-18.2337 CenterY=33 CenterZ=0 NormalX=0 NormalY=0 NormalZ=1 AngleXU=0 Radius=1.5 StartAngle=4.71485 EndAngle=7.85398
    g20: ArcOfCircle CenterX=-11.49 CenterY=21.5 CenterZ=0 NormalX=0 NormalY=0 NormalZ=1 AngleXU=0 Radius=1.5 StartAngle=4.71239 EndAngle=7.85398
    g21: ArcOfCircle CenterX=-1.5 CenterY=4.25 CenterZ=0 NormalX=0 NormalY=0 NormalZ=1 AngleXU=0 Radius=1.5 StartAngle=4.71239 EndAngle=7.85398
    g22: ArcOfCircle CenterX=-1.5 CenterY=10 CenterZ=0 NormalX=0 NormalY=0 NormalZ=1 AngleXU=0 Radius=1.5 StartAngle=4.71239 EndAngle=7.85398
    g23: ArcOfCircle CenterX=-1.5 CenterY=15.75 CenterZ=0 NormalX=0 NormalY=0 NormalZ=1 AngleXU=0 Radius=1.5 StartAngle=4.71239 EndAngle=7.85398
    g24: LineSegment StartX=-49.19 StartY=69.25 StartZ=0 EndX=-1.5 EndY=69.25 EndZ=0
    g25: LineSegment StartX=-49.19 StartY=66.25 StartZ=0 EndX=-1.5 EndY=66.25 EndZ=0
    g26: LineSegment StartX=-49.19 StartY=63.5 StartZ=0 EndX=-1.5 EndY=63.5 EndZ=0
    g27: LineSegment StartX=-49.19 StartY=60.5 StartZ=0 EndX=-1.5 EndY=60.5 EndZ=0
    g28: LineSegment StartX=-49.19 StartY=57.75 StartZ=0 EndX=-1.5 EndY=57.75 EndZ=0
    g29: LineSegment StartX=-49.19 StartY=54.75 StartZ=0 EndX=-1.5 EndY=54.75 EndZ=0
    g30: LineSegment StartX=-49.19 StartY=52 StartZ=0 EndX=-11.49 EndY=52 EndZ=0
    g31: LineSegment StartX=-49.19 StartY=49 StartZ=0 EndX=-11.49 EndY=49 EndZ=0
    g32: LineSegment StartX=-49.19 StartY=46.25 StartZ=0 EndX=-16.28 EndY=46.25 EndZ=0
    g33: LineSegment StartX=-49.19 StartY=43.25 StartZ=0 EndX=-16.28 EndY=43.25 EndZ=0
    g34: LineSegment StartX=-49.19 StartY=40.5 StartZ=0 EndX=-18.2337 EndY=40.5 EndZ=0
    g35: LineSegment StartX=-49.19 StartY=37.5 StartZ=0 EndX=-18.23 EndY=37.5 EndZ=0
    g36: LineSegment StartX=-49.19 StartY=34.5 StartZ=0 EndX=-18.2337 EndY=34.5 EndZ=0
    g37: LineSegment StartX=-49.19 StartY=31.5 StartZ=0 EndX=-18.23 EndY=31.5 EndZ=0
    g38: LineSegment StartX=-49.19 StartY=28.75 StartZ=0 EndX=-16.2837 EndY=28.75 EndZ=0
    g39: LineSegment StartX=-49.19 StartY=25.75 StartZ=0 EndX=-16.28 EndY=25.75 EndZ=0
    g40: LineSegment StartX=-49.19 StartY=23 StartZ=0 EndX=-11.49 EndY=23 EndZ=0
    g41: LineSegment StartX=-49.19 StartY=20 StartZ=0 EndX=-11.49 EndY=20 EndZ=0
    g42: LineSegment StartX=-49.19 StartY=17.25 StartZ=0 EndX=-1.5 EndY=17.25 EndZ=0
    g43: LineSegment StartX=-49.19 StartY=14.25 StartZ=0 EndX=-1.5 EndY=14.25 EndZ=0
    g44: LineSegment StartX=-49.19 StartY=11.5 StartZ=0 EndX=-1.5 EndY=11.5 EndZ=0
    g45: LineSegment StartX=-49.19 StartY=8.5 StartZ=0 EndX=-1.5 EndY=8.5 EndZ=0
    g46: LineSegment StartX=-49.19 StartY=5.75 StartZ=0 EndX=-1.5 EndY=5.75 EndZ=0
    g47: LineSegment StartX=-49.19 StartY=2.75 StartZ=0 EndX=-1.5 EndY=2.75 EndZ=0
  constraints (120):
    c: Vertical(g0)
    c: Distance(g0) = 3
    c: Block(g0)
    c: Vertical(g1)
    c: Distance(g1) = 3
    c: Vertical(g2)
    c: Equal(g0,g2) = 3
    c: Block(g2)
    c: Vertical(g3)
    c: Equal(g1,g3) = 3
    c: Vertical(g4)
    c: Equal(g0,g4) = 3
    c: Block(g4)
    c: Vertical(g5)
    c: Equal(g1,g5) = 3
    c: Vertical(g6)
    c: Equal(g0,g6) = 3
    c: Block(g6)
    c: Vertical(g7)
    c: Equal(g1,g7) = 3
    c: Vertical(g8)
    c: Equal(g0,g8) = 3
    c: Block(g8)
    c: Vertical(g9)
    c: Equal(g1,g9) = 3
    c: Vertical(g10)
    c: Equal(g0,g10) = 3
    c: Block(g10)
    c: Vertical(g11)
    c: Equal(g1,g11) = 3
    c: Block(g12)
    c: Block(g13)
    c: Block(g14)
    c: Block(g15)
    c: Block(g16)
    c: Block(g17)
    c: Block(g18)
    c: Block(g19)
    c: Block(g20)
    c: Block(g21)
    c: Block(g22)
    c: Block(g23)
    c: Block(g11)
    c: Block(g9)
    c: Block(g7)
    c: Block(g5)
    c: Block(g3)
    c: Block(g1)
    c: Coincident(g24,g0)
    c: Coincident(g24,g12)
    c: Horizontal(g24)
    c: Coincident(g25,g0)
    c: Coincident(g25,g12)
    c: Horizontal(g25)
    c: Coincident(g26,g1)
    c: Coincident(g26,g13)
    c: Horizontal(g26)
    c: Coincident(g27,g1)
    c: Coincident(g27,g13)
    c: Horizontal(g27)
    c: Coincident(g28,g2)
    c: Coincident(g28,g14)
    c: Horizontal(g28)
    c: Coincident(g29,g2)
    c: Coincident(g29,g14)
    c: Horizontal(g29)
    c: Coincident(g30,g3)
    c: Coincident(g30,g15)
    c: Horizontal(g30)
    c: Coincident(g31,g3)
    c: Coincident(g31,g15)
    c: Horizontal(g31)
    c: Coincident(g32,g4)
    c: Coincident(g32,g16)
    c: Horizontal(g32)
    c: Coincident(g33,g4)
    c: Coincident(g33,g16)
    c: Horizontal(g33)
    c: Coincident(g34,g5)
    c: Coincident(g34,g17)
    c: Horizontal(g34)
    c: Coincident(g35,g5)
    c: Coincident(g35,g17)
    c: Horizontal(g35)
    c: Coincident(g36,g6)
    c: Coincident(g36,g19)
    c: Horizontal(g36)
    c: Coincident(g37,g6)
    c: Coincident(g37,g19)
    c: Horizontal(g37)
    c: Coincident(g38,g7)
    c: Coincident(g38,g18)
    c: Horizontal(g38)
    c: Coincident(g39,g7)
    c: Coincident(g39,g18)
    c: Horizontal(g39)
    c: Coincident(g40,g8)
    c: Coincident(g40,g20)
    c: Horizontal(g40)
    c: Coincident(g41,g8)
    c: Coincident(g41,g20)
    c: Horizontal(g41)
    c: Coincident(g42,g9)
    c: Coincident(g42,g23)
    c: Horizontal(g42)
    c: Coincident(g43,g9)
    c: Coincident(g43,g23)
    c: Horizontal(g43)
    c: Coincident(g44,g10)
    c: Coincident(g44,g22)
    c: Horizontal(g44)
    c: Coincident(g45,g10)
    c: Coincident(g45,g22)
    c: Horizontal(g45)
    c: Coincident(g46,g11)
    c: Coincident(g46,g21)
    c: Horizontal(g46)
    c: Coincident(g47,g11)
    c: Coincident(g47,g21)
    c: Horizontal(g47)
FEATURE [Part::Extrusion] Extrude046
  Base = -> Sketch055
  Dir = (1,0,0)
  DirMode = 2
  FaceMakerClass = Part::FaceMakerBullseye
  LengthFwd = 23
  LengthRev = 0
  Placement = pos=(-19,0,0) rot=(0,0,1;0rad)
  Solid = true
  Symmetric = false
FEATURE [Part::Fillet] Fillet038  label="removeToCreateVentalationHoles001"
  Base = -> Extrude046
  Edges = <same value as first occurrence — deduplicated (x4 in doc)>
  Placement = pos=(7,0,0) rot=(0,0,1;0rad)
FEATURE [Sketcher::SketchObject] Sketch056  label="topSketch014"
  FullyConstrained = true
  sketch-geometry (22):
    g0: LineSegment StartX=5.21097e-06 StartY=3 StartZ=0 EndX=5.21097e-06 EndY=19 EndZ=0
    g1: ArcOfCircle CenterX=19 CenterY=19 CenterZ=0 NormalX=0 NormalY=0 NormalZ=1 AngleXU=0 Radius=19 StartAngle=1.5708 EndAngle=3.14159
    g2: ArcOfCircle CenterX=19 CenterY=19 CenterZ=0 NormalX=0 NormalY=0 NormalZ=1 AngleXU=0 Radius=16 StartAngle=1.5708 EndAngle=3.14159
    g3: LineSegment StartX=114 StartY=35 StartZ=0 EndX=19 EndY=35 EndZ=0
    g4: LineSegment StartX=5.21097e-06 StartY=3 StartZ=0 EndX=5.21097e-06 EndY=0 EndZ=0
    g5: LineSegment StartX=3 StartY=0 StartZ=0 EndX=5.21097e-06 EndY=0 EndZ=0
    g6: LineSegment StartX=3 StartY=19 StartZ=0 EndX=3 EndY=0 EndZ=0
    g7: LineSegment StartX=19 StartY=38 StartZ=0 EndX=124 EndY=38 EndZ=0
    g8: Circle CenterX=119 CenterY=35 CenterZ=0 NormalX=0 NormalY=0 NormalZ=1 AngleXU=0 Radius=1
    g9: Circle CenterX=121 CenterY=35 CenterZ=0 NormalX=0 NormalY=0 NormalZ=1 AngleXU=0 Radius=1
    g10: Circle CenterX=121 CenterY=33 CenterZ=0 NormalX=0 NormalY=0 NormalZ=1 AngleXU=0 Radius=1
    g11: BSplineCurve PolesCount=3 KnotsCount=2 Degree=2 IsPeriodic=0
    g12: GeomPoint X=119 Y=35 Z=0
    g13: GeomPoint X=121 Y=33 Z=0
    g14: LineSegment StartX=119 StartY=35 StartZ=0 EndX=114 EndY=35 EndZ=0
    g15: ArcOfCircle CenterX=105 CenterY=19 CenterZ=0 NormalX=0 NormalY=0 NormalZ=1 AngleXU=0 Radius=16 StartAngle=5.60905 EndAngle=6.28319
    g16: LineSegment StartX=121 StartY=33 StartZ=0 EndX=121 EndY=19 EndZ=0
    g17: LineSegment StartX=117.5 StartY=9.01251 StartZ=0 EndX=121.163 EndY=9.0125 EndZ=0
    g18: ArcOfCircle CenterX=105 CenterY=19 CenterZ=0 NormalX=0 NormalY=0 NormalZ=1 AngleXU=0 Radius=20.6155 StartAngle=5.7297 EndAngle=6.28319
    g19: LineSegment StartX=121.163 StartY=9.0125 StartZ=0 EndX=122.538 EndY=8.16329 EndZ=0
    g20: LineSegment StartX=124 StartY=38 StartZ=0 EndX=125.616 EndY=38 EndZ=0
    g21: LineSegment StartX=125.616 StartY=19 StartZ=0 EndX=125.616 EndY=38 EndZ=0
  constraints (49):
    c: Vertical(g0)
    c: Block(g0)
    c: Coincident(g1,g0)
    c: Block(g1)
    c: Coincident(g2,g1)
    c: Block(g2)
    c: Coincident(g3,g2)
    c: Horizontal(g3)
    c: Tangent(g3,g2)
    c: Coincident(g4,g0)
    c: Distance(g4) = 3
    c: Vertical(g4)
    c: Coincident(g5,g4)
    c: Horizontal(g5)
    c: Coincident(g6,g2)
    c: Coincident(g6,g5)
    c: Vertical(g6)
    c: Horizontal(g7)
    c: Distance(g7) = 105
    c: Coincident(g7,g1)
    c: Block(g3)
    c: Weight(g8) = 1
    c: Equal(g8,g9)
    c: Equal(g8,g10)
    c: InternalAlignment(g8,g11)
    c: InternalAlignment(g9,g11)
    c: InternalAlignment(g10,g11)
    c: InternalAlignment(g12,g11)
    c: InternalAlignment(g13,g11)
    c: Block(g11)
    c: Coincident(g14,g11)
    c: Coincident(g14,g3)
    c: Horizontal(g14)
    c: Block(g15)
    c: Coincident(g16,g11)
    c: Coincident(g16,g15)
    c: Vertical(g16)
    c: Distance(g16) = 14
    c: Coincident(g17,g15)
    c: Block(g18)
    c: Coincident(g19,g18)
    c: Coincident(g20,g7)
    c: Horizontal(g20)
    c: Vertical(g21)
    c: Coincident(g20,g21)
    c: Block(g20)
    c: Block(g21)
    c: Block(g19)
    c: Block(g17)
FEATURE [Part::Box] Box026  label="removeToCreteHoleForPlugHousing032"
  AttacherType = Attacher::AttachEngine3D
  Height = 28.6
  Length = 10
  Placement = pos=(-2,0,21.7) rot=(0,0,1;0rad)
  Width = 19
FEATURE [Part::Feature] Face109 .. Face112  x4 (patterned run collapsed; names and placements below)
  shape: bbox 3.5 x 17.8 x 2e-07 mm, 1 faces, 0 solids (baked)
FEATURE [Part::Revolution] Revolve117  label="removeToCreateScrewAndThreadedInsertHole045"
  Angle = 360
  Axis = (0,1,0)
  Base = (0,0,0)
  FaceMakerClass = Part::FaceMakerBullseye
  Placement = pos=(62.3,30.3,19.7) rot=(0,0,1;0rad)
  Solid = false
  Source = -> Face109
  Symmetric = false
FEATURE [Part::Revolution] Revolve118  label="removeToCreateScrewAndThreadedInsertHole046"
  Angle = 360
  Axis = (0,1,0)
  Base = (0,0,0)
  FaceMakerClass = Part::FaceMakerBullseye
  Placement = pos=(62.3,30.3,51.7) rot=(0,0,1;0rad)
  Solid = false
  Source = -> Face110
  Symmetric = false
FEATURE [Part::Revolution] Revolve119  label="removeToCreateScrewAndThreadedInsertHole047"
  Angle = 360
  Axis = (0,1,0)
  Base = (0,0,0)
  FaceMakerClass = Part::FaceMakerBullseye
  Placement = pos=(30.3,30.3,19.7) rot=(0,0,1;0rad)
  Solid = false
  Source = -> Face111
  Symmetric = false
FEATURE [Part::Revolution] Revolve120  label="removeToCreateScrewAndThreadedInsertHole048"
  Angle = 360
  Axis = (0,1,0)
  Base = (0,0,0)
  FaceMakerClass = Part::FaceMakerBullseye
  Placement = pos=(30.3,30.3,51.7) rot=(0,0,1;0rad)
  Solid = false
  Source = -> Face112
  Symmetric = false
FEATURE [Part::MultiFuse] Fusion087  label="createThreadedInsertHolesForFan005"
  Shapes = -> [Revolve117,Revolve118,Revolve119,Revolve120]
FEATURE [Part::Extrusion] Extrude047
  Base = -> Sketch056
  Dir = (0,0,1)
  DirMode = 2
  FaceMakerClass = Part::FaceMakerBullseye
  LengthFwd = 72
  LengthRev = 0
  Solid = true
  Symmetric = false
FEATURE [Part::Fillet] Fillet039  label="top019"
  Base = -> Extrude047
  Edges = 1 edges r=2: [Edge35]
FEATURE [Sketcher::SketchObject] Sketch057
  FullyConstrained = false
  Placement = pos=(0,0,0) rot=(1,0,0;1.5708rad)
  sketch-geometry (24):
    g0: ArcOfCircle CenterX=-4 CenterY=-10.5 CenterZ=0 NormalX=0 NormalY=0 NormalZ=1 AngleXU=0 Radius=1.5 StartAngle=6e-16 EndAngle=3.14159
    g1: ArcOfCircle CenterX=-34.2 CenterY=-10.5 CenterZ=0 NormalX=0 NormalY=0 NormalZ=1 AngleXU=0 Radius=1.5 StartAngle=0 EndAngle=3.14159
    g2: ArcOfCircle CenterX=-34.2 CenterY=-27.7 CenterZ=0 NormalX=0 NormalY=0 NormalZ=1 AngleXU=0 Radius=1.5 StartAngle=3.14159 EndAngle=6.28319
    g3: ArcOfCircle CenterX=-4 CenterY=-27.7 CenterZ=0 NormalX=0 NormalY=0 NormalZ=1 AngleXU=0 Radius=1.5 StartAngle=3.1416 EndAngle=6.28319
    g4: ArcOfCircle CenterX=-10 CenterY=-4.3 CenterZ=0 NormalX=0 NormalY=0 NormalZ=1 AngleXU=0 Radius=1.5 StartAngle=2e-16 EndAngle=3.14159
    g5: ArcOfCircle CenterX=-16.1 CenterY=-1.8 CenterZ=0 NormalX=0 NormalY=0 NormalZ=1 AngleXU=0 Radius=1.5 StartAngle=5e-16 EndAngle=3.14159
    g6: ArcOfCircle CenterX=-22.1 CenterY=-1.8 CenterZ=0 NormalX=0 NormalY=0 NormalZ=1 AngleXU=0 Radius=1.5 StartAngle=5e-16 EndAngle=3.14159
    g7: ArcOfCircle CenterX=-28.2 CenterY=-4.3 CenterZ=0 NormalX=0 NormalY=0 NormalZ=1 AngleXU=0 Radius=1.5 StartAngle=2e-16 EndAngle=3.14159
    g8: ArcOfCircle CenterX=-10 CenterY=-33.9 CenterZ=0 NormalX=0 NormalY=0 NormalZ=1 AngleXU=0 Radius=1.5 StartAngle=3.14159 EndAngle=6.28319
    g9: ArcOfCircle CenterX=-16.1 CenterY=-36.4 CenterZ=0 NormalX=0 NormalY=0 NormalZ=1 AngleXU=0 Radius=1.5 StartAngle=3.14159 EndAngle=6.28319
    g10: ArcOfCircle CenterX=-22.1 CenterY=-36.4 CenterZ=0 NormalX=0 NormalY=0 NormalZ=1 AngleXU=0 Radius=1.5 StartAngle=3.14159 EndAngle=6.28319
    g11: ArcOfCircle CenterX=-28.2 CenterY=-33.9 CenterZ=0 NormalX=0 NormalY=0 NormalZ=1 AngleXU=0 Radius=1.5 StartAngle=3.14159 EndAngle=6.28319
    g12: LineSegment StartX=-35.7 StartY=-10.5 StartZ=0 EndX=-35.7 EndY=-27.7 EndZ=0
    g13: LineSegment StartX=-32.7 StartY=-10.5 StartZ=0 EndX=-32.7 EndY=-27.7 EndZ=0
    g14: LineSegment StartX=-29.7 StartY=-33.9 StartZ=0 EndX=-29.7 EndY=-4.3 EndZ=0
    g15: LineSegment StartX=-26.7 StartY=-33.9 StartZ=0 EndX=-26.7 EndY=-4.3 EndZ=0
    g16: LineSegment StartX=-2.5 StartY=-10.5 StartZ=0 EndX=-2.5 EndY=-27.7 EndZ=0
    g17: LineSegment StartX=-8.5 StartY=-4.3 StartZ=0 EndX=-8.5 EndY=-33.9 EndZ=0
    g18: LineSegment StartX=-5.5 StartY=-10.5 StartZ=0 EndX=-5.5 EndY=-27.7 EndZ=0
    g19: LineSegment StartX=-11.5 StartY=-4.3 StartZ=0 EndX=-11.5 EndY=-33.9 EndZ=0
    g20: LineSegment StartX=-14.6 StartY=-1.8 StartZ=0 EndX=-14.6 EndY=-36.4 EndZ=0
    g21: LineSegment StartX=-17.6 StartY=-1.8 StartZ=0 EndX=-17.6 EndY=-36.4 EndZ=0
    g22: LineSegment StartX=-20.6 StartY=-36.4 StartZ=0 EndX=-20.6 EndY=-1.8 EndZ=0
    g23: LineSegment StartX=-23.6 StartY=-1.8 StartZ=0 EndX=-23.6 EndY=-36.4 EndZ=0
  constraints (48):
    c: Block(g0)
    c: Block(g1)
    c: Block(g2)
    c: Block(g3)
    c: Block(g4)
    c: Block(g5)
    c: Block(g6)
    c: Block(g7)
    c: Block(g8)
    c: Block(g9)
    c: Block(g10)
    c: Block(g11)
    c: Coincident(g12,g1)
    c: Coincident(g12,g2)
    c: Vertical(g12)
    c: Coincident(g13,g1)
    c: Coincident(g13,g2)
    c: Vertical(g13)
    c: Coincident(g14,g11)
    c: Coincident(g14,g7)
    c: Vertical(g14)
    c: Coincident(g15,g11)
    c: Coincident(g15,g7)
    c: Vertical(g15)
    c: Coincident(g16,g0)
    c: Coincident(g16,g3)
    c: Vertical(g16)
    c: Coincident(g17,g4)
    c: Coincident(g17,g8)
    c: Vertical(g17)
    c: Coincident(g18,g0)
    c: Coincident(g18,g3)
    c: Vertical(g18)
    c: Coincident(g19,g4)
    c: Coincident(g19,g8)
    c: Vertical(g19)
    c: Coincident(g20,g5)
    c: Coincident(g20,g9)
    c: Vertical(g20)
    c: Coincident(g21,g5)
    c: Coincident(g21,g9)
    c: Vertical(g21)
    c: Coincident(g22,g10)
    c: Coincident(g22,g6)
    c: Vertical(g22)
    c: Coincident(g23,g6)
    c: Coincident(g23,g10)
    c: Vertical(g23)
FEATURE [Part::Extrusion] Extrude048  label="removeToCreateFanGrillHoles004"
  Base = -> Sketch057
  Dir = (0,-1,6e-16)
  DirMode = 2
  FaceMakerClass = Part::FaceMakerBullseye
  LengthFwd = 10
  LengthRev = 0
  Placement = pos=(65.4,44,54.82) rot=(0,0,1;0rad)
  Solid = true
  Symmetric = false
FEATURE [Part::Cut] Cut040  label="top021"
  Base = -> Fillet039
  Tool = -> Extrude048
FEATURE [Part::Cylinder] Cylinder041  label="removeToCreteHoleForPlugHousing034"
  Angle = 360
  AttacherType = Attacher::AttachEngine3D
  Height = 20
  Placement = pos=(-2,19,36) rot=(0,1,0;1.5708rad)
  Radius = 14.3
FEATURE [Part::MultiFuse] Fusion089  label="removeToCreteHoleForPlugHousing035"
  Shapes = -> [Box026,Cylinder041]
FEATURE [Part::Cylinder] Cylinder042
  Angle = 360
  AttacherType = Attacher::AttachEngine3D
  Height = 20
  Placement = pos=(0,0,36.15) rot=(0,0,1;0rad)
  Radius = 14.3
FEATURE [Part::Cylinder] Cylinder043
  Angle = 360
  AttacherType = Attacher::AttachEngine3D
  Height = 10
  Placement = pos=(0,0,36.15) rot=(0,0,1;0rad)
  Radius = 4
FEATURE [Part::Box] Box027  label="removeToCreteHoleForPlugHousing036"
  AttacherType = Attacher::AttachEngine3D
  Height = 28.6
  Length = 20
  Placement = pos=(106.15,0,21.7) rot=(0,0,1;0rad)
  Width = 19
FEATURE [Part::Cut] Cut041  label="top022"
  Base = -> Cut040
  Tool = -> Fusion087
FEATURE [Part::Cut] Cut039  label="top020"
  Base = -> Cut041
  Tool = -> Fusion089
FEATURE [Part::MultiFuse] Fusion090  label="removeToCreteHoleForPlugHousing037"
  Placement = pos=(70,19,36) rot=(0,1,0;1.5708rad)
  Shapes = -> [Cylinder042,Cylinder043]
FEATURE [Part::MultiFuse] Fusion088  label="removeToCreteHoleForPlugHousing033"
  Shapes = -> [Box027,Fusion090]
FEATURE [Part::Cut] Cut042  label="removeToCreteHoleForPlugHousing038"
  Base = -> Cut039
  Tool = -> Fusion088
FEATURE [Part::MultiFuse] Fusion091  label="removeFromTop"
  Shapes = -> [Fillet038,Fusion085,Fusion084,Fusion083,Extrude045]
FEATURE [Part::Cut] Cut043  label="removeToCreteHoleForPlugHousing039"
  Base = -> Fillet036
  Tool = -> Fusion091
FEATURE [Part::MultiFuse] Fusion092  label="caseScrewPillarBracket016"
  Shapes = -> [Extrude030,Extrude031,Extrude032,Extrude033,Extrude034,Extrude035,Extrude036,Extrude037,Box013,Box014]
FEATURE [Part::MultiFuse] Fusion093  label="bottom012"
  Shapes = -> [Cut034,Fillet037]
FEATURE [Sketcher::SketchObject] Sketch058  label="topSketch015"
  FullyConstrained = true
  sketch-geometry (20):
    g0: LineSegment StartX=5.21097e-06 StartY=3 StartZ=0 EndX=5.21097e-06 EndY=19 EndZ=0
    g1: ArcOfCircle CenterX=19 CenterY=19 CenterZ=0 NormalX=0 NormalY=0 NormalZ=1 AngleXU=0 Radius=19 StartAngle=1.5708 EndAngle=3.14159
    g2: ArcOfCircle CenterX=19 CenterY=19 CenterZ=0 NormalX=0 NormalY=0 NormalZ=1 AngleXU=0 Radius=16 StartAngle=1.5708 EndAngle=3.14159
    g3: LineSegment StartX=114 StartY=35 StartZ=0 EndX=19 EndY=35 EndZ=0
    g4: LineSegment StartX=5.21097e-06 StartY=3 StartZ=0 EndX=5.21097e-06 EndY=0 EndZ=0
    g5: LineSegment StartX=3 StartY=0 StartZ=0 EndX=5.21097e-06 EndY=0 EndZ=0
    g6: LineSegment StartX=3 StartY=19 StartZ=0 EndX=3 EndY=0 EndZ=0
    g7: LineSegment StartX=19 StartY=38 StartZ=0 EndX=124 EndY=38 EndZ=0
    g8: Circle CenterX=119 CenterY=35 CenterZ=0 NormalX=0 NormalY=0 NormalZ=1 AngleXU=0 Radius=1
    g9: Circle CenterX=121 CenterY=35 CenterZ=0 NormalX=0 NormalY=0 NormalZ=1 AngleXU=0 Radius=1
    g10: Circle CenterX=121 CenterY=33 CenterZ=0 NormalX=0 NormalY=0 NormalZ=1 AngleXU=0 Radius=1
    g11: BSplineCurve PolesCount=3 KnotsCount=2 Degree=2 IsPeriodic=0
    g12: GeomPoint X=119 Y=35 Z=0
    g13: GeomPoint X=121 Y=33 Z=0
    g14: LineSegment StartX=119 StartY=35 StartZ=0 EndX=114 EndY=35 EndZ=0
    g15: ArcOfCircle CenterX=105 CenterY=19 CenterZ=0 NormalX=0 NormalY=0 NormalZ=1 AngleXU=0 Radius=19 StartAngle=5.7297 EndAngle=6.28319
    g16: ArcOfCircle CenterX=105 CenterY=19 CenterZ=0 NormalX=0 NormalY=0 NormalZ=1 AngleXU=0 Radius=16 StartAngle=5.60905 EndAngle=6.28319
    g17: LineSegment StartX=121 StartY=33 StartZ=0 EndX=121 EndY=19 EndZ=0
    g18: LineSegment StartX=124 StartY=38 StartZ=0 EndX=124 EndY=19 EndZ=0
    g19: LineSegment StartX=117.5 StartY=9.01251 StartZ=0 EndX=121.163 EndY=9.0125 EndZ=0
  constraints (46):
    c: Vertical(g0)
    c: Block(g0)
    c: Coincident(g1,g0)
    c: Block(g1)
    c: Coincident(g2,g1)
    c: Block(g2)
    c: Coincident(g3,g2)
    c: Horizontal(g3)
    c: Tangent(g3,g2)
    c: Coincident(g4,g0)
    c: Distance(g4) = 3
    c: Vertical(g4)
    c: Coincident(g5,g4)
    c: Horizontal(g5)
    c: Coincident(g6,g2)
    c: Coincident(g6,g5)
    c: Vertical(g6)
    c: Horizontal(g7)
    c: Distance(g7) = 105
    c: Coincident(g7,g1)
    c: Block(g3)
    c: Weight(g8) = 1
    c: Equal(g8,g9)
    c: Equal(g8,g10)
    c: InternalAlignment(g8,g11)
    c: InternalAlignment(g9,g11)
    c: InternalAlignment(g10,g11)
    c: InternalAlignment(g12,g11)
    c: InternalAlignment(g13,g11)
    c: Block(g11)
    c: Coincident(g14,g11)
    c: Coincident(g14,g3)
    c: Horizontal(g14)
    c: Block(g15)
    c: Coincident(g16,g15)
    c: Block(g16)
    c: Coincident(g17,g11)
    c: Coincident(g17,g16)
    c: Vertical(g17)
    c: Distance(g17) = 14
    c: Coincident(g18,g7)
    c: Coincident(g18,g15)
    c: Vertical(g18)
    c: Distance(g18) = 19
    c: Coincident(g19,g16)
    c: Coincident(g19,g15)
FEATURE [Part::Extrusion] Extrude049  label="top023"
  Base = -> Sketch058
  Dir = (0,0,1)
  DirMode = 2
  FaceMakerClass = Part::FaceMakerBullseye
  LengthFwd = 72
  LengthRev = 0
  Solid = true
  Symmetric = false
FEATURE [Sketcher::SketchObject] Sketch059
  FullyConstrained = true
  MapMode = 3
  Placement = pos=(0,0,0) rot=(1,0,0;1.5708rad)
  Support = -> [Extrude049]
  sketch-geometry (8):
    g0: Circle CenterX=80.351 CenterY=-67.6202 CenterZ=0 NormalX=0 NormalY=0 NormalZ=1 AngleXU=0 Radius=2
    g1: Circle CenterX=80.351 CenterY=-67.6202 CenterZ=0 NormalX=0 NormalY=0 NormalZ=1 AngleXU=0 Radius=3
    g2: Circle CenterX=80.351 CenterY=-4.92017 CenterZ=0 NormalX=0 NormalY=0 NormalZ=1 AngleXU=0 Radius=2
    g3: Circle CenterX=80.351 CenterY=-4.92017 CenterZ=0 NormalX=0 NormalY=0 NormalZ=1 AngleXU=0 Radius=3
    g4: Circle CenterX=23.851 CenterY=-4.92017 CenterZ=0 NormalX=0 NormalY=0 NormalZ=1 AngleXU=0 Radius=2
    g5: Circle CenterX=23.851 CenterY=-4.92017 CenterZ=0 NormalX=0 NormalY=0 NormalZ=1 AngleXU=0 Radius=3
    g6: Circle CenterX=23.851 CenterY=-67.6202 CenterZ=0 NormalX=0 NormalY=0 NormalZ=1 AngleXU=0 Radius=2
    g7: Circle CenterX=23.851 CenterY=-67.6202 CenterZ=0 NormalX=0 NormalY=0 NormalZ=1 AngleXU=0 Radius=3
  constraints (8):
    c: Block(g3)
    c: Block(g2)
    c: Block(g1)
    c: Block(g0)
    c: Block(g6)
    c: Block(g7)
    c: Block(g4)
    c: Block(g5)
FEATURE [Sketcher::SketchObject] Sketch060
  FullyConstrained = true
  MapMode = 3
  Placement = pos=(0,0,0) rot=(1,0,0;1.5708rad)
  Support = -> [Extrude049]
  sketch-geometry (8):
    g0: Circle CenterX=80.351 CenterY=-67.6202 CenterZ=0 NormalX=0 NormalY=0 NormalZ=1 AngleXU=0 Radius=3
    g1: Circle CenterX=80.351 CenterY=-4.92017 CenterZ=0 NormalX=0 NormalY=0 NormalZ=1 AngleXU=0 Radius=3
    g2: Circle CenterX=23.851 CenterY=-4.92017 CenterZ=0 NormalX=0 NormalY=0 NormalZ=1 AngleXU=0 Radius=3
    g3: Circle CenterX=23.851 CenterY=-67.6202 CenterZ=0 NormalX=0 NormalY=0 NormalZ=1 AngleXU=0 Radius=3
    g4: Circle CenterX=23.851 CenterY=-67.6202 CenterZ=0 NormalX=0 NormalY=0 NormalZ=1 AngleXU=0 Radius=5
    g5: Circle CenterX=80.351 CenterY=-67.6202 CenterZ=0 NormalX=0 NormalY=0 NormalZ=1 AngleXU=0 Radius=5
    g6: Circle CenterX=23.851 CenterY=-4.92017 CenterZ=0 NormalX=0 NormalY=0 NormalZ=1 AngleXU=0 Radius=5
    g7: Circle CenterX=80.351 CenterY=-4.92017 CenterZ=0 NormalX=0 NormalY=0 NormalZ=1 AngleXU=0 Radius=5
  constraints (8):
    c: Block(g1)
    c: Block(g0)
    c: Block(g3)
    c: Block(g2)
    c: Block(g5)
    c: Block(g4)
    c: Block(g6)
    c: Block(g7)
FEATURE [Sketcher::SketchObject] Sketch061
  FullyConstrained = true
  MapMode = 3
  Placement = pos=(0,0,0) rot=(1,0,0;1.5708rad)
  sketch-geometry (8):
    g0: Circle CenterX=80.351 CenterY=-67.6202 CenterZ=0 NormalX=0 NormalY=0 NormalZ=1 AngleXU=0 Radius=3
    g1: Circle CenterX=80.351 CenterY=-4.92017 CenterZ=0 NormalX=0 NormalY=0 NormalZ=1 AngleXU=0 Radius=3
    g2: Circle CenterX=23.851 CenterY=-4.92017 CenterZ=0 NormalX=0 NormalY=0 NormalZ=1 AngleXU=0 Radius=3
    g3: Circle CenterX=23.851 CenterY=-67.6202 CenterZ=0 NormalX=0 NormalY=0 NormalZ=1 AngleXU=0 Radius=3
    g4: Circle CenterX=23.851 CenterY=-67.6202 CenterZ=0 NormalX=0 NormalY=0 NormalZ=1 AngleXU=0 Radius=5
    g5: Circle CenterX=80.351 CenterY=-67.6202 CenterZ=0 NormalX=0 NormalY=0 NormalZ=1 AngleXU=0 Radius=5
    g6: Circle CenterX=23.851 CenterY=-4.92017 CenterZ=0 NormalX=0 NormalY=0 NormalZ=1 AngleXU=0 Radius=5
    g7: Circle CenterX=80.351 CenterY=-4.92017 CenterZ=0 NormalX=0 NormalY=0 NormalZ=1 AngleXU=0 Radius=5
  constraints (8):
    c: Block(g1)
    c: Block(g0)
    c: Block(g3)
    c: Block(g2)
    c: Block(g5)
    c: Block(g4)
    c: Block(g6)
    c: Block(g7)
FEATURE [Sketcher::SketchObject] Sketch062  label="topSketch016"
  FullyConstrained = true
  sketch-geometry (20):
    g0: LineSegment StartX=5.21097e-06 StartY=3 StartZ=0 EndX=5.21097e-06 EndY=19 EndZ=0
    g1: ArcOfCircle CenterX=19 CenterY=19 CenterZ=0 NormalX=0 NormalY=0 NormalZ=1 AngleXU=0 Radius=19 StartAngle=1.5708 EndAngle=3.14159
    g2: ArcOfCircle CenterX=19 CenterY=19 CenterZ=0 NormalX=0 NormalY=0 NormalZ=1 AngleXU=0 Radius=16 StartAngle=1.5708 EndAngle=3.14159
    g3: LineSegment StartX=114 StartY=35 StartZ=0 EndX=19 EndY=35 EndZ=0
    g4: LineSegment StartX=5.21097e-06 StartY=3 StartZ=0 EndX=5.21097e-06 EndY=0 EndZ=0
    g5: LineSegment StartX=3 StartY=0 StartZ=0 EndX=5.21097e-06 EndY=0 EndZ=0
    g6: LineSegment StartX=3 StartY=19 StartZ=0 EndX=3 EndY=0 EndZ=0
    g7: LineSegment StartX=19 StartY=38 StartZ=0 EndX=124 EndY=38 EndZ=0
    g8: Circle CenterX=119 CenterY=35 CenterZ=0 NormalX=0 NormalY=0 NormalZ=1 AngleXU=0 Radius=1
    g9: Circle CenterX=121 CenterY=35 CenterZ=0 NormalX=0 NormalY=0 NormalZ=1 AngleXU=0 Radius=1
    g10: Circle CenterX=121 CenterY=33 CenterZ=0 NormalX=0 NormalY=0 NormalZ=1 AngleXU=0 Radius=1
    g11: BSplineCurve PolesCount=3 KnotsCount=2 Degree=2 IsPeriodic=0
    g12: GeomPoint X=119 Y=35 Z=0
    g13: GeomPoint X=121 Y=33 Z=0
    g14: LineSegment StartX=119 StartY=35 StartZ=0 EndX=114 EndY=35 EndZ=0
    g15: ArcOfCircle CenterX=105 CenterY=19 CenterZ=0 NormalX=0 NormalY=0 NormalZ=1 AngleXU=0 Radius=19 StartAngle=5.7297 EndAngle=6.28319
    g16: ArcOfCircle CenterX=105 CenterY=19 CenterZ=0 NormalX=0 NormalY=0 NormalZ=1 AngleXU=0 Radius=16 StartAngle=5.60905 EndAngle=6.28319
    g17: LineSegment StartX=121 StartY=33 StartZ=0 EndX=121 EndY=19 EndZ=0
    g18: LineSegment StartX=124 StartY=38 StartZ=0 EndX=124 EndY=19 EndZ=0
    g19: LineSegment StartX=117.5 StartY=9.01251 StartZ=0 EndX=121.163 EndY=9.0125 EndZ=0
  constraints (46):
    c: Vertical(g0)
    c: Block(g0)
    c: Coincident(g1,g0)
    c: Block(g1)
    c: Coincident(g2,g1)
    c: Block(g2)
    c: Coincident(g3,g2)
    c: Horizontal(g3)
    c: Tangent(g3,g2)
    c: Coincident(g4,g0)
    c: Distance(g4) = 3
    c: Vertical(g4)
    c: Coincident(g5,g4)
    c: Horizontal(g5)
    c: Coincident(g6,g2)
    c: Coincident(g6,g5)
    c: Vertical(g6)
    c: Horizontal(g7)
    c: Distance(g7) = 105
    c: Coincident(g7,g1)
    c: Block(g3)
    c: Weight(g8) = 1
    c: Equal(g8,g9)
    c: Equal(g8,g10)
    c: InternalAlignment(g8,g11)
    c: InternalAlignment(g9,g11)
    c: InternalAlignment(g10,g11)
    c: InternalAlignment(g12,g11)
    c: InternalAlignment(g13,g11)
    c: Block(g11)
    c: Coincident(g14,g11)
    c: Coincident(g14,g3)
    c: Horizontal(g14)
    c: Block(g15)
    c: Coincident(g16,g15)
    c: Block(g16)
    c: Coincident(g17,g11)
    c: Coincident(g17,g16)
    c: Vertical(g17)
    c: Distance(g17) = 14
    c: Coincident(g18,g7)
    c: Coincident(g18,g15)
    c: Vertical(g18)
    c: Distance(g18) = 19
    c: Coincident(g19,g16)
    c: Coincident(g19,g15)
FEATURE [Part::Extrusion] Extrude053  label="top024"
  Base = -> Sketch062
  Dir = (0,0,1)
  DirMode = 2
  FaceMakerClass = Part::FaceMakerBullseye
  LengthFwd = 72
  LengthRev = 0
  Solid = true
  Symmetric = false
FEATURE [Sketcher::SketchObject] Sketch063
  FullyConstrained = true
  MapMode = 3
  Placement = pos=(0,0,0) rot=(1,0,0;1.5708rad)
  Support = -> [Extrude053]
  sketch-geometry (8):
    g0: Circle CenterX=80.351 CenterY=-67.6202 CenterZ=0 NormalX=0 NormalY=0 NormalZ=1 AngleXU=0 Radius=2
    g1: Circle CenterX=80.351 CenterY=-67.6202 CenterZ=0 NormalX=0 NormalY=0 NormalZ=1 AngleXU=0 Radius=3
    g2: Circle CenterX=80.351 CenterY=-4.92017 CenterZ=0 NormalX=0 NormalY=0 NormalZ=1 AngleXU=0 Radius=2
    g3: Circle CenterX=80.351 CenterY=-4.92017 CenterZ=0 NormalX=0 NormalY=0 NormalZ=1 AngleXU=0 Radius=3
    g4: Circle CenterX=23.851 CenterY=-4.92017 CenterZ=0 NormalX=0 NormalY=0 NormalZ=1 AngleXU=0 Radius=2
    g5: Circle CenterX=23.851 CenterY=-4.92017 CenterZ=0 NormalX=0 NormalY=0 NormalZ=1 AngleXU=0 Radius=3
    g6: Circle CenterX=23.851 CenterY=-67.6202 CenterZ=0 NormalX=0 NormalY=0 NormalZ=1 AngleXU=0 Radius=2
    g7: Circle CenterX=23.851 CenterY=-67.6202 CenterZ=0 NormalX=0 NormalY=0 NormalZ=1 AngleXU=0 Radius=3
  constraints (8):
    c: Block(g3)
    c: Block(g2)
    c: Block(g1)
    c: Block(g0)
    c: Block(g6)
    c: Block(g7)
    c: Block(g4)
    c: Block(g5)
FEATURE [Part::Extrusion] Extrude054
  Base = -> Sketch063
  Dir = (0,-1,2e-16)
  DirMode = 2
  FaceMakerClass = Part::FaceMakerBullseye
  LengthFwd = 6
  LengthRev = 0
  Placement = pos=(0,9,0) rot=(0,0,1;0rad)
  Solid = true
  Symmetric = false
FEATURE [Sketcher::SketchObject] Sketch064  label="topSketch017"
  FullyConstrained = true
  sketch-geometry (20):
    g0: LineSegment StartX=5.21097e-06 StartY=3 StartZ=0 EndX=5.21097e-06 EndY=19 EndZ=0
    g1: ArcOfCircle CenterX=19 CenterY=19 CenterZ=0 NormalX=0 NormalY=0 NormalZ=1 AngleXU=0 Radius=19 StartAngle=1.5708 EndAngle=3.14159
    g2: ArcOfCircle CenterX=19 CenterY=19 CenterZ=0 NormalX=0 NormalY=0 NormalZ=1 AngleXU=0 Radius=16 StartAngle=1.5708 EndAngle=3.14159
    g3: LineSegment StartX=114 StartY=35 StartZ=0 EndX=19 EndY=35 EndZ=0
    g4: LineSegment StartX=5.21097e-06 StartY=3 StartZ=0 EndX=5.21097e-06 EndY=0 EndZ=0
    g5: LineSegment StartX=3 StartY=0 StartZ=0 EndX=5.21097e-06 EndY=0 EndZ=0
    g6: LineSegment StartX=3 StartY=19 StartZ=0 EndX=3 EndY=0 EndZ=0
    g7: LineSegment StartX=19 StartY=38 StartZ=0 EndX=124 EndY=38 EndZ=0
    g8: Circle CenterX=119 CenterY=35 CenterZ=0 NormalX=0 NormalY=0 NormalZ=1 AngleXU=0 Radius=1
    g9: Circle CenterX=121 CenterY=35 CenterZ=0 NormalX=0 NormalY=0 NormalZ=1 AngleXU=0 Radius=1
    g10: Circle CenterX=121 CenterY=33 CenterZ=0 NormalX=0 NormalY=0 NormalZ=1 AngleXU=0 Radius=1
    g11: BSplineCurve PolesCount=3 KnotsCount=2 Degree=2 IsPeriodic=0
    g12: GeomPoint X=119 Y=35 Z=0
    g13: GeomPoint X=121 Y=33 Z=0
    g14: LineSegment StartX=119 StartY=35 StartZ=0 EndX=114 EndY=35 EndZ=0
    g15: ArcOfCircle CenterX=105 CenterY=19 CenterZ=0 NormalX=0 NormalY=0 NormalZ=1 AngleXU=0 Radius=19 StartAngle=5.7297 EndAngle=6.28319
    g16: ArcOfCircle CenterX=105 CenterY=19 CenterZ=0 NormalX=0 NormalY=0 NormalZ=1 AngleXU=0 Radius=16 StartAngle=5.60905 EndAngle=6.28319
    g17: LineSegment StartX=121 StartY=33 StartZ=0 EndX=121 EndY=19 EndZ=0
    g18: LineSegment StartX=124 StartY=38 StartZ=0 EndX=124 EndY=19 EndZ=0
    g19: LineSegment StartX=117.5 StartY=9.01251 StartZ=0 EndX=121.163 EndY=9.0125 EndZ=0
  constraints (46):
    c: Vertical(g0)
    c: Block(g0)
    c: Coincident(g1,g0)
    c: Block(g1)
    c: Coincident(g2,g1)
    c: Block(g2)
    c: Coincident(g3,g2)
    c: Horizontal(g3)
    c: Tangent(g3,g2)
    c: Coincident(g4,g0)
    c: Distance(g4) = 3
    c: Vertical(g4)
    c: Coincident(g5,g4)
    c: Horizontal(g5)
    c: Coincident(g6,g2)
    c: Coincident(g6,g5)
    c: Vertical(g6)
    c: Horizontal(g7)
    c: Distance(g7) = 105
    c: Coincident(g7,g1)
    c: Block(g3)
    c: Weight(g8) = 1
    c: Equal(g8,g9)
    c: Equal(g8,g10)
    c: InternalAlignment(g8,g11)
    c: InternalAlignment(g9,g11)
    c: InternalAlignment(g10,g11)
    c: InternalAlignment(g12,g11)
    c: InternalAlignment(g13,g11)
    c: Block(g11)
    c: Coincident(g14,g11)
    c: Coincident(g14,g3)
    c: Horizontal(g14)
    c: Block(g15)
    c: Coincident(g16,g15)
    c: Block(g16)
    c: Coincident(g17,g11)
    c: Coincident(g17,g16)
    c: Vertical(g17)
    c: Distance(g17) = 14
    c: Coincident(g18,g7)
    c: Coincident(g18,g15)
    c: Vertical(g18)
    c: Distance(g18) = 19
    c: Coincident(g19,g16)
    c: Coincident(g19,g15)
FEATURE [Sketcher::SketchObject] Sketch065
  FullyConstrained = true
  MapMode = 3
  Placement = pos=(0,0,0) rot=(1,0,0;1.5708rad)
  sketch-geometry (8):
    g0: Circle CenterX=80.351 CenterY=-67.6202 CenterZ=0 NormalX=0 NormalY=0 NormalZ=1 AngleXU=0 Radius=3
    g1: Circle CenterX=80.351 CenterY=-4.92017 CenterZ=0 NormalX=0 NormalY=0 NormalZ=1 AngleXU=0 Radius=3
    g2: Circle CenterX=23.851 CenterY=-4.92017 CenterZ=0 NormalX=0 NormalY=0 NormalZ=1 AngleXU=0 Radius=3
    g3: Circle CenterX=23.851 CenterY=-67.6202 CenterZ=0 NormalX=0 NormalY=0 NormalZ=1 AngleXU=0 Radius=3
    g4: Circle CenterX=23.851 CenterY=-67.6202 CenterZ=0 NormalX=0 NormalY=0 NormalZ=1 AngleXU=0 Radius=5
    g5: Circle CenterX=80.351 CenterY=-67.6202 CenterZ=0 NormalX=0 NormalY=0 NormalZ=1 AngleXU=0 Radius=5
    g6: Circle CenterX=23.851 CenterY=-4.92017 CenterZ=0 NormalX=0 NormalY=0 NormalZ=1 AngleXU=0 Radius=5
    g7: Circle CenterX=80.351 CenterY=-4.92017 CenterZ=0 NormalX=0 NormalY=0 NormalZ=1 AngleXU=0 Radius=5
  constraints (8):
    c: Block(g1)
    c: Block(g0)
    c: Block(g3)
    c: Block(g2)
    c: Block(g5)
    c: Block(g4)
    c: Block(g6)
    c: Block(g7)
FEATURE [Part::Extrusion] Extrude056
  Base = -> Sketch065
  Dir = (0,-1,2e-16)
  DirMode = 2
  FaceMakerClass = Part::FaceMakerBullseye
  LengthFwd = 2
  LengthRev = 0
  Solid = true
  Symmetric = false
FEATURE [Part::Extrusion] Extrude057  label="top025"
  Base = -> Sketch064
  Dir = (0,0,1)
  DirMode = 2
  FaceMakerClass = Part::FaceMakerBullseye
  LengthFwd = 72
  LengthRev = 0
  Solid = true
  Symmetric = false
FEATURE [Sketcher::SketchObject] Sketch066
  FullyConstrained = true
  MapMode = 3
  Placement = pos=(0,0,0) rot=(1,0,0;1.5708rad)
  Support = -> [Extrude057]
  sketch-geometry (8):
    g0: Circle CenterX=80.351 CenterY=-67.6202 CenterZ=0 NormalX=0 NormalY=0 NormalZ=1 AngleXU=0 Radius=3
    g1: Circle CenterX=80.351 CenterY=-4.92017 CenterZ=0 NormalX=0 NormalY=0 NormalZ=1 AngleXU=0 Radius=3
    g2: Circle CenterX=23.851 CenterY=-4.92017 CenterZ=0 NormalX=0 NormalY=0 NormalZ=1 AngleXU=0 Radius=3
    g3: Circle CenterX=23.851 CenterY=-67.6202 CenterZ=0 NormalX=0 NormalY=0 NormalZ=1 AngleXU=0 Radius=3
    g4: Circle CenterX=23.851 CenterY=-67.6202 CenterZ=0 NormalX=0 NormalY=0 NormalZ=1 AngleXU=0 Radius=5
    g5: Circle CenterX=80.351 CenterY=-67.6202 CenterZ=0 NormalX=0 NormalY=0 NormalZ=1 AngleXU=0 Radius=5
    g6: Circle CenterX=23.851 CenterY=-4.92017 CenterZ=0 NormalX=0 NormalY=0 NormalZ=1 AngleXU=0 Radius=5
    g7: Circle CenterX=80.351 CenterY=-4.92017 CenterZ=0 NormalX=0 NormalY=0 NormalZ=1 AngleXU=0 Radius=5
  constraints (8):
    c: Block(g1)
    c: Block(g0)
    c: Block(g3)
    c: Block(g2)
    c: Block(g5)
    c: Block(g4)
    c: Block(g6)
    c: Block(g7)
FEATURE [Part::Extrusion] Extrude055
  Base = -> Sketch066
  Dir = (0,-1,2e-16)
  DirMode = 2
  FaceMakerClass = Part::FaceMakerBullseye
  LengthFwd = 2
  LengthRev = 0
  Solid = true
  Symmetric = false
FEATURE [Part::Fillet] Fillet041
  Base = -> Extrude056
  Edges = 4 edges r=1.99: [Edge6,Edge12,Edge18,Edge24]
FEATURE [Part::Cut] Cut045
  Base = -> Extrude055
  Placement = pos=(0,6,0) rot=(0,0,1;0rad)
  Tool = -> Fillet041
FEATURE [Part::MultiFuse] Fusion095  label="pcbScrewPillars"
  Placement = pos=(-3.2,-1,72.3) rot=(0,0,1;0rad)
  Shapes = -> [Cut045,Extrude054]
FEATURE [Part::Feature] Face113
  shape: bbox 3.2 x 1.5 x 2e-07 mm, 1 faces, 0 solids (baked)
FEATURE [Part::Revolution] Revolve121  label="backCaseScrewRetainer002"
  Angle = 360
  Axis = (0,1,0)
  Base = (0,0,0)
  FaceMakerClass = Part::FaceMakerBullseye
  Placement = pos=(12.5,3,62) rot=(0,0,1;0rad)
  Solid = false
  Source = -> Face113
  Symmetric = false
FEATURE [Part::Feature] Face114
  shape: bbox 3.2 x 1.5 x 2e-07 mm, 1 faces, 0 solids (baked)
FEATURE [Part::Feature] Face115
  shape: bbox 3.2 x 1.5 x 2e-07 mm, 1 faces, 0 solids (baked)
FEATURE [Part::Feature] Face116
  shape: bbox 3.2 x 1.5 x 2e-07 mm, 1 faces, 0 solids (baked)
FEATURE [Part::Revolution] Revolve122  label="frontCaseScrewRetainer004"
  Angle = 360
  Axis = (0,1,0)
  Base = (0,0,0)
  FaceMakerClass = Part::FaceMakerBullseye
  Placement = pos=(89.5,3,68.5) rot=(0,0,1;0rad)
  Solid = false
  Source = -> Face115
  Symmetric = false
FEATURE [Part::Revolution] Revolve123  label="frontCaseScrewRetainer005"
  Angle = 360
  Axis = (0,1,0)
  Base = (0,0,0)
  FaceMakerClass = Part::FaceMakerBullseye
  Placement = pos=(89.5,3,3.5) rot=(0,0,1;0rad)
  Solid = false
  Source = -> Face116
  Symmetric = false
FEATURE [Part::Revolution] Revolve124  label="backCaseScrewRetainer003"
  Angle = 360
  Axis = (0,1,0)
  Base = (0,0,0)
  FaceMakerClass = Part::FaceMakerBullseye
  Placement = pos=(12.5,3,10) rot=(0,0,1;0rad)
  Solid = false
  Source = -> Face114
  Symmetric = false
FEATURE [Part::Feature] Face117
  shape: bbox 3.6 x 3.2 x 2e-07 mm, 1 faces, 0 solids (baked)
FEATURE [Part::Revolution] Revolve125  label="moreFrontCaseScrewRetainer004"
  Angle = 360
  Axis = (0,1,0)
  Base = (0,0,0)
  FaceMakerClass = Part::FaceMakerBullseye
  Placement = pos=(109.5,4.5,68.5) rot=(0,0,1;0rad)
  Solid = false
  Source = -> Face117
  Symmetric = false
FEATURE [Part::Feature] Face118
  shape: bbox 3.6 x 3.2 x 2e-07 mm, 1 faces, 0 solids (baked)
FEATURE [Part::Revolution] Revolve126  label="moreFrontCaseScrewRetainer005"
  Angle = 360
  Axis = (0,1,0)
  Base = (0,0,0)
  FaceMakerClass = Part::FaceMakerBullseye
  Placement = pos=(109.5,4.5,3.5) rot=(0,0,1;0rad)
  Solid = false
  Source = -> Face118
  Symmetric = false
FEATURE [Part::MultiFuse] Fusion096  label="screwRetainers001"
  Shapes = -> [Revolve126,Revolve125,Revolve124,Revolve123,Revolve122,Revolve121]
FEATURE [Part::Feature] Face119
  shape: bbox 10 x 16.5 x 2e-07 mm, 1 faces, 0 solids (baked)
FEATURE [Part::Revolution] Revolve130  label="plugHousing050"
  Angle = 360
  Axis = (0,1,0)
  Base = (0,0,0)
  FaceMakerClass = Part::FaceMakerBullseye
  Placement = pos=(0,0,36.15) rot=(0,0,1;0rad)
  Solid = false
  Source = -> Face119
  Symmetric = false
FEATURE [Part::Feature] Face120
  shape: bbox 10 x 16.5 x 2e-07 mm, 1 faces, 0 solids (baked)
FEATURE [Part::Feature] Face121
  shape: bbox 10 x 16.5 x 2e-07 mm, 1 faces, 0 solids (baked)
FEATURE [Part::Revolution] Revolve127  label="plugHousing047"
  Angle = 360
  Axis = (0,1,0)
  Base = (0,0,0)
  FaceMakerClass = Part::FaceMakerBullseye
  Placement = pos=(0,0,36.15) rot=(0,0,1;0rad)
  Solid = false
  Source = -> Face121
  Symmetric = false
FEATURE [Part::Feature] Face122
  shape: bbox 10 x 16.5 x 2e-07 mm, 1 faces, 0 solids (baked)
FEATURE [Part::Feature] Face123
  shape: bbox 10 x 16.5 x 2e-07 mm, 1 faces, 0 solids (baked)
FEATURE [Part::Revolution] Revolve128  label="plugHousing048"
  Angle = 360
  Axis = (0,1,0)
  Base = (0,0,0)
  FaceMakerClass = Part::FaceMakerBullseye
  Placement = pos=(0,0,36.15) rot=(0,0,1;0rad)
  Solid = false
  Source = -> Face123
  Symmetric = false
FEATURE [Part::MultiFuse] Fusion100  label="plugHousing054"
  Placement = pos=(0,0,0) rot=(0,0,1;1.5708rad)
  Shapes = -> [Revolve130,Revolve128]
FEATURE [Part::Feature] Face124
  shape: bbox 10 x 16.5 x 2e-07 mm, 1 faces, 0 solids (baked)
FEATURE [Part::Feature] Face125
  shape: bbox 10 x 16.5 x 2e-07 mm, 1 faces, 0 solids (baked)
FEATURE [Part::Revolution] Revolve129  label="plugHousing049"
  Angle = 360
  Axis = (0,1,0)
  Base = (0,0,0)
  FaceMakerClass = Part::FaceMakerBullseye
  Placement = pos=(0,0,36.15) rot=(0,0,1;0rad)
  Solid = false
  Source = -> Face125
  Symmetric = false
FEATURE [Part::Feature] Face126
  shape: bbox 10 x 16.5 x 2e-07 mm, 1 faces, 0 solids (baked)
FEATURE [Part::Revolution] Revolve131  label="plugHousing058"
  Angle = 360
  Axis = (0,1,0)
  Base = (0,0,0)
  FaceMakerClass = Part::FaceMakerBullseye
  Placement = pos=(0,0,36.15) rot=(0,0,1;0rad)
  Solid = false
  Source = -> Face120
  Symmetric = false
FEATURE [Part::MultiFuse] Fusion099  label="plugHousing053"
  Placement = pos=(0,0,0) rot=(0,0,1;1.5708rad)
  Shapes = -> [Revolve127,Revolve131]
FEATURE [Part::MultiFuse] Fusion102  label="plugHousing056"
  Placement = pos=(0,19,0) rot=(0,0,1;3.14159rad)
  Shapes = -> [Fusion100,Fusion099]
FEATURE [Part::Revolution] Revolve132  label="plugHousing059"
  Angle = 360
  Axis = (0,1,0)
  Base = (0,0,0)
  FaceMakerClass = Part::FaceMakerBullseye
  Placement = pos=(0,0,36.15) rot=(0,0,1;0rad)
  Solid = false
  Source = -> Face126
  Symmetric = false
FEATURE [Part::Revolution] Revolve133  label="plugHousing060"
  Angle = 360
  Axis = (0,1,0)
  Base = (0,0,0)
  FaceMakerClass = Part::FaceMakerBullseye
  Placement = pos=(0,0,36.15) rot=(0,0,1;0rad)
  Solid = false
  Source = -> Face122
  Symmetric = false
FEATURE [Part::MultiFuse] Fusion097  label="plugHousing051"
  Placement = pos=(0,0,0) rot=(0,0,1;1.5708rad)
  Shapes = -> [Revolve133,Revolve132]
FEATURE [Part::Revolution] Revolve134  label="plugHousing061"
  Angle = 360
  Axis = (0,1,0)
  Base = (0,0,0)
  FaceMakerClass = Part::FaceMakerBullseye
  Placement = pos=(0,0,36.15) rot=(0,0,1;0rad)
  Solid = false
  Source = -> Face124
  Symmetric = false
FEATURE [Part::MultiFuse] Fusion101  label="plugHousing055"
  Placement = pos=(0,0,0) rot=(0,0,1;1.5708rad)
  Shapes = -> [Revolve129,Revolve134]
FEATURE [Part::MultiFuse] Fusion098  label="plugHousing052"
  Placement = pos=(0,19,0) rot=(0,0,1;3.14159rad)
  Shapes = -> [Fusion097,Fusion101]
FEATURE [Part::MultiFuse] Fusion103  label="plugHousing057"
  Placement = pos=(122.621,0,-0.15) rot=(0,0,1;0rad)
  Shapes = -> [Fusion102,Fusion098]
FEATURE [Part::Box] Box028  label="Cube015"
  AttacherType = Attacher::AttachEngine3D
  Height = 28
  Length = 3
  Placement = pos=(110.7,19,22) rot=(0,0,1;0rad)
  Width = 15.7
FEATURE [Part::Cylinder] Cylinder044
  Angle = 360
  AttacherType = Attacher::AttachEngine3D
  Height = 20
  Placement = pos=(0,0,36.15) rot=(0,0,1;0rad)
  Radius = 10.3
FEATURE [Part::Cylinder] Cylinder045
  Angle = 360
  AttacherType = Attacher::AttachEngine3D
  Height = 10
  Placement = pos=(0,0,36.15) rot=(0,0,1;0rad)
  Radius = 4
FEATURE [Part::MultiFuse] Fusion104  label="removeToCreteHoleForPlugHousing040"
  Placement = pos=(70,19,36) rot=(0,1,0;1.5708rad)
  Shapes = -> [Cylinder044,Cylinder045]
FEATURE [Part::Cut] Cut046  label="plugHousingTab003"
  Base = -> Box028
  Tool = -> Fusion104
FEATURE [Part::MultiFuse] Fusion105  label="plugHousing062"
  Shapes = -> [Fusion103,Cut046]
FEATURE [Part::Fillet] Fillet042
  Base = -> Fusion105
  Edges = 1 edges r=2: [Edge25]
FEATURE [Part::Fillet] Fillet043  label="plugHousing063"
  Base = -> Fillet042
  Edges = 1 edges r=2: [Edge8]
  Placement = pos=(7,0,0) rot=(0,0,1;0rad)
FEATURE [Part::Feature] Face127
  shape: bbox 10 x 16.5 x 2e-07 mm, 1 faces, 0 solids (baked)
FEATURE [Part::Feature] Face128
  shape: bbox 10 x 16.5 x 2e-07 mm, 1 faces, 0 solids (baked)
FEATURE [Part::Revolution] Revolve137  label="plugHousing070"
  Angle = 360
  Axis = (0,1,0)
  Base = (0,0,0)
  FaceMakerClass = Part::FaceMakerBullseye
  Placement = pos=(0,0,36.15) rot=(0,0,1;0rad)
  Solid = false
  Source = -> Face127
  Symmetric = false
FEATURE [Part::Revolution] Revolve140  label="plugHousing073"
  Angle = 360
  Axis = (0,1,0)
  Base = (0,0,0)
  FaceMakerClass = Part::FaceMakerBullseye
  Placement = pos=(0,0,36.15) rot=(0,0,1;0rad)
  Solid = false
  Source = -> Face128
  Symmetric = false
FEATURE [Part::Feature] Face129
  shape: bbox 10 x 16.5 x 2e-07 mm, 1 faces, 0 solids (baked)
FEATURE [Part::Revolution] Revolve138  label="plugHousing071"
  Angle = 360
  Axis = (0,1,0)
  Base = (0,0,0)
  FaceMakerClass = Part::FaceMakerBullseye
  Placement = pos=(0,0,36.15) rot=(0,0,1;0rad)
  Solid = false
  Source = -> Face129
  Symmetric = false
FEATURE [Part::Feature] Face130
  shape: bbox 10 x 16.5 x 2e-07 mm, 1 faces, 0 solids (baked)
FEATURE [Part::Revolution] Revolve139  label="plugHousing072"
  Angle = 360
  Axis = (0,1,0)
  Base = (0,0,0)
  FaceMakerClass = Part::FaceMakerBullseye
  Placement = pos=(0,0,36.15) rot=(0,0,1;0rad)
  Solid = false
  Source = -> Face130
  Symmetric = false
FEATURE [Part::Feature] Face131
  shape: bbox 10 x 16.5 x 2e-07 mm, 1 faces, 0 solids (baked)
FEATURE [Part::Revolution] Revolve135  label="plugHousing068"
  Angle = 360
  Axis = (0,1,0)
  Base = (0,0,0)
  FaceMakerClass = Part::FaceMakerBullseye
  Placement = pos=(0,0,36.15) rot=(0,0,1;0rad)
  Solid = false
  Source = -> Face131
  Symmetric = false
FEATURE [Part::MultiFuse] Fusion112  label="plugHousing078"
  Placement = pos=(0,0,0) rot=(0,0,1;1.5708rad)
  Shapes = -> [Revolve135,Revolve139]
FEATURE [Part::Feature] Face132
  shape: bbox 10 x 16.5 x 2e-07 mm, 1 faces, 0 solids (baked)
FEATURE [Part::Revolution] Revolve141  label="plugHousing074"
  Angle = 360
  Axis = (0,1,0)
  Base = (0,0,0)
  FaceMakerClass = Part::FaceMakerBullseye
  Placement = pos=(0,0,36.15) rot=(0,0,1;0rad)
  Solid = false
  Source = -> Face132
  Symmetric = false
FEATURE [Part::MultiFuse] Fusion110  label="plugHousing076"
  Placement = pos=(0,0,0) rot=(0,0,1;1.5708rad)
  Shapes = -> [Revolve141,Revolve140]
FEATURE [Part::Feature] Face133
  shape: bbox 10 x 16.5 x 2e-07 mm, 1 faces, 0 solids (baked)
FEATURE [Part::Revolution] Revolve136  label="plugHousing069"
  Angle = 360
  Axis = (0,1,0)
  Base = (0,0,0)
  FaceMakerClass = Part::FaceMakerBullseye
  Placement = pos=(0,0,36.15) rot=(0,0,1;0rad)
  Solid = false
  Source = -> Face133
  Symmetric = false
FEATURE [Part::MultiFuse] Fusion106  label="plugHousing064"
  Placement = pos=(0,0,0) rot=(0,0,1;1.5708rad)
  Shapes = -> [Revolve138,Revolve136]
FEATURE [Part::MultiFuse] Fusion108  label="plugHousing066"
  Placement = pos=(0,19,0) rot=(0,0,1;3.14159rad)
  Shapes = -> [Fusion106,Fusion112]
FEATURE [Part::Feature] Face134
  shape: bbox 10 x 16.5 x 2e-07 mm, 1 faces, 0 solids (baked)
FEATURE [Part::Revolution] Revolve142  label="plugHousing075"
  Angle = 360
  Axis = (0,1,0)
  Base = (0,0,0)
  FaceMakerClass = Part::FaceMakerBullseye
  Placement = pos=(0,0,36.15) rot=(0,0,1;0rad)
  Solid = false
  Source = -> Face134
  Symmetric = false
FEATURE [Part::MultiFuse] Fusion107  label="plugHousing065"
  Placement = pos=(0,0,0) rot=(0,0,1;1.5708rad)
  Shapes = -> [Revolve137,Revolve142]
FEATURE [Part::MultiFuse] Fusion111  label="plugHousing077"
  Placement = pos=(0,19,0) rot=(0,0,1;3.14159rad)
  Shapes = -> [Fusion110,Fusion107]
FEATURE [Part::MultiFuse] Fusion109  label="plugHousing067"
  Placement = pos=(131.236,0,-0.15) rot=(0,0,1;0rad)
  Shapes = -> [Fusion108,Fusion111]
FEATURE [Part::MultiFuse] Fusion113  label="plugHousing079"
  Shapes = -> [Fillet043,Fusion109]
